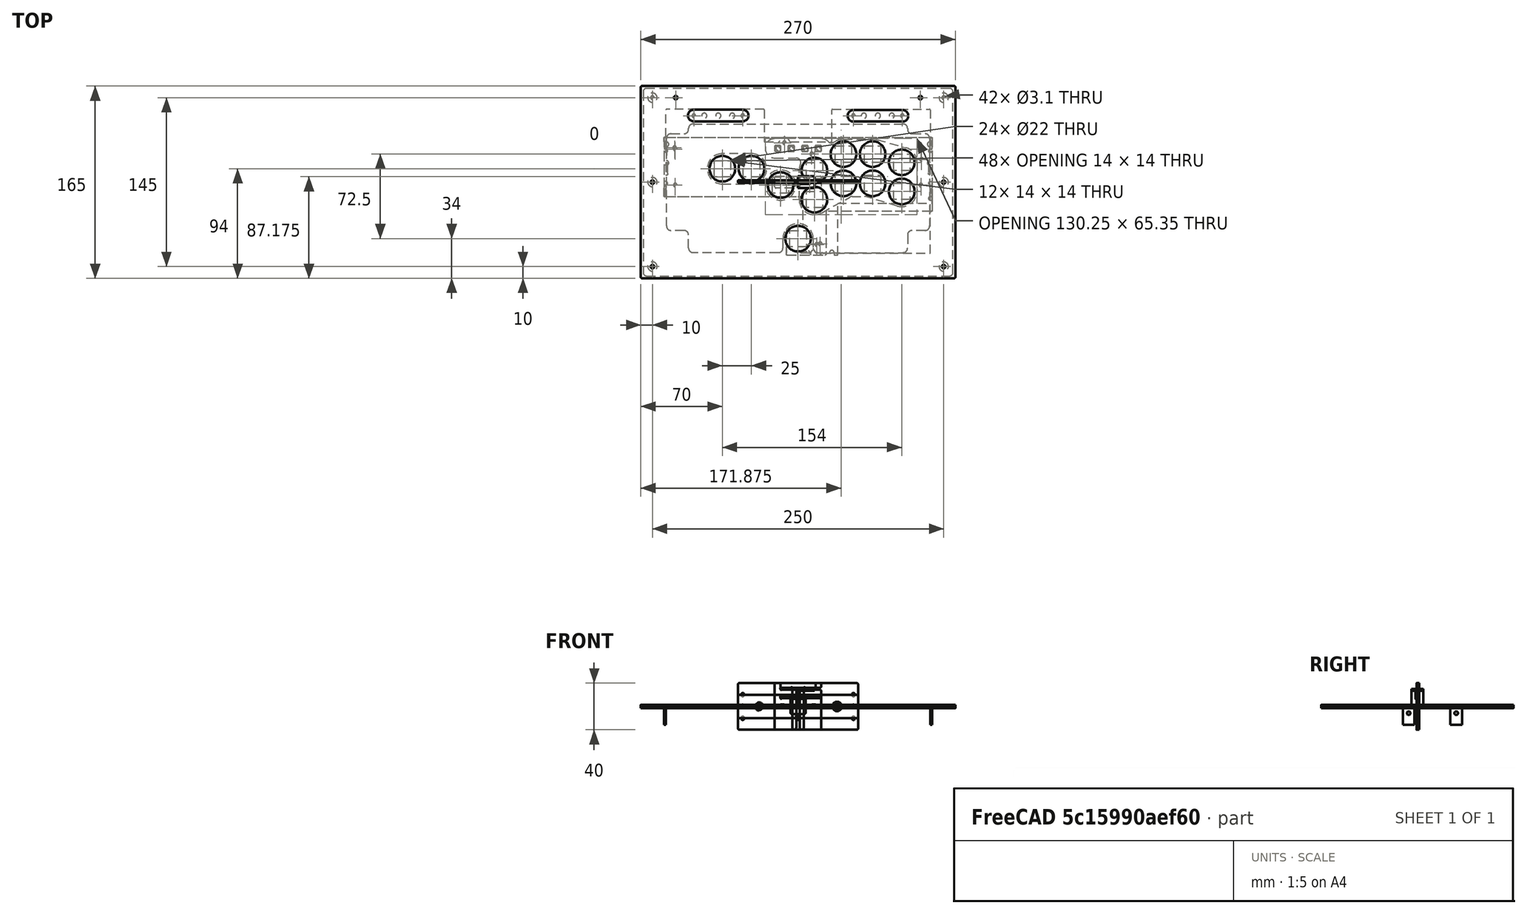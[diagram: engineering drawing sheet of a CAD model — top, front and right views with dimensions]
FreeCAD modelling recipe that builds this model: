
FCSTD DOCUMENT  (FreeCAD 2022.801R14555 (Git shallow))
Label: abc-flat-profiles-plate
License: All rights reserved
LicenseURL: http://en.wikipedia.org/wiki/All_rights_reserved
objects: Sketcher::SketchObject×30, PartDesign::Fillet×21, PartDesign::Body×21, PartDesign::Pad×20, Part::SubShapeBinder×14, PartDesign::SubShapeBinder×13, PartDesign::Pocket×4, PartDesign::FeaturePython×2, App::LinkGroup×2, Spreadsheet::Sheet×1, PartDesign::FeatureBase×1
note: 219 computed .brp shape members not serialized (recipe doc carries the construction recipe); baked Part::Feature solids carry a one-line shape summary decoded from their .brp
EXTERNAL_REF file=abc-flat-profiles.FCStd obj=Link001

FEATURE [Sketcher::SketchObject] Sketch003
  ArcFitTolerance = 0
  AttachmentSupport = -> [XZ_Plane004]
  ExternalBSplineMaxDegree = 0
  ExternalBSplineTolerance = 0
  FullyConstrained = true
  MapMode = 5
  Placement = pos=(0,0,0) rot=(0,0.707107,0.707107;3.14159rad)
  Support = -> [XZ_Plane004]
  TreeRank = 111
  sketch-geometry (38):
    g0: LineSegment StartX=-51.5 StartY=10 StartZ=0 EndX=-51.5 EndY=-10 EndZ=0
    g1: LineSegment StartX=-51.5 StartY=-10 StartZ=0 EndX=51.5 EndY=-10 EndZ=0
    g2: LineSegment StartX=51.5 StartY=-10 StartZ=0 EndX=51.5 EndY=10 EndZ=0
    g3: LineSegment StartX=51.5 StartY=10 StartZ=0 EndX=-51.5 EndY=10 EndZ=0
    g4: LineSegment StartX=-6.5 StartY=6.5 StartZ=0 EndX=-6.5 EndY=-6.5 EndZ=0
    g5: LineSegment StartX=-6.5 StartY=-6.5 StartZ=0 EndX=6.5 EndY=-6.5 EndZ=0
    g6: LineSegment StartX=6.5 StartY=-6.5 StartZ=0 EndX=6.5 EndY=6.5 EndZ=0
    g7: LineSegment StartX=6.5 StartY=6.5 StartZ=0 EndX=-6.5 EndY=6.5 EndZ=0
    g8: GeomPoint [constr] X=0 Y=0 Z=0
    g9: LineSegment [constr] StartX=-17.5 StartY=9.5 StartZ=0 EndX=-17.5 EndY=-9.5 EndZ=0
    g10: LineSegment [constr] StartX=-17.5 StartY=-9.5 StartZ=0 EndX=17.5 EndY=-9.5 EndZ=0
    g11: LineSegment [constr] StartX=17.5 StartY=-9.5 StartZ=0 EndX=17.5 EndY=9.5 EndZ=0
    g12: LineSegment [constr] StartX=17.5 StartY=9.5 StartZ=0 EndX=-17.5 EndY=9.5 EndZ=0
    g13: GeomPoint [constr] X=0 Y=0 Z=0
    g14: Circle CenterX=-47.5 CenterY=0 CenterZ=0 NormalX=0 NormalY=0 NormalZ=1 AngleXU=0 Radius=1.55
    g15: Circle CenterX=47.5 CenterY=0 CenterZ=0 NormalX=0 NormalY=0 NormalZ=1 AngleXU=0 Radius=1.55
    g16: GeomPoint [constr] X=-49.05 Y=0 Z=0
    g17: ArcOfCircle CenterX=-15 CenterY=0 CenterZ=0 NormalX=0 NormalY=0 NormalZ=1 AngleXU=0 Radius=1.55 StartAngle=1.5708 EndAngle=4.71239
    g18: ArcOfCircle CenterX=-12 CenterY=0 CenterZ=0 NormalX=0 NormalY=0 NormalZ=1 AngleXU=0 Radius=1.55 StartAngle=4.71239 EndAngle=7.85398
    g19: LineSegment StartX=-15 StartY=-1.55 StartZ=0 EndX=-12 EndY=-1.55 EndZ=0
    g20: LineSegment StartX=-12 StartY=1.55 StartZ=0 EndX=-15 EndY=1.55 EndZ=0
    g21: ArcOfCircle CenterX=12 CenterY=0 CenterZ=0 NormalX=0 NormalY=0 NormalZ=1 AngleXU=0 Radius=1.55 StartAngle=1.5708 EndAngle=4.71239
    g22: ArcOfCircle CenterX=15 CenterY=0 CenterZ=0 NormalX=0 NormalY=0 NormalZ=1 AngleXU=0 Radius=1.55 StartAngle=4.71239 EndAngle=7.85398
    g23: LineSegment StartX=12 StartY=-1.55 StartZ=0 EndX=15 EndY=-1.55 EndZ=0
    g24: LineSegment StartX=15 StartY=1.55 StartZ=0 EndX=12 EndY=1.55 EndZ=0
    g25: LineSegment [constr] StartX=-19.5 StartY=7.3 StartZ=0 EndX=-19.5 EndY=-7.3 EndZ=0
    g26: LineSegment [constr] StartX=-19.5 StartY=-7.3 StartZ=0 EndX=19.5 EndY=-7.3 EndZ=0
    g27: LineSegment [constr] StartX=19.5 StartY=-7.3 StartZ=0 EndX=19.5 EndY=7.3 EndZ=0
    g28: LineSegment [constr] StartX=19.5 StartY=7.3 StartZ=0 EndX=-19.5 EndY=7.3 EndZ=0
    g29: GeomPoint [constr] X=0 Y=0 Z=0
    g30: Circle CenterX=33.5 CenterY=0 CenterZ=0 NormalX=0 NormalY=0 NormalZ=1 AngleXU=0 Radius=3.175
    g31: GeomPoint [constr] X=30.325 Y=0 Z=0
    g32: GeomPoint [constr] X=36.675 Y=0 Z=0
    g33: GeomPoint [constr] X=45.95 Y=0 Z=0
    g34: Circle CenterX=-33.5 CenterY=0 CenterZ=0 NormalX=0 NormalY=0 NormalZ=1 AngleXU=0 Radius=4.05
    g35: GeomPoint [constr] X=-49.05 Y=0 Z=0
    g36: LineSegment [constr] StartX=-47.5 StartY=0 StartZ=0 EndX=-19.5 EndY=0 EndZ=0
    g37: LineSegment [constr] StartX=47.5 StartY=0 StartZ=0 EndX=19.5 EndY=0 EndZ=0
  constraints (91):
    c: Coincident(g0,g1)
    c: Coincident(g1,g2)
    c: Coincident(g3,g0)
    c: Horizontal(g1)
    c: Vertical(g0)
    c: Vertical(g2)
    c: DistanceY(g0,g0) = 20
    c: Horizontal(g3)
    c: Coincident(g3,g2)
    c: Symmetric(g0,g1,g-1)
    c: Coincident(g4,g5)
    c: Coincident(g5,g6)
    c: Coincident(g6,g7)
    c: Coincident(g7,g4)
    c: Horizontal(g5)
    c: Horizontal(g7)
    c: Vertical(g4)
    c: Vertical(g6)
    c: Symmetric(g5,g4,g8)
    c: Coincident(g8,g-1)
    c: DistanceY(g6,g6) = 13
    c: DistanceX(g5,g5) = 13
    c: Coincident(g9,g10)
    c: Coincident(g10,g11)
    c: Coincident(g11,g12)
    c: Coincident(g12,g9)
    c: Horizontal(g10)
    c: Horizontal(g12)
    c: Vertical(g9)
    c: Vertical(g11)
    c: Symmetric(g10,g9,g13)
    c: Coincident(g13,g8)
    c: DistanceX(g10,g10) = 35
    c: DistanceY(g9,g9) = 19
    c: PointOnObject(g14,g-1)
    c: Symmetric(g14,g15,g-2)
    c: Equal(g14,g15)
    c: PointOnObject(g16,g14)
    c: PointOnObject(g16,g-1)
    c: Tangent(g17,g19) = -1.5708
    c: Tangent(g19,g18) = -1.5708
    c: Tangent(g18,g20) = -1.5708
    c: Tangent(g20,g17) = -1.5708
    c: Equal(g17,g18)
    c: PointOnObject(g17,g-1)
    c: PointOnObject(g18,g-1)
    c: Tangent(g21,g23) = -1.5708
    c: Tangent(g23,g22) = -1.5708
    c: Tangent(g22,g24) = -1.5708
    c: Tangent(g24,g21) = -1.5708
    c: Equal(g21,g22)
    c: Diameter(g17) = 3.1
    c: Equal(g17,g21)
    c: Symmetric(g17,g22,g-2)
    c: Symmetric(g18,g21,g-2)
    c: DistanceX(g18,g21) = 24
    c: DistanceX(g17,g22) = 30
    c: Coincident(g25,g26)
    c: Coincident(g26,g27)
    c: Coincident(g27,g28)
    c: Coincident(g28,g25)
    c: Horizontal(g26)
    c: Horizontal(g28)
    c: Vertical(g25)
    c: Vertical(g27)
    c: Symmetric(g26,g25,g29)
    c: Coincident(g29,g8)
    c: DistanceX(g26,g26) = 39
    c: DistanceY(g27,g27) = 14.6
    c: PointOnObject(g30,g-1)
    c: Diameter(g30) = 6.35
    c: PointOnObject(g31,g30)
    c: PointOnObject(g31,g-1)
    c: PointOnObject(g32,g-1)
    c: PointOnObject(g32,g30)
    c: PointOnObject(g33,g15)
    c: PointOnObject(g33,g-1)
    c: Diameter(g14) = 3.1
    c: PointOnObject(g34,g-1)
    c: Diameter(g34) = 8.1
    c: PointOnObject(g35,g14)
    c: PointOnObject(g35,g-1)
    c: Distance(g14,g0) = 4
    c: Distance(g14,g34) = 14
    c: Coincident(g36,g14)
    c: PointOnObject(g36,g25)
    c: Symmetric(g36,g36,g34)
    c: Coincident(g37,g15)
    c: PointOnObject(g37,g27)
    c: Symmetric(g37,g37,g30)
    c: DistanceX(g3,g3) = 103
FEATURE [PartDesign::Pad] Pad004
  AddSubType = 0
  AlongSketchNormal = false
  CheckUpToFaceLimits = true
  ClaimChildren = false
  Direction = (0,1,2e-16)
  Fit = 0
  FitJoin = 0
  InnerFit = 0
  InnerFitJoin = 0
  InnerTaperAngle = 0
  InnerTaperAngleRev = 0
  Length = 1.5
  Length2 = 100
  Linearize = true
  Midplane = true
  NewSolid = false
  Placement = pos=(0,0,0) rot=(1,0,0;1.5708rad)
  Profile = -> Sketch003
  Suppress = false
  TreeRank = 113
  Type = 0
  _ProfileBasedVersion = 1
FEATURE [PartDesign::Fillet] Fillet005
  AddSubType = 0
  Base = -> Pad004 [Edge5,Edge8,Edge2,Edge1,Edge17,Edge20,Edge13,Edge14]
  BaseFeature = -> Pad004
  NewSolid = false
  Placement = pos=(0,0,0) rot=(1,0,0;1.5708rad)
  Radius = 1
  SupportTransform = false
  Suppress = false
  TreeRank = 114
FEATURE [PartDesign::Body] Body004  label="JackPanel"
  AutoGroupSolids = false
  ClaimAllChildren = false
  ExportMode = 0
  Group = -> [Sketch003,Pad004,Fillet005]
  Origin = -> Origin004
  Tip = -> Fillet005
  TreeRank = 110
  _ExportChildren = -> [Pad004,Fillet005]
  _GroupVersion = 1
FEATURE [Sketcher::SketchObject] Sketch004
  ArcFitTolerance = 0
  AttachmentSupport = -> [XZ_Plane005]
  ExternalBSplineMaxDegree = 0
  ExternalBSplineTolerance = 0
  FullyConstrained = true
  MapMode = 5
  Placement = pos=(0,0,0) rot=(1,0,0;1.5708rad)
  Support = -> [XZ_Plane005]
  TreeRank = 133
  sketch-geometry (29):
    g0: LineSegment StartX=-20 StartY=10 StartZ=0 EndX=-20 EndY=-7 EndZ=0
    g1: LineSegment StartX=-20 StartY=-10 StartZ=0 EndX=20 EndY=-10 EndZ=0
    g2: LineSegment StartX=20 StartY=-10 StartZ=0 EndX=20 EndY=4 EndZ=0
    g3: LineSegment StartX=20 StartY=10 StartZ=0 EndX=-20 EndY=10 EndZ=0
    g4: GeomPoint [constr] X=0 Y=0 Z=0
    g5: LineSegment StartX=-15 StartY=6 StartZ=0 EndX=18.134 EndY=6 EndZ=0
    g6: LineSegment StartX=-15 StartY=4.5 StartZ=0 EndX=-15 EndY=5.2 EndZ=0
    g7: Circle CenterX=0 CenterY=0 CenterZ=0 NormalX=0 NormalY=0 NormalZ=1 AngleXU=0 Radius=1.55
    g8: GeomPoint [constr] X=15 Y=4.5 Z=0
    g9: LineSegment [constr] StartX=-20 StartY=10 StartZ=0 EndX=-20 EndY=14.5 EndZ=0
    g10: LineSegment [constr] StartX=-20 StartY=14.5 StartZ=0 EndX=20 EndY=14.5 EndZ=0
    g11: LineSegment [constr] StartX=20 StartY=14.5 StartZ=0 EndX=20 EndY=10 EndZ=0
    g12: LineSegment StartX=20 StartY=6.5 StartZ=0 EndX=20 EndY=10 EndZ=0
    g13: LineSegment [constr] StartX=20 StartY=-10 StartZ=0 EndX=20 EndY=-14.5 EndZ=0
    g14: LineSegment [constr] StartX=20 StartY=-14.5 StartZ=0 EndX=-20 EndY=-14.5 EndZ=0
    g15: LineSegment [constr] StartX=-20 StartY=-14.5 StartZ=0 EndX=-20 EndY=-10 EndZ=0
    g16: LineSegment [constr] StartX=-20 StartY=-7 StartZ=0 EndX=15 EndY=-7 EndZ=0
    g17: LineSegment [constr] StartX=15 StartY=-7 StartZ=0 EndX=15 EndY=-8.5 EndZ=0
    g18: LineSegment [constr] StartX=15 StartY=-8.5 StartZ=0 EndX=-20 EndY=-8.5 EndZ=0
    g19: GeomPoint [constr] X=-15 Y=-7 Z=0
    g20: LineSegment StartX=-20 StartY=-8.5 StartZ=0 EndX=-20 EndY=-10 EndZ=0
    g21: LineSegment StartX=-20 StartY=-8.5 StartZ=0 EndX=-20 EndY=-7 EndZ=0
    g22: ArcOfCircle CenterX=-15 CenterY=5.6 CenterZ=0 NormalX=0 NormalY=0 NormalZ=1 AngleXU=0 Radius=0.4 StartAngle=1.5708 EndAngle=4.71239
    g23: LineSegment StartX=18.134 StartY=6 StartZ=0 EndX=20 EndY=6.5 EndZ=0
    g24: LineSegment StartX=18.134 StartY=4.5 StartZ=0 EndX=20 EndY=4 EndZ=0
    g25: LineSegment StartX=18.134 StartY=4.5 StartZ=0 EndX=-14.2 EndY=4.5 EndZ=0
    g26: LineSegment [constr] StartX=-14.2 StartY=4.5 StartZ=0 EndX=-15 EndY=4.5 EndZ=0
    g27: ArcOfCircle CenterX=-14.6 CenterY=4.5 CenterZ=0 NormalX=0 NormalY=0 NormalZ=1 AngleXU=0 Radius=0.4 StartAngle=3.14159 EndAngle=6.28319
    g28: Circle [constr] CenterX=0 CenterY=0 CenterZ=0 NormalX=0 NormalY=0 NormalZ=1 AngleXU=0 Radius=3.5
  constraints (76):
    c: Coincident(g20,g1)
    c: Coincident(g1,g2)
    c: Coincident(g12,g3)
    c: Coincident(g3,g0)
    c: Horizontal(g1)
    c: Horizontal(g3)
    c: Vertical(g0)
    c: Vertical(g2)
    c: Symmetric(g1,g0,g4)
    c: Coincident(g4,g-1)
    c: DistanceX(g1,g1) = 40
    c: DistanceY(g20,g0) = 20
    c: Horizontal(g5)
    c: Vertical(g6)
    c: DistanceY(g26,g5) = 1.5
    c: Symmetric(g26,g8,g-2)
    c: DistanceX(g26,g8) = 30
    c: Coincident(g9,g0)
    c: Vertical(g9)
    c: Coincident(g10,g9)
    c: Horizontal(g10)
    c: Coincident(g11,g10)
    c: Coincident(g11,g12)
    c: Vertical(g11)
    c: DistanceY(g9,g9) = 4.5
    c: Distance(g9,g5) = 8.5
    c: Coincident(g7,g4)
    c: Diameter(g7) = 3.1
    c: Vertical(g12)
    c: Coincident(g13,g14)
    c: Coincident(g14,g15)
    c: Horizontal(g14)
    c: Vertical(g13)
    c: Vertical(g15)
    c: Coincident(g15,g20)
    c: Coincident(g13,g1)
    c: DistanceY(g15,g15) = 4.5
    c: Coincident(g16,g17)
    c: Coincident(g17,g18)
    c: Horizontal(g16)
    c: Horizontal(g18)
    c: Vertical(g17)
    c: DistanceY(g17,g17) = 1.5
    c: Symmetric(g19,g16,g-2)
    c: Distance(g19,g16) = 30
    c: Distance(g14,g18) = 6
    c: Coincident(g0,g16)
    c: Coincident(g20,g18)
    c: Vertical(g20)
    c: Coincident(g21,g18)
    c: Coincident(g21,g0)
    c: Vertical(g21)
    c: PointOnObject(g22,g6)
    c: Coincident(g22,g5)
    c: Diameter(g22) = 0.8
    c: Coincident(g6,g22)
    c: Vertical(g5,g6)
    c: Angle(g23,g5) = 2.87979
    c: Vertical(g23,g24)
    c: Coincident(g25,g24)
    c: Coincident(g2,g24)
    c: Coincident(g5,g23)
    c: Coincident(g12,g23)
    c: DistanceY(g2,g12) = 2.5
    c: Vertical(g2,g12)
    c: Coincident(g25,g26)
    c: Horizontal(g25)
    c: Horizontal(g26)
    c: PointOnObject(g27,g26)
    c: Coincident(g27,g25)
    c: Coincident(g27,g26)
    c: Coincident(g27,g6)
    c: Diameter(g27) = 0.8
    c: Angle(g25,g24) = 2.87979
    c: Coincident(g28,g7)
    c: Diameter(g28) = 7
FEATURE [PartDesign::Pad] Pad005
  AddSubType = 0
  AlongSketchNormal = false
  CheckUpToFaceLimits = true
  ClaimChildren = false
  Direction = (0,-1,-2e-16)
  Fit = 0
  FitJoin = 0
  InnerFit = 0
  InnerFitJoin = 0
  InnerTaperAngle = 0
  InnerTaperAngleRev = 0
  Length = 1.5
  Length2 = 100
  Linearize = true
  Midplane = true
  NewSolid = false
  Placement = pos=(0,0,0) rot=(1,0,0;1.5708rad)
  Profile = -> Sketch004
  Refine = true
  Suppress = false
  TreeRank = 134
  Type = 0
  _ProfileBasedVersion = 1
FEATURE [PartDesign::Fillet] Fillet006
  AddSubType = 0
  Base = -> Pad005 [Edge14,Edge27]
  BaseFeature = -> Pad005
  NewSolid = false
  Placement = pos=(0,0,0) rot=(1,0,0;1.5708rad)
  Radius = 0.4
  SupportTransform = false
  Suppress = false
  TreeRank = 135
FEATURE [PartDesign::Fillet] Fillet007
  AddSubType = 0
  Base = -> Fillet006 [Edge36,Edge21,Edge44,Edge43,Edge38,Edge40,Edge41,Edge42]
  BaseFeature = -> Fillet006
  NewSolid = false
  Placement = pos=(0,0,0) rot=(1,0,0;1.5708rad)
  Radius = 1
  SupportTransform = false
  Suppress = false
  TreeRank = 136
FEATURE [PartDesign::Body] Body005  label="Spacer"
  AutoGroupSolids = false
  ClaimAllChildren = false
  ExportMode = 0
  Group = -> [Sketch004,Pad005,Fillet006,Fillet007]
  Origin = -> Origin005
  Tip = -> Fillet007
  TreeRank = 132
  _ExportChildren = -> [Pad005,Fillet006,Fillet007]
  _GroupVersion = 1
FEATURE [Sketcher::SketchObject] Sketch005
  ArcFitTolerance = 0
  AttachmentSupport = -> [XZ_Plane006]
  ExternalBSplineMaxDegree = 0
  ExternalBSplineTolerance = 0
  FullyConstrained = true
  MapMode = 5
  Placement = pos=(0,0,0) rot=(1,0,0;1.5708rad)
  Support = -> [XZ_Plane006]
  TreeRank = 149
  sketch-geometry (30):
    g0: LineSegment StartX=-15 StartY=10 StartZ=0 EndX=15 EndY=10 EndZ=0
    g1: LineSegment StartX=15 StartY=10 StartZ=0 EndX=15 EndY=6 EndZ=0
    g2: LineSegment StartX=-15 StartY=6 StartZ=0 EndX=-15 EndY=10 EndZ=0
    g3: LineSegment StartX=-15 StartY=6 StartZ=0 EndX=-6 EndY=6 EndZ=0
    g4: LineSegment StartX=15 StartY=6 StartZ=0 EndX=6 EndY=6 EndZ=0
    g5: LineSegment StartX=-5 StartY=6 StartZ=0 EndX=-5 EndY=-8.13397 EndZ=0
    g6: LineSegment StartX=-4.5 StartY=-10 StartZ=0 EndX=-2.05 EndY=-10 EndZ=0
    g7: LineSegment StartX=-1.55 StartY=-8.13397 StartZ=0 EndX=-1.55 EndY=4.45 EndZ=0
    g8: LineSegment StartX=1.55 StartY=4.45 StartZ=0 EndX=1.55 EndY=-8.13397 EndZ=0
    g9: LineSegment StartX=2.05 StartY=-10 StartZ=0 EndX=4.5 EndY=-10 EndZ=0
    g10: LineSegment StartX=5 StartY=-8.13397 StartZ=0 EndX=5 EndY=6 EndZ=0
    g11: LineSegment [constr] StartX=-20 StartY=10 StartZ=0 EndX=-20 EndY=-10 EndZ=0
    g12: LineSegment [constr] StartX=-20 StartY=-10 StartZ=0 EndX=20 EndY=-10 EndZ=0
    g13: LineSegment [constr] StartX=20 StartY=-10 StartZ=0 EndX=20 EndY=10 EndZ=0
    g14: LineSegment [constr] StartX=20 StartY=10 StartZ=0 EndX=-20 EndY=10 EndZ=0
    g15: GeomPoint [constr] X=0 Y=0 Z=0
    g16: LineSegment [constr] StartX=-20 StartY=10 StartZ=0 EndX=-20 EndY=14.5 EndZ=0
    g17: LineSegment [constr] StartX=-20 StartY=14.5 StartZ=0 EndX=20 EndY=14.5 EndZ=0
    g18: LineSegment [constr] StartX=20 StartY=14.5 StartZ=0 EndX=20 EndY=10 EndZ=0
    g19: ArcOfCircle CenterX=-5.5 CenterY=6 CenterZ=0 NormalX=0 NormalY=0 NormalZ=1 AngleXU=0 Radius=0.5 StartAngle=2e-16 EndAngle=3.14159
    g20: ArcOfCircle CenterX=5.5 CenterY=6 CenterZ=0 NormalX=0 NormalY=0 NormalZ=1 AngleXU=0 Radius=0.5 StartAngle=2e-16 EndAngle=3.14159
    g21: ArcOfCircle CenterX=0 CenterY=4.45 CenterZ=0 NormalX=0 NormalY=0 NormalZ=1 AngleXU=0 Radius=1.55 StartAngle=0 EndAngle=3.14159
    g22: GeomPoint [constr] X=0 Y=6 Z=0
    g23: LineSegment StartX=-1.55 StartY=-8.13397 StartZ=0 EndX=-2.05 EndY=-10 EndZ=0
    g24: LineSegment StartX=1.55 StartY=-8.13397 StartZ=0 EndX=2.05 EndY=-10 EndZ=0
    g25: LineSegment [constr] StartX=-1.55 StartY=-8.13397 StartZ=0 EndX=-1.55 EndY=-10 EndZ=0
    g26: LineSegment StartX=-5 StartY=-8.13397 StartZ=0 EndX=-4.5 EndY=-10 EndZ=0
    g27: LineSegment StartX=5 StartY=-8.13397 StartZ=0 EndX=4.5 EndY=-10 EndZ=0
    g28: Circle [constr] CenterX=0 CenterY=0 CenterZ=0 NormalX=0 NormalY=0 NormalZ=1 AngleXU=0 Radius=3.5
    g29: Circle [constr] CenterX=0 CenterY=0 CenterZ=0 NormalX=0 NormalY=0 NormalZ=1 AngleXU=0 Radius=1.55
  constraints (84):
    c: Coincident(g0,g1)
    c: Coincident(g2,g0)
    c: Vertical(g1)
    c: Vertical(g2)
    c: Symmetric(g0,g0,g-2)
    c: Coincident(g3,g2)
    c: Horizontal(g3)
    c: Coincident(g4,g1)
    c: Horizontal(g4)
    c: Vertical(g5)
    c: Horizontal(g6)
    c: Vertical(g7)
    c: Vertical(g8)
    c: Horizontal(g9)
    c: Vertical(g10)
    c: DistanceX(g2,g1) = 30
    c: Coincident(g11,g12)
    c: Coincident(g12,g13)
    c: Coincident(g13,g14)
    c: Coincident(g14,g11)
    c: Horizontal(g12)
    c: Horizontal(g14)
    c: Vertical(g11)
    c: Vertical(g13)
    c: Symmetric(g12,g11,g15)
    c: Coincident(g15,g-1)
    c: DistanceY(g13,g13) = 20
    c: DistanceX(g12,g12) = 40
    c: Coincident(g11,g16)
    c: Vertical(g16)
    c: Coincident(g16,g17)
    c: Horizontal(g17)
    c: Coincident(g17,g18)
    c: Vertical(g18)
    c: Coincident(g18,g13)
    c: DistanceY(g16,g16) = 4.5
    c: Distance(g2,g17) = 8.5
    c: PointOnObject(g0,g14)
    c: DistanceX(g3,g5) = 10
    c: PointOnObject(g19,g3)
    c: Coincident(g19,g5)
    c: Diameter(g19) = 1
    c: Coincident(g3,g19)
    c: Horizontal(g3,g5)
    c: PointOnObject(g20,g4)
    c: Coincident(g20,g10)
    c: Equal(g19,g20)
    c: Coincident(g4,g20)
    c: Symmetric(g5,g10,g-2)
    c: Horizontal(g10,g4)
    c: PointOnObject(g21,g-2)
    c: Diameter(g21) = 3.1
    c: Coincident(g7,g21)
    c: Coincident(g8,g21)
    c: Horizontal(g7,g21)
    c: Horizontal(g21,g8)
    c: PointOnObject(g22,g21)
    c: PointOnObject(g22,g-2)
    c: Horizontal(g5,g22)
    c: Angle(g7,g23) = 2.87979
    c: Angle(g24,g8) = 2.87979
    c: Equal(g23,g24)
    c: Coincident(g6,g23)
    c: Coincident(g7,g23)
    c: Coincident(g8,g24)
    c: Coincident(g9,g24)
    c: Coincident(g25,g7)
    c: PointOnObject(g25,g12)
    c: Vertical(g25)
    c: Horizontal(g6,g9)
    c: DistanceX(g6,g25) = 0.5
    c: Angle(g26,g5) = 2.87979
    c: Angle(g10,g27) = 2.87979
    c: Horizontal(g26,g7)
    c: Horizontal(g27,g8)
    c: Coincident(g5,g26)
    c: Coincident(g6,g26)
    c: Coincident(g10,g27)
    c: Coincident(g9,g27)
    c: PointOnObject(g6,g12)
    c: Coincident(g28,g15)
    c: Diameter(g28) = 7
    c: Coincident(g29,g15)
    c: Diameter(g29) = 3.1
FEATURE [PartDesign::Pad] Pad006
  AddSubType = 0
  AlongSketchNormal = false
  CheckUpToFaceLimits = true
  ClaimChildren = false
  Direction = (0,-1,-2e-16)
  Fit = 0
  FitJoin = 0
  InnerFit = 0
  InnerFitJoin = 0
  InnerTaperAngle = 0
  InnerTaperAngleRev = 0
  Length = 1.5
  Length2 = 100
  Linearize = true
  Midplane = true
  NewSolid = false
  Placement = pos=(0,0,0) rot=(1,0,0;1.5708rad)
  Profile = -> Sketch005
  Suppress = false
  TreeRank = 150
  Type = 0
  _ProfileBasedVersion = 1
FEATURE [PartDesign::Fillet] Fillet008
  AddSubType = 0
  Base = -> Pad006 [Edge17,Edge2,Edge5,Edge8,Edge14,Edge11,Edge50,Edge44,Edge41,Edge32,Edge29,Edge23,Edge47,Edge26]
  BaseFeature = -> Pad006
  NewSolid = false
  Placement = pos=(0,0,0) rot=(1,0,0;1.5708rad)
  Radius = 1
  SupportTransform = false
  Suppress = false
  TreeRank = 151
FEATURE [PartDesign::Body] Body006  label="Retainer"
  AutoGroupSolids = false
  ClaimAllChildren = false
  ExportMode = 0
  Group = -> [Sketch005,Pad006,Fillet008]
  Origin = -> Origin006
  Tip = -> Fillet008
  TreeRank = 148
  _ExportChildren = -> [Pad006,Fillet008]
  _GroupVersion = 1
FEATURE [Sketcher::SketchObject] Sketch006  label="SketchFrame"
  ArcFitTolerance = 0
  AttachmentSupport = -> [XY_Plane]
  ExternalBSplineMaxDegree = 0
  ExternalBSplineTolerance = 0
  FullyConstrained = true
  MapMode = 5
  Support = -> [XY_Plane]
  TreeRank = 12
  sketch-geometry (10):
    g0: LineSegment StartX=-135 StartY=82.5 StartZ=0 EndX=-135 EndY=-82.5 EndZ=0
    g1: LineSegment StartX=-135 StartY=-82.5 StartZ=0 EndX=135 EndY=-82.5 EndZ=0
    g2: LineSegment StartX=135 StartY=-82.5 StartZ=0 EndX=135 EndY=82.5 EndZ=0
    g3: LineSegment StartX=135 StartY=82.5 StartZ=0 EndX=-135 EndY=82.5 EndZ=0
    g4: GeomPoint [constr] X=0 Y=0 Z=0
    g5: LineSegment StartX=-115 StartY=62.5 StartZ=0 EndX=-115 EndY=-62.5 EndZ=0
    g6: LineSegment StartX=-115 StartY=-62.5 StartZ=0 EndX=115 EndY=-62.5 EndZ=0
    g7: LineSegment StartX=115 StartY=-62.5 StartZ=0 EndX=115 EndY=62.5 EndZ=0
    g8: LineSegment StartX=115 StartY=62.5 StartZ=0 EndX=-115 EndY=62.5 EndZ=0
    g9: GeomPoint [constr] X=0 Y=0 Z=0
  constraints (24):
    c: Coincident(g0,g1)
    c: Coincident(g1,g2)
    c: Coincident(g2,g3)
    c: Coincident(g3,g0)
    c: Horizontal(g1)
    c: Horizontal(g3)
    c: Vertical(g0)
    c: Vertical(g2)
    c: Symmetric(g1,g0,g4)
    c: Coincident(g4,g-1)
    c: Coincident(g5,g6)
    c: Coincident(g6,g7)
    c: Coincident(g7,g8)
    c: Coincident(g8,g5)
    c: Horizontal(g6)
    c: Horizontal(g8)
    c: Vertical(g5)
    c: Vertical(g7)
    c: Symmetric(g6,g5,g9)
    c: Coincident(g9,g4)
    c: DistanceX(g6,g6) = 230
    c: DistanceY(g5,g5) = 125
    c: Distance(g5,g0) = 20
    c: Distance(g5,g3) = 20
FEATURE [PartDesign::SubShapeBinder] Binder  label="Binder(Sketch001)"
  BindCopyOnChange = 0
  BindMode = 0
  ClaimChildren = false
  Context = -> Body003 [Binder.]
  FillStyle = 0
  Fuse = false
  MakeFace = false
  OffsetFill = false
  OffsetIntersection = false
  OffsetJoinType = 0
  OffsetOpenResult = false
  PartialLoad = false
  Relative = false
  Support = -> [Body001[Sketch001.]]
  TreeRank = 161
  _Version = 8
FEATURE [Sketcher::SketchObject] Sketch007
  ArcFitTolerance = 0
  AttachmentSupport = -> [XY_Plane003]
  ExternalBSplineMaxDegree = 0
  ExternalBSplineTolerance = 0
  ExternalGeometry = -> [Binder]
  FullyConstrained = false
  MapMode = 5
  Support = -> [XY_Plane003]
  TreeRank = 162
  sketch-geometry (8):
    g0: ArcOfCircle CenterX=-89.55 CenterY=57.1618 CenterZ=0 NormalX=0 NormalY=0 NormalZ=1 AngleXU=0 Radius=5 StartAngle=1.5708 EndAngle=4.71239
    g1: ArcOfCircle CenterX=-47.55 CenterY=57.1618 CenterZ=0 NormalX=0 NormalY=0 NormalZ=1 AngleXU=0 Radius=5 StartAngle=4.71239 EndAngle=7.85398
    g2: LineSegment StartX=-89.55 StartY=52.1618 StartZ=0 EndX=-47.55 EndY=52.1618 EndZ=0
    g3: LineSegment StartX=-47.55 StartY=62.1618 StartZ=0 EndX=-89.55 EndY=62.1618 EndZ=0
    g4: ArcOfCircle CenterX=47.55 CenterY=56.9626 CenterZ=0 NormalX=0 NormalY=0 NormalZ=1 AngleXU=0 Radius=5 StartAngle=1.5708 EndAngle=4.71239
    g5: ArcOfCircle CenterX=89.55 CenterY=56.9626 CenterZ=0 NormalX=0 NormalY=0 NormalZ=1 AngleXU=0 Radius=5 StartAngle=4.71239 EndAngle=7.85398
    g6: LineSegment StartX=47.55 StartY=51.9626 StartZ=0 EndX=89.55 EndY=51.9626 EndZ=0
    g7: LineSegment StartX=89.55 StartY=61.9626 StartZ=0 EndX=47.55 EndY=61.9626 EndZ=0
  constraints (12):
    c: Tangent(g0,g2) = -1.5708
    c: Tangent(g2,g1) = -1.5708
    c: Tangent(g1,g3) = -1.5708
    c: Tangent(g3,g0) = -1.5708
    c: Equal(g0,g1)
    c: Tangent(g4,g6) = -1.5708
    c: Tangent(g6,g5) = -1.5708
    c: Tangent(g5,g7) = -1.5708
    c: Tangent(g7,g4) = -1.5708
    c: Equal(g4,g5)
    c: Equal(g0,g4)
    c: DistanceY(g0,g0) = 5
FEATURE [PartDesign::Pad] Pad010
  AddSubType = 0
  AlongSketchNormal = false
  CheckUpToFaceLimits = true
  ClaimChildren = false
  Direction = (0,0,1)
  Fit = 0
  FitJoin = 0
  InnerFit = 0
  InnerFitJoin = 0
  InnerTaperAngle = 0
  InnerTaperAngleRev = 0
  Length = 3
  Length2 = 100
  Linearize = true
  Midplane = true
  NewSolid = false
  Profile = -> Sketch007
  Suppress = false
  TreeRank = 163
  Type = 0
  _ProfileBasedVersion = 1
FEATURE [PartDesign::Fillet] Fillet013
  AddSubType = 0
  Base = -> Pad010 [Edge2,Edge5,Edge8,Edge1]
  BaseFeature = -> Pad010
  NewSolid = false
  Radius = 1
  SupportTransform = false
  Suppress = false
  TreeRank = 164
FEATURE [PartDesign::Body] Body003  label="TopPanel_Acrylic"
  AutoGroupSolids = false
  ClaimAllChildren = false
  ExportMode = 0
  Group = -> [Binder,Sketch007,Pad010,Fillet013]
  Origin = -> Origin003
  Tip = -> Fillet013
  TreeRank = 90
  _ExportChildren = -> [Binder,Pad010,Fillet013]
  _GroupVersion = 1
FEATURE [Sketcher::SketchObject] Sketch011  label="SketchSwitches"
  ArcFitTolerance = 0
  AttachmentSupport = -> [XY_Plane]
  ExternalBSplineMaxDegree = 0
  ExternalBSplineTolerance = 0
  ExternalGeometry = -> [Sketch006]
  FullyConstrained = true
  MapMode = 5
  Support = -> [XY_Plane]
  TreeRank = 14
  sketch-geometry (82):
    g0: LineSegment StartX=-7 StartY=-41.5 StartZ=0 EndX=7 EndY=-41.5 EndZ=0
    g1: LineSegment StartX=7 StartY=-41.5 StartZ=0 EndX=7 EndY=-55.5 EndZ=0
    g2: LineSegment StartX=7 StartY=-55.5 StartZ=0 EndX=-7 EndY=-55.5 EndZ=0
    g3: LineSegment StartX=-7 StartY=-55.5 StartZ=0 EndX=-7 EndY=-41.5 EndZ=0
    g4: LineSegment StartX=-22 StartY=4.5 StartZ=0 EndX=-8 EndY=4.5 EndZ=0
    g5: LineSegment StartX=-8 StartY=4.5 StartZ=0 EndX=-8 EndY=-9.5 EndZ=0
    g6: LineSegment StartX=-8 StartY=-9.5 StartZ=0 EndX=-22 EndY=-9.5 EndZ=0
    g7: LineSegment StartX=-22 StartY=-9.5 StartZ=0 EndX=-22 EndY=4.5 EndZ=0
    g8: LineSegment StartX=-47 StartY=18.5 StartZ=0 EndX=-33 EndY=18.5 EndZ=0
    g9: LineSegment StartX=-33 StartY=18.5 StartZ=0 EndX=-33 EndY=4.5 EndZ=0
    g10: LineSegment StartX=-33 StartY=4.5 StartZ=0 EndX=-47 EndY=4.5 EndZ=0
    g11: LineSegment StartX=-47 StartY=4.5 StartZ=0 EndX=-47 EndY=18.5 EndZ=0
    g12: LineSegment StartX=-72 StartY=18.5 StartZ=0 EndX=-58 EndY=18.5 EndZ=0
    g13: LineSegment StartX=-58 StartY=18.5 StartZ=0 EndX=-58 EndY=4.5 EndZ=0
    g14: LineSegment StartX=-58 StartY=4.5 StartZ=0 EndX=-72 EndY=4.5 EndZ=0
    g15: LineSegment StartX=-72 StartY=4.5 StartZ=0 EndX=-72 EndY=18.5 EndZ=0
    g16: LineSegment StartX=7 StartY=-8 StartZ=0 EndX=21 EndY=-8 EndZ=0
    g17: LineSegment StartX=21 StartY=-8 StartZ=0 EndX=21 EndY=-22 EndZ=0
    g18: LineSegment StartX=21 StartY=-22 StartZ=0 EndX=7 EndY=-22 EndZ=0
    g19: LineSegment StartX=7 StartY=-22 StartZ=0 EndX=7 EndY=-8 EndZ=0
    g20: LineSegment StartX=7 StartY=17 StartZ=0 EndX=21 EndY=17 EndZ=0
    g21: LineSegment StartX=21 StartY=17 StartZ=0 EndX=21 EndY=3 EndZ=0
    g22: LineSegment StartX=21 StartY=3 StartZ=0 EndX=7 EndY=3 EndZ=0
    g23: LineSegment StartX=7 StartY=3 StartZ=0 EndX=7 EndY=17 EndZ=0
    g24: LineSegment StartX=32 StartY=6 StartZ=0 EndX=46 EndY=6 EndZ=0
    g25: LineSegment StartX=46 StartY=6 StartZ=0 EndX=46 EndY=-8 EndZ=0
    g26: LineSegment StartX=46 StartY=-8 StartZ=0 EndX=32 EndY=-8 EndZ=0
    g27: LineSegment StartX=32 StartY=-8 StartZ=0 EndX=32 EndY=6 EndZ=0
    g28: LineSegment StartX=32 StartY=31 StartZ=0 EndX=46 EndY=31 EndZ=0
    g29: LineSegment StartX=46 StartY=31 StartZ=0 EndX=46 EndY=17 EndZ=0
    g30: LineSegment StartX=46 StartY=17 StartZ=0 EndX=32 EndY=17 EndZ=0
    g31: LineSegment StartX=32 StartY=17 StartZ=0 EndX=32 EndY=31 EndZ=0
    g32: LineSegment StartX=57 StartY=6 StartZ=0 EndX=71 EndY=6 EndZ=0
    g33: LineSegment StartX=71 StartY=6 StartZ=0 EndX=71 EndY=-8 EndZ=0
    g34: LineSegment StartX=71 StartY=-8 StartZ=0 EndX=57 EndY=-8 EndZ=0
    g35: LineSegment StartX=57 StartY=-8 StartZ=0 EndX=57 EndY=6 EndZ=0
    g36: LineSegment StartX=57 StartY=31 StartZ=0 EndX=71 EndY=31 EndZ=0
    g37: LineSegment StartX=71 StartY=31 StartZ=0 EndX=71 EndY=17 EndZ=0
    g38: LineSegment StartX=71 StartY=17 StartZ=0 EndX=57 EndY=17 EndZ=0
    g39: LineSegment StartX=57 StartY=17 StartZ=0 EndX=57 EndY=31 EndZ=0
    g40: LineSegment StartX=82 StartY=-1 StartZ=0 EndX=96 EndY=-1 EndZ=0
    g41: LineSegment StartX=96 StartY=-1 StartZ=0 EndX=96 EndY=-15 EndZ=0
    g42: LineSegment StartX=96 StartY=-15 StartZ=0 EndX=82 EndY=-15 EndZ=0
    g43: LineSegment StartX=82 StartY=-15 StartZ=0 EndX=82 EndY=-1 EndZ=0
    g44: LineSegment StartX=82 StartY=24 StartZ=0 EndX=96 EndY=24 EndZ=0
    g45: LineSegment StartX=96 StartY=24 StartZ=0 EndX=96 EndY=10 EndZ=0
    g46: LineSegment StartX=96 StartY=10 StartZ=0 EndX=82 EndY=10 EndZ=0
    g47: LineSegment StartX=82 StartY=10 StartZ=0 EndX=82 EndY=24 EndZ=0
    g48: GeomPoint [constr] X=1e-16 Y=-48.5 Z=0
    g49: GeomPoint [constr] X=-15 Y=-2.5 Z=0
    g50: GeomPoint [constr] X=-40 Y=11.5 Z=0
    g51: GeomPoint [constr] X=-65 Y=11.5 Z=0
    g52: GeomPoint [constr] X=14 Y=-15 Z=0
    g53: GeomPoint [constr] X=14 Y=10 Z=0
    g54: GeomPoint [constr] X=39 Y=-1 Z=0
    g55: GeomPoint [constr] X=39 Y=24 Z=0
    g56: GeomPoint [constr] X=64 Y=-1 Z=0
    g57: GeomPoint [constr] X=64 Y=24 Z=0
    g58: GeomPoint [constr] X=89 Y=-8 Z=0
    g59: GeomPoint [constr] X=89 Y=17 Z=0
    g60: Circle CenterX=-65 CenterY=11.5 CenterZ=0 NormalX=0 NormalY=0 NormalZ=1 AngleXU=0 Radius=11
    g61: Circle CenterX=-40 CenterY=11.5 CenterZ=0 NormalX=0 NormalY=0 NormalZ=1 AngleXU=0 Radius=11
    g62: Circle CenterX=-15 CenterY=-2.5 CenterZ=0 NormalX=0 NormalY=0 NormalZ=1 AngleXU=0 Radius=11
    g63: Circle CenterX=14 CenterY=10 CenterZ=0 NormalX=0 NormalY=0 NormalZ=1 AngleXU=0 Radius=11
    g64: Circle CenterX=14 CenterY=-15 CenterZ=0 NormalX=0 NormalY=0 NormalZ=1 AngleXU=0 Radius=11
    g65: Circle CenterX=39 CenterY=24 CenterZ=0 NormalX=0 NormalY=0 NormalZ=1 AngleXU=0 Radius=11
    g66: Circle CenterX=39 CenterY=-1 CenterZ=0 NormalX=0 NormalY=0 NormalZ=1 AngleXU=0 Radius=11
    g67: Circle CenterX=64 CenterY=24 CenterZ=0 NormalX=0 NormalY=0 NormalZ=1 AngleXU=0 Radius=11
    g68: Circle CenterX=64 CenterY=-1 CenterZ=0 NormalX=0 NormalY=0 NormalZ=1 AngleXU=0 Radius=11
    g69: Circle CenterX=89 CenterY=17 CenterZ=0 NormalX=0 NormalY=0 NormalZ=1 AngleXU=0 Radius=11
    g70: Circle CenterX=89 CenterY=-8 CenterZ=0 NormalX=0 NormalY=0 NormalZ=1 AngleXU=0 Radius=11
    g71: Circle CenterX=1e-16 CenterY=-48.5 CenterZ=0 NormalX=0 NormalY=0 NormalZ=1 AngleXU=0 Radius=11
    g72: Circle CenterX=-80.5 CenterY=57 CenterZ=0 NormalX=0 NormalY=0 NormalZ=1 AngleXU=0 Radius=2.25
    g73: Circle CenterX=-68.5 CenterY=57 CenterZ=0 NormalX=0 NormalY=0 NormalZ=1 AngleXU=0 Radius=2.25
    g74: Circle CenterX=-56.5 CenterY=57 CenterZ=0 NormalX=0 NormalY=0 NormalZ=1 AngleXU=0 Radius=2.25
    g75: Circle CenterX=-89.5 CenterY=57 CenterZ=0 NormalX=0 NormalY=0 NormalZ=1 AngleXU=0 Radius=1.55
    g76: Circle CenterX=-47.5 CenterY=57 CenterZ=0 NormalX=0 NormalY=0 NormalZ=1 AngleXU=0 Radius=1.55
    g77: Circle CenterX=47.5 CenterY=57 CenterZ=0 NormalX=0 NormalY=0 NormalZ=1 AngleXU=0 Radius=1.55
    g78: Circle CenterX=56.5 CenterY=57 CenterZ=0 NormalX=0 NormalY=0 NormalZ=1 AngleXU=0 Radius=2.25
    g79: Circle CenterX=68.5 CenterY=57 CenterZ=0 NormalX=0 NormalY=0 NormalZ=1 AngleXU=0 Radius=2.25
    g80: Circle CenterX=80.5 CenterY=57 CenterZ=0 NormalX=0 NormalY=0 NormalZ=1 AngleXU=0 Radius=2.25
    g81: Circle CenterX=89.5 CenterY=57 CenterZ=0 NormalX=0 NormalY=0 NormalZ=1 AngleXU=0 Radius=1.55
  constraints (204):
    c: Horizontal(g2)
    c: Vertical(g1)
    c: Vertical(g3)
    c: Equal(g3,g0)
    c: Symmetric(g0,g0,g-2)
    c: Coincident(g4,g5)
    c: Coincident(g5,g6)
    c: Coincident(g6,g7)
    c: Coincident(g7,g4)
    c: Horizontal(g4)
    c: Horizontal(g6)
    c: Vertical(g5)
    c: Vertical(g7)
    c: Coincident(g8,g9)
    c: Coincident(g9,g10)
    c: Coincident(g10,g11)
    c: Coincident(g11,g8)
    c: Horizontal(g8)
    c: Horizontal(g10)
    c: Vertical(g9)
    c: Vertical(g11)
    c: Coincident(g12,g13)
    c: Coincident(g13,g14)
    c: Coincident(g14,g15)
    c: Coincident(g15,g12)
    c: Horizontal(g12)
    c: Horizontal(g14)
    c: Vertical(g13)
    c: Vertical(g15)
    c: Equal(g7,g4)
    c: Equal(g4,g3)
    c: Equal(g3,g11)
    c: Equal(g11,g8)
    c: Equal(g3,g15)
    c: Equal(g15,g12)
    c: Coincident(g16,g17)
    c: Coincident(g17,g18)
    c: Coincident(g18,g19)
    c: Coincident(g19,g16)
    c: Horizontal(g16)
    c: Horizontal(g18)
    c: Vertical(g17)
    c: Vertical(g19)
    c: Coincident(g20,g21)
    c: Coincident(g21,g22)
    c: Coincident(g22,g23)
    c: Coincident(g23,g20)
    c: Horizontal(g20)
    c: Horizontal(g22)
    c: Vertical(g21)
    c: Vertical(g23)
    c: Coincident(g24,g25)
    c: Coincident(g25,g26)
    c: Coincident(g26,g27)
    c: Coincident(g27,g24)
    c: Horizontal(g24)
    c: Horizontal(g26)
    c: Vertical(g25)
    c: Vertical(g27)
    c: Coincident(g28,g29)
    c: Coincident(g29,g30)
    c: Coincident(g30,g31)
    c: Coincident(g31,g28)
    c: Horizontal(g28)
    c: Horizontal(g30)
    c: Vertical(g29)
    c: Vertical(g31)
    c: Coincident(g32,g33)
    c: Coincident(g33,g34)
    c: Coincident(g34,g35)
    c: Coincident(g35,g32)
    c: Horizontal(g32)
    c: Horizontal(g34)
    c: Vertical(g33)
    c: Vertical(g35)
    c: Coincident(g36,g37)
    c: Coincident(g37,g38)
    c: Coincident(g38,g39)
    c: Coincident(g39,g36)
    c: Horizontal(g36)
    c: Horizontal(g38)
    c: Vertical(g37)
    c: Vertical(g39)
    c: Coincident(g40,g41)
    c: Coincident(g41,g42)
    c: Coincident(g42,g43)
    c: Coincident(g43,g40)
    c: Horizontal(g40)
    c: Horizontal(g42)
    c: Vertical(g41)
    c: Vertical(g43)
    c: Coincident(g44,g45)
    c: Coincident(g45,g46)
    c: Coincident(g46,g47)
    c: Coincident(g47,g44)
    c: Horizontal(g44)
    c: Horizontal(g46)
    c: Vertical(g45)
    c: Vertical(g47)
    c: Equal(g23,g20)
    c: Equal(g19,g16)
    c: Equal(g27,g24)
    c: Equal(g31,g28)
    c: Equal(g39,g36)
    c: Equal(g35,g32)
    c: Equal(g47,g44)
    c: Equal(g43,g40)
    c: Equal(g3,g23)
    c: Equal(g23,g19)
    c: Equal(g19,g27)
    c: Equal(g27,g31)
    c: Equal(g3,g35)
    c: Equal(g35,g39)
    c: Equal(g39,g43)
    c: Equal(g43,g47)
    c: Vertical(g22,g16)
    c: Vertical(g30,g24)
    c: Vertical(g38,g32)
    c: Vertical(g40,g46)
    c: Symmetric(g0,g1,g48)
    c: Symmetric(g4,g5,g49)
    c: Symmetric(g8,g9,g50)
    c: Symmetric(g12,g13,g51)
    c: Symmetric(g16,g17,g52)
    c: Symmetric(g20,g21,g53)
    c: Symmetric(g24,g25,g54)
    c: Symmetric(g28,g29,g55)
    c: Symmetric(g32,g33,g56)
    c: Symmetric(g36,g37,g57)
    c: Symmetric(g40,g41,g58)
    c: Symmetric(g44,g45,g59)
    c: Distance(g52,g53) = 25
    c: Distance(g54,g55) = 25
    c: Distance(g56,g57) = 25
    c: Distance(g58,g59) = 25
    c: Horizontal(g51,g50)
    c: DistanceX(g53,g55) = 25
    c: DistanceX(g55,g57) = 25
    c: DistanceX(g57,g59) = 25
    c: DistanceX(g51,g50) = 25
    c: DistanceX(g50,g49) = 25
    c: DistanceY(g49,g50) = 14
    c: DistanceY(g53,g55) = 14
    c: Horizontal(g55,g57)
    c: DistanceY(g59,g57) = 7
    c: DistanceX(g49,g48) = 15
    c: DistanceX(g48,g52) = 14
    c: DistanceY(g48,g52) = 33.5
    c: DistanceY(g48,g49) = 46
    c: Coincident(g0,g3)
    c: Coincident(g0,g1)
    c: Coincident(g1,g2)
    c: Coincident(g2,g3)
    c: DistanceX(g2,g2) = 14
    c: DistanceY(g48) = -48.5
    c: Coincident(g60,g51)
    c: Coincident(g61,g50)
    c: Coincident(g62,g49)
    c: Coincident(g63,g53)
    c: Coincident(g64,g52)
    c: Coincident(g65,g55)
    c: Coincident(g66,g54)
    c: Coincident(g67,g57)
    c: Coincident(g68,g56)
    c: Coincident(g69,g59)
    c: Coincident(g70,g58)
    c: Coincident(g71,g48)
    c: Diameter(g71) = 22
    c: Equal(g60,g61)
    c: Equal(g61,g62)
    c: Equal(g62,g63)
    c: Equal(g63,g64)
    c: Equal(g64,g65)
    c: Equal(g65,g66)
    c: Equal(g66,g67)
    c: Equal(g67,g68)
    c: Equal(g68,g69)
    c: Equal(g69,g70)
    c: Equal(g70,g71)
    c: Equal(g72,g73)
    c: Equal(g73,g74)
    c: Diameter(g72) = 4.5
    c: Equal(g75,g76)
    c: Diameter(g75) = 3.1
    c: Distance(g75,g-3) = 25.5
    c: Horizontal(g75,g72)
    c: Horizontal(g72,g73)
    c: Horizontal(g73,g74)
    c: Horizontal(g74,g76)
    c: DistanceX(g75,g72) = 9
    c: DistanceX(g72,g73) = 12
    c: DistanceX(g73,g74) = 12
    c: DistanceX(g74,g76) = 9
    c: DistanceY(g72,g-3) = 5.5
    c: Equal(g76,g77)
    c: Equal(g74,g78)
    c: Equal(g73,g79)
    c: Equal(g72,g80)
    c: Equal(g75,g81)
    c: Symmetric(g76,g77,g-2)
    c: Symmetric(g74,g78,g-2)
    c: Symmetric(g73,g79,g-2)
    c: Symmetric(g72,g80,g-2)
    c: Symmetric(g75,g81,g-2)
FEATURE [Sketcher::SketchObject] Sketch012  label="SketchSwitchPlate"
  ArcFitTolerance = 0
  AttachmentSupport = -> [XY_Plane]
  ExternalBSplineMaxDegree = 0
  ExternalBSplineTolerance = 0
  ExternalGeometry = -> [Sketch006,Sketch011]
  FullyConstrained = true
  MapMode = 5
  Support = -> [XY_Plane]
  TreeRank = 16
  sketch-geometry (73):
    g0: GeomPoint [constr] X=-10 Y=-62.5 Z=0
    g1: LineSegment StartX=4 StartY=-12.5 StartZ=0 EndX=4 EndY=-38.5 EndZ=0
    g2: LineSegment StartX=-113.5 StartY=-12.5 StartZ=0 EndX=4 EndY=-12.5 EndZ=0
    g3: LineSegment StartX=-113.5 StartY=62.5 StartZ=0 EndX=-29 EndY=62.5 EndZ=0
    g4: LineSegment [constr] StartX=113.5 StartY=-61 StartZ=0 EndX=-10 EndY=-61 EndZ=0
    g5: LineSegment [constr] StartX=113.5 StartY=62.5 StartZ=0 EndX=113.5 EndY=-61 EndZ=0
    g6: LineSegment [constr] StartX=-113.5 StartY=62.5 StartZ=0 EndX=-113.5 EndY=-12.5 EndZ=0
    g7: LineSegment StartX=29 StartY=62.5 StartZ=0 EndX=113.5 EndY=62.5 EndZ=0
    g8: LineSegment StartX=-10 StartY=-62.5 StartZ=0 EndX=20 EndY=-62.5 EndZ=0
    g9: LineSegment StartX=20 StartY=-62.5 StartZ=0 EndX=20 EndY=-61 EndZ=0
    g10: GeomPoint [constr] X=5 Y=-61.75 Z=0
    g11: LineSegment StartX=-0.4 StartY=-60.2 StartZ=0 EndX=-0.4 EndY=-59.5 EndZ=0
    g12: LineSegment StartX=0.4 StartY=-59.5 StartZ=0 EndX=8.8 EndY=-59.5 EndZ=0
    g13: LineSegment StartX=9.6 StartY=-59.5 StartZ=0 EndX=9.6 EndY=-60.2 EndZ=0
    g14: LineSegment StartX=9.6 StartY=-61 StartZ=0 EndX=-0.4 EndY=-61 EndZ=0
    g15: GeomPoint [constr] X=5 Y=-60.25 Z=0
    g16: ArcOfCircle CenterX=-0.4 CenterY=-60.6 CenterZ=0 NormalX=0 NormalY=0 NormalZ=1 AngleXU=0 Radius=0.4 StartAngle=1.5708 EndAngle=4.71239
    g17: ArcOfCircle CenterX=9.6 CenterY=-60.6 CenterZ=0 NormalX=0 NormalY=0 NormalZ=1 AngleXU=0 Radius=0.4 StartAngle=4.71239 EndAngle=7.85398
    g18: LineSegment StartX=113.5 StartY=-3.5 StartZ=0 EndX=115 EndY=-3.5 EndZ=0
    g19: LineSegment StartX=115 StartY=-3.5 StartZ=0 EndX=115 EndY=26.5 EndZ=0
    g20: LineSegment StartX=115 StartY=26.5 StartZ=0 EndX=113.5 EndY=26.5 EndZ=0
    g21: GeomPoint [constr] X=114.25 Y=11.5 Z=0
    g22: LineSegment StartX=112 StartY=16.1 StartZ=0 EndX=112 EndY=7.7 EndZ=0
    g23: LineSegment StartX=112 StartY=6.9 StartZ=0 EndX=112.7 EndY=6.9 EndZ=0
    g24: LineSegment StartX=113.5 StartY=6.9 StartZ=0 EndX=113.5 EndY=16.9 EndZ=0
    g25: LineSegment StartX=112.7 StartY=16.9 StartZ=0 EndX=112 EndY=16.9 EndZ=0
    g26: GeomPoint [constr] X=112.75 Y=11.5 Z=0
    g27: GeomPoint [constr] X=113.5 Y=11.9 Z=0
    g28: ArcOfCircle CenterX=113.1 CenterY=16.9 CenterZ=0 NormalX=0 NormalY=0 NormalZ=1 AngleXU=0 Radius=0.4 StartAngle=-2.673e-13 EndAngle=3.14159
    g29: ArcOfCircle CenterX=113.1 CenterY=6.9 CenterZ=0 NormalX=0 NormalY=0 NormalZ=1 AngleXU=0 Radius=0.4 StartAngle=3.14159 EndAngle=6.28319
    g30: LineSegment StartX=-115 StartY=26.5 StartZ=0 EndX=-115 EndY=-3.5 EndZ=0
    g31: LineSegment StartX=-115 StartY=-3.5 StartZ=0 EndX=-113.5 EndY=-3.5 EndZ=0
    g32: LineSegment [constr] StartX=-113.5 StartY=-3.5 StartZ=0 EndX=-113.5 EndY=26.5 EndZ=0
    g33: LineSegment StartX=-113.5 StartY=26.5 StartZ=0 EndX=-115 EndY=26.5 EndZ=0
    g34: GeomPoint [constr] X=-114.25 Y=11.5 Z=0
    g35: GeomPoint [constr] X=-113.5 Y=11.5 Z=0
    g36: LineSegment StartX=-113.5 StartY=16.5 StartZ=0 EndX=-113.5 EndY=6.5 EndZ=0
    g37: LineSegment StartX=-112.7 StartY=6.5 StartZ=0 EndX=-112 EndY=6.5 EndZ=0
    g38: LineSegment StartX=-112 StartY=16.5 StartZ=0 EndX=-112.7 EndY=16.5 EndZ=0
    g39: GeomPoint [constr] X=-112.75 Y=11.5 Z=0
    g40: ArcOfCircle CenterX=-113.1 CenterY=16.5 CenterZ=0 NormalX=0 NormalY=0 NormalZ=1 AngleXU=0 Radius=0.4 StartAngle=2.894e-13 EndAngle=3.14159
    g41: ArcOfCircle CenterX=-113.1 CenterY=6.5 CenterZ=0 NormalX=0 NormalY=0 NormalZ=1 AngleXU=0 Radius=0.4 StartAngle=3.14159 EndAngle=6.28319
    g42: ArcOfCircle CenterX=20.5 CenterY=-61 CenterZ=0 NormalX=0 NormalY=0 NormalZ=1 AngleXU=0 Radius=0.5 StartAngle=-2.13e-14 EndAngle=3.14159
    g43: LineSegment [constr] StartX=20 StartY=-61 StartZ=0 EndX=21 EndY=-61 EndZ=0
    g44: LineSegment StartX=21 StartY=-61 StartZ=0 EndX=113.5 EndY=-61 EndZ=0
    g45: ArcOfCircle CenterX=113.5 CenterY=27 CenterZ=0 NormalX=0 NormalY=0 NormalZ=1 AngleXU=0 Radius=0.5 StartAngle=1.5708 EndAngle=4.71239
    g46: ArcOfCircle CenterX=113.5 CenterY=-4 CenterZ=0 NormalX=0 NormalY=0 NormalZ=1 AngleXU=0 Radius=0.5 StartAngle=1.5708 EndAngle=4.71239
    g47: LineSegment StartX=113.5 StartY=-61 StartZ=0 EndX=113.5 EndY=-4.5 EndZ=0
    g48: LineSegment [constr] StartX=113.5 StartY=-4.5 StartZ=0 EndX=113.5 EndY=-3.5 EndZ=0
    g49: LineSegment StartX=113.5 StartY=62.5 StartZ=0 EndX=113.5 EndY=27.5 EndZ=0
    g50: LineSegment [constr] StartX=113.5 StartY=27.5 StartZ=0 EndX=113.5 EndY=26.5 EndZ=0
    g51: ArcOfCircle CenterX=-113.5 CenterY=27 CenterZ=0 NormalX=0 NormalY=0 NormalZ=1 AngleXU=0 Radius=0.5 StartAngle=4.71239 EndAngle=7.85398
    g52: ArcOfCircle CenterX=-113.5 CenterY=-4 CenterZ=0 NormalX=0 NormalY=0 NormalZ=1 AngleXU=0 Radius=0.5 StartAngle=4.71239 EndAngle=7.85398
    g53: LineSegment StartX=-113.5 StartY=62.5 StartZ=0 EndX=-113.5 EndY=27.5 EndZ=0
    g54: LineSegment [constr] StartX=-113.5 StartY=27.5 StartZ=0 EndX=-113.5 EndY=26.5 EndZ=0
    g55: LineSegment [constr] StartX=-113.5 StartY=-3.5 StartZ=0 EndX=-113.5 EndY=-4.5 EndZ=0
    g56: LineSegment StartX=-113.5 StartY=-4.5 StartZ=0 EndX=-113.5 EndY=-12.5 EndZ=0
    g57: LineSegment StartX=-10 StartY=-41.5 StartZ=0 EndX=-10 EndY=-55.5 EndZ=0
    g58: LineSegment StartX=-10 StartY=-62.5 StartZ=0 EndX=-10 EndY=-55.5 EndZ=0
    g59: LineSegment StartX=4 StartY=-38.5 StartZ=0 EndX=-7 EndY=-38.5 EndZ=0
    g60: ArcOfCircle CenterX=-7 CenterY=-41.5 CenterZ=0 NormalX=0 NormalY=0 NormalZ=1 AngleXU=0 Radius=3 StartAngle=1.5708 EndAngle=3.14159
    g61: LineSegment StartX=-29 StartY=34 StartZ=0 EndX=29 EndY=34 EndZ=0
    g62: LineSegment StartX=-29 StartY=62.5 StartZ=0 EndX=-29 EndY=34 EndZ=0
    g63: LineSegment StartX=29 StartY=34 StartZ=0 EndX=29 EndY=62.5 EndZ=0
    g64: ArcOfCircle CenterX=-112 CenterY=16.1 CenterZ=0 NormalX=0 NormalY=0 NormalZ=1 AngleXU=0 Radius=0.4 StartAngle=4.71239 EndAngle=7.85398
    g65: LineSegment StartX=-112 StartY=7.3 StartZ=0 EndX=-112 EndY=15.7 EndZ=0
    g66: ArcOfCircle CenterX=-112 CenterY=6.9 CenterZ=0 NormalX=0 NormalY=0 NormalZ=1 AngleXU=0 Radius=0.4 StartAngle=4.71239 EndAngle=7.85398
    g67: ArcOfCircle CenterX=9.2 CenterY=-59.5 CenterZ=0 NormalX=0 NormalY=0 NormalZ=1 AngleXU=0 Radius=0.4 StartAngle=0 EndAngle=3.14159
    g68: ArcOfCircle CenterX=2e-16 CenterY=-59.5 CenterZ=0 NormalX=0 NormalY=0 NormalZ=1 AngleXU=0 Radius=0.4 StartAngle=3.1e-15 EndAngle=3.14159
    g69: ArcOfCircle CenterX=112 CenterY=16.5 CenterZ=0 NormalX=0 NormalY=0 NormalZ=1 AngleXU=0 Radius=0.4 StartAngle=1.5708 EndAngle=4.71239
    g70: ArcOfCircle CenterX=112 CenterY=7.3 CenterZ=0 NormalX=0 NormalY=0 NormalZ=1 AngleXU=0 Radius=0.4 StartAngle=1.5708 EndAngle=4.71239
    g71: GeomPoint [constr] X=4e-16 Y=-41.5 Z=0
    g72: GeomPoint [constr] X=0 Y=34 Z=0
  constraints (205):
    c: Coincident(g3,g62)
    c: Vertical(g1)
    c: Horizontal(g2)
    c: Horizontal(g3)
    c: Horizontal(g4)
    c: Vertical(g5)
    c: Coincident(g5,g4)
    c: Vertical(g6)
    c: Coincident(g6,g2)
    c: Coincident(g7,g63)
    c: Coincident(g7,g5)
    c: Coincident(g8,g9)
    c: Horizontal(g8)
    c: Vertical(g9)
    c: PointOnObject(g9,g4)
    c: DistanceX(g8,g8) = 30
    c: Coincident(g43,g9)
    c: Coincident(g44,g5)
    c: Horizontal(g12)
    c: Horizontal(g14)
    c: Vertical(g11)
    c: Vertical(g13)
    c: DistanceY(g14,g12) = 1.5
    c: PointOnObject(g16,g11)
    c: Coincident(g16,g14)
    c: PointOnObject(g17,g13)
    c: Coincident(g17,g14)
    c: Coincident(g11,g16)
    c: Coincident(g13,g17)
    c: Vertical(g11,g14)
    c: Vertical(g13,g14)
    c: Symmetric(g12,g14,g15)
    c: PointOnObject(g14,g4)
    c: Coincident(g18,g19)
    c: Coincident(g19,g20)
    c: Horizontal(g18)
    c: Horizontal(g20)
    c: Vertical(g19)
    c: Symmetric(g18,g20,g21)
    c: DistanceX(g18,g18) = 1.5
    c: DistanceY(g18,g20) = 30
    c: Vertical(g18,g20)
    c: PointOnObject(g20,g5)
    c: Coincident(g47,g44)
    c: Coincident(g48,g18)
    c: Coincident(g49,g7)
    c: Coincident(g50,g20)
    c: Horizontal(g23)
    c: Horizontal(g25)
    c: Vertical(g22)
    c: Vertical(g24)
    c: Horizontal(g21,g26)
    c: DistanceX(g22,g24) = 1.5
    c: Symmetric(g24,g24,g27)
    c: PointOnObject(g27,g5)
    c: PointOnObject(g28,g25)
    c: Coincident(g28,g24)
    c: PointOnObject(g29,g23)
    c: Coincident(g29,g24)
    c: Coincident(g25,g28)
    c: Coincident(g23,g29)
    c: Horizontal(g23,g24)
    c: Horizontal(g25,g24)
    c: Symmetric(g22,g24,g26)
    c: Coincident(g30,g31)
    c: Coincident(g31,g32)
    c: Coincident(g32,g33)
    c: Coincident(g33,g30)
    c: Horizontal(g31)
    c: Horizontal(g33)
    c: Vertical(g30)
    c: Vertical(g32)
    c: Symmetric(g31,g30,g34)
    c: DistanceY(g30,g30) = 30
    c: DistanceX(g31,g31) = 1.5
    c: Symmetric(g32,g32,g35)
    c: PointOnObject(g35,g6)
    c: Horizontal(g34,g21)
    c: Coincident(g53,g3)
    c: Coincident(g54,g33)
    c: Coincident(g55,g31)
    c: Coincident(g56,g2)
    c: Horizontal(g37)
    c: Horizontal(g38)
    c: Vertical(g36)
    c: DistanceX(g36,g66) = 1.5
    c: Horizontal(g34,g39)
    c: PointOnObject(g40,g38)
    c: Coincident(g40,g36)
    c: PointOnObject(g41,g37)
    c: Coincident(g41,g36)
    c: Diameter(g40) = 0.8
    c: Coincident(g38,g40)
    c: Coincident(g37,g41)
    c: Symmetric(g36,g66,g39)
    c: Horizontal(g36,g38)
    c: Horizontal(g36,g37)
    c: PointOnObject(g35,g36)
    c: Coincident(g42,g9)
    c: Diameter(g42) = 1
    c: Coincident(g43,g44)
    c: PointOnObject(g42,g43)
    c: Coincident(g43,g42)
    c: Horizontal(g43)
    c: Coincident(g45,g20)
    c: Coincident(g46,g18)
    c: Equal(g46,g45)
    c: Diameter(g46) = 1
    c: Coincident(g47,g48)
    c: PointOnObject(g46,g48)
    c: Coincident(g47,g46)
    c: Coincident(g49,g50)
    c: PointOnObject(g45,g50)
    c: Coincident(g49,g45)
    c: Vertical(g48)
    c: Vertical(g49)
    c: Coincident(g51,g33)
    c: Coincident(g52,g31)
    c: Equal(g52,g51)
    c: Diameter(g51) = 1
    c: Coincident(g53,g54)
    c: PointOnObject(g51,g54)
    c: Coincident(g51,g53)
    c: Vertical(g53)
    c: Coincident(g55,g56)
    c: PointOnObject(g52,g55)
    c: Coincident(g56,g52)
    c: Vertical(g56)
    c: Vertical(g57)
    c: Coincident(g59,g1)
    c: Coincident(g60,g59)
    c: Coincident(g60,g57)
    c: Horizontal(g61)
    c: Vertical(g62)
    c: Coincident(g62,g61)
    c: Vertical(g63)
    c: Coincident(g65,g64)
    c: Coincident(g38,g64)
    c: Vertical(g64,g64)
    c: Vertical(g64,g38)
    c: Equal(g40,g64)
    c: Vertical(g65)
    c: Equal(g41,g66)
    c: Coincident(g65,g66)
    c: Coincident(g37,g66)
    c: Vertical(g65,g66)
    c: Vertical(g66,g66)
    c: Equal(g64,g41)
    c: DistanceY(g36,g36) = 10
    c: DistanceX(g14,g14) = 10
    c: Coincident(g67,g13)
    c: Coincident(g67,g12)
    c: Equal(g17,g67)
    c: Horizontal(g12,g67)
    c: Horizontal(g67,g13)
    c: Coincident(g68,g11)
    c: Coincident(g68,g12)
    c: Horizontal(g11,g68)
    c: Horizontal(g68,g12)
    c: Equal(g16,g68)
    c: Equal(g68,g67)
    c: Diameter(g16) = 0.8
    c: DistanceY(g24,g24) = 10
    c: Coincident(g69,g22)
    c: Tangent(g69,g25) = -1.5708
    c: Equal(g29,g70)
    c: Equal(g70,g28)
    c: Equal(g28,g69)
    c: Diameter(g29) = 0.8
    c: Vertical(g22,g23)
    c: Coincident(g70,g22)
    c: Coincident(g70,g23)
    c: Vertical(g22,g70)
    c: Vertical(g22,g69)
    c: PointOnObject(g30,g-3)
    c: PointOnObject(g3,g-4)
    c: PointOnObject(g7,g-4)
    c: Coincident(g61,g63)
    c: PointOnObject(g5,g-4)
    c: PointOnObject(g19,g-5)
    c: PointOnObject(g8,g-6)
    c: Coincident(g1,g2)
    c: Horizontal(g59)
    c: Vertical(g58)
    c: Coincident(g0,g8)
    c: Coincident(g0,g58)
    c: PointOnObject(g4,g58)
    c: Distance(g14,g8) = 1.5
    c: Distance(g61,g-7) = 3
    c: Distance(g1,g-8) = 3
    c: Distance(g1,g-9) = 3
    c: Distance(g1,g-11) = 3
    c: Vertical(g60,g59)
    c: Horizontal(g57,g60)
    c: Coincident(g60,g-11)
    c: Symmetric(g-11,g-11,g71)
    c: Horizontal(g57,g-10)
    c: Coincident(g6,g3)
    c: Coincident(g57,g58)
    c: Symmetric(g4,g8,g10)
    c: Vertical(g10,g15)
    c: DistanceX(g61,g-7) = 3
    c: Symmetric(g61,g61,g72)
    c: PointOnObject(g72,g-2)
    c: Horizontal(g39,g-12)
FEATURE [Sketcher::SketchObject] Sketch009  label="SketchPCB"
  ArcFitTolerance = 0
  AttachmentSupport = -> [XY_Plane]
  ExternalBSplineMaxDegree = 0
  ExternalBSplineTolerance = 0
  ExternalGeometry = -> [Sketch012,Sketch006]
  FullyConstrained = true
  MapMode = 5
  Support = -> [XY_Plane]
  TreeRank = 13
  sketch-geometry (60):
    g0: LineSegment StartX=-110 StartY=-9.5 StartZ=0 EndX=-110 EndY=-55.5 EndZ=0
    g1: LineSegment StartX=-110 StartY=-55.5 StartZ=0 EndX=-13 EndY=-55.5 EndZ=0
    g2: LineSegment StartX=-13 StartY=-55.5 StartZ=0 EndX=-13 EndY=-9.5 EndZ=0
    g3: LineSegment StartX=-13 StartY=-9.5 StartZ=0 EndX=-110 EndY=-9.5 EndZ=0
    g4: GeomPoint [constr] X=-61.5 Y=-32.5 Z=0
    g5: LineSegment [constr] StartX=-105.5 StartY=-14 StartZ=0 EndX=-105.5 EndY=-51 EndZ=0
    g6: LineSegment [constr] StartX=-105.5 StartY=-51 StartZ=0 EndX=-17.5 EndY=-51 EndZ=0
    g7: LineSegment [constr] StartX=-17.5 StartY=-51 StartZ=0 EndX=-17.5 EndY=-14 EndZ=0
    g8: LineSegment [constr] StartX=-17.5 StartY=-14 StartZ=0 EndX=-105.5 EndY=-14 EndZ=0
    g9: GeomPoint [constr] X=-61.5 Y=-32.5 Z=0
    g10: Circle CenterX=-105.5 CenterY=-14 CenterZ=0 NormalX=0 NormalY=0 NormalZ=1 AngleXU=0 Radius=1.55
    g11: Circle CenterX=-105.5 CenterY=-51 CenterZ=0 NormalX=0 NormalY=0 NormalZ=1 AngleXU=0 Radius=1.55
    g12: Circle CenterX=-17.5 CenterY=-14 CenterZ=0 NormalX=0 NormalY=0 NormalZ=1 AngleXU=0 Radius=1.55
    g13: Circle CenterX=-17.5 CenterY=-51 CenterZ=0 NormalX=0 NormalY=0 NormalZ=1 AngleXU=0 Radius=1.55
    g14: LineSegment StartX=-111.75 StartY=-44.75 StartZ=0 EndX=-111.75 EndY=-57.25 EndZ=0
    g15: LineSegment StartX=-111.75 StartY=-57.25 StartZ=0 EndX=-99.25 EndY=-57.25 EndZ=0
    g16: LineSegment StartX=-99.25 StartY=-57.25 StartZ=0 EndX=-99.25 EndY=-44.75 EndZ=0
    g17: LineSegment StartX=-99.25 StartY=-44.75 StartZ=0 EndX=-111.75 EndY=-44.75 EndZ=0
    g18: GeomPoint [constr] X=-105.5 Y=-51 Z=0
    g19: LineSegment StartX=-111.75 StartY=-7.75 StartZ=0 EndX=-111.75 EndY=-20.25 EndZ=0
    g20: LineSegment StartX=-111.75 StartY=-20.25 StartZ=0 EndX=-99.25 EndY=-20.25 EndZ=0
    g21: LineSegment StartX=-99.25 StartY=-20.25 StartZ=0 EndX=-99.25 EndY=-7.75 EndZ=0
    g22: LineSegment StartX=-99.25 StartY=-7.75 StartZ=0 EndX=-111.75 EndY=-7.75 EndZ=0
    g23: GeomPoint [constr] X=-105.5 Y=-14 Z=0
    g24: LineSegment StartX=-23.75 StartY=-7.75 StartZ=0 EndX=-23.75 EndY=-20.25 EndZ=0
    g25: LineSegment StartX=-23.75 StartY=-20.25 StartZ=0 EndX=-11.25 EndY=-20.25 EndZ=0
    g26: LineSegment StartX=-11.25 StartY=-20.25 StartZ=0 EndX=-11.25 EndY=-7.75 EndZ=0
    g27: LineSegment StartX=-11.25 StartY=-7.75 StartZ=0 EndX=-23.75 EndY=-7.75 EndZ=0
    g28: GeomPoint [constr] X=-17.5 Y=-14 Z=0
    g29: LineSegment StartX=-11.25 StartY=-57.25 StartZ=0 EndX=-11.25 EndY=-44.75 EndZ=0
    g30: LineSegment StartX=-11.25 StartY=-44.75 StartZ=0 EndX=-23.75 EndY=-44.75 EndZ=0
    g31: LineSegment StartX=-23.75 StartY=-44.75 StartZ=0 EndX=-23.75 EndY=-57.25 EndZ=0
    g32: LineSegment StartX=-23.75 StartY=-57.25 StartZ=0 EndX=-11.25 EndY=-57.25 EndZ=0
    g33: GeomPoint [constr] X=-17.5 Y=-51 Z=0
    g34: LineSegment StartX=-13 StartY=-26.75 StartZ=0 EndX=19 EndY=-26.75 EndZ=0
    g35: LineSegment StartX=19 StartY=-26.75 StartZ=0 EndX=19 EndY=-38.25 EndZ=0
    g36: LineSegment StartX=19 StartY=-38.25 StartZ=0 EndX=-13 EndY=-38.25 EndZ=0
    g37: LineSegment StartX=-13 StartY=-38.25 StartZ=0 EndX=-13 EndY=-26.75 EndZ=0
    g38: LineSegment StartX=-13 StartY=-17 StartZ=0 EndX=19 EndY=-17 EndZ=0
    g39: LineSegment StartX=19 StartY=-17 StartZ=0 EndX=19 EndY=-28.5 EndZ=0
    g40: LineSegment StartX=19 StartY=-28.5 StartZ=0 EndX=-13 EndY=-28.5 EndZ=0
    g41: LineSegment StartX=-13 StartY=-28.5 StartZ=0 EndX=-13 EndY=-17 EndZ=0
    g42: LineSegment StartX=-13 StartY=-17 StartZ=0 EndX=-29.5 EndY=-17 EndZ=0
    g43: LineSegment StartX=-29.5 StartY=-17 StartZ=0 EndX=-29.5 EndY=-28.5 EndZ=0
    g44: LineSegment StartX=-29.5 StartY=-28.5 StartZ=0 EndX=-13 EndY=-28.5 EndZ=0
    g45: LineSegment StartX=-13 StartY=-28.5 StartZ=0 EndX=-13 EndY=-17 EndZ=0
    g46: LineSegment StartX=-13 StartY=-26.75 StartZ=0 EndX=-29.5 EndY=-26.75 EndZ=0
    g47: LineSegment StartX=-29.5 StartY=-26.75 StartZ=0 EndX=-29.5 EndY=-38.25 EndZ=0
    g48: LineSegment StartX=-29.5 StartY=-38.25 StartZ=0 EndX=-13 EndY=-38.25 EndZ=0
    g49: LineSegment StartX=-13 StartY=-38.25 StartZ=0 EndX=-13 EndY=-26.75 EndZ=0
    g50: GeomPoint X=-13 Y=-32.5 Z=0
    g51: Circle [constr] CenterX=32 CenterY=-24.3 CenterZ=0 NormalX=0 NormalY=0 NormalZ=1 AngleXU=0 Radius=1.05
    g52: Circle [constr] CenterX=32 CenterY=-35.7 CenterZ=0 NormalX=0 NormalY=0 NormalZ=1 AngleXU=0 Radius=1.05
    g53: Circle [constr] CenterX=79 CenterY=-24.3 CenterZ=0 NormalX=0 NormalY=0 NormalZ=1 AngleXU=0 Radius=1.05
    g54: Circle [constr] CenterX=79 CenterY=-35.7 CenterZ=0 NormalX=0 NormalY=0 NormalZ=1 AngleXU=0 Radius=1.05
    g55: LineSegment [constr] StartX=30 StartY=-19.5 StartZ=0 EndX=30 EndY=-40.5 EndZ=0
    g56: LineSegment [constr] StartX=30 StartY=-40.5 StartZ=0 EndX=81 EndY=-40.5 EndZ=0
    g57: LineSegment [constr] StartX=81 StartY=-40.5 StartZ=0 EndX=81 EndY=-19.5 EndZ=0
    g58: LineSegment [constr] StartX=81 StartY=-19.5 StartZ=0 EndX=30 EndY=-19.5 EndZ=0
    g59: GeomPoint X=55.5 Y=-30 Z=0
  constraints (152):
    c: Coincident(g0,g1)
    c: Coincident(g1,g2)
    c: Coincident(g2,g3)
    c: Coincident(g3,g0)
    c: Horizontal(g1)
    c: Horizontal(g3)
    c: Vertical(g0)
    c: Vertical(g2)
    c: Symmetric(g1,g0,g4)
    c: Coincident(g5,g6)
    c: Coincident(g6,g7)
    c: Coincident(g7,g8)
    c: Coincident(g8,g5)
    c: Horizontal(g6)
    c: Horizontal(g8)
    c: Vertical(g5)
    c: Vertical(g7)
    c: Symmetric(g6,g5,g9)
    c: Coincident(g9,g4)
    c: Coincident(g10,g5)
    c: Coincident(g11,g5)
    c: Coincident(g12,g7)
    c: Coincident(g13,g6)
    c: Equal(g10,g11)
    c: Equal(g11,g12)
    c: Equal(g12,g13)
    c: Coincident(g14,g15)
    c: Coincident(g15,g16)
    c: Coincident(g16,g17)
    c: Coincident(g17,g14)
    c: Horizontal(g15)
    c: Horizontal(g17)
    c: Vertical(g14)
    c: Vertical(g16)
    c: Symmetric(g15,g14,g18)
    c: Coincident(g19,g20)
    c: Coincident(g20,g21)
    c: Coincident(g21,g22)
    c: Coincident(g22,g19)
    c: Horizontal(g20)
    c: Horizontal(g22)
    c: Vertical(g19)
    c: Vertical(g21)
    c: Symmetric(g20,g19,g23)
    c: Coincident(g23,g10)
    c: Coincident(g24,g25)
    c: Coincident(g25,g26)
    c: Coincident(g26,g27)
    c: Coincident(g27,g24)
    c: Horizontal(g25)
    c: Horizontal(g27)
    c: Vertical(g24)
    c: Vertical(g26)
    c: Symmetric(g25,g24,g28)
    c: Coincident(g28,g12)
    c: Coincident(g29,g30)
    c: Coincident(g30,g31)
    c: Coincident(g31,g32)
    c: Coincident(g32,g29)
    c: Horizontal(g30)
    c: Horizontal(g32)
    c: Vertical(g29)
    c: Vertical(g31)
    c: Symmetric(g30,g29,g33)
    c: Coincident(g33,g13)
    c: Coincident(g11,g18)
    c: Equal(g14,g17)
    c: Equal(g19,g22)
    c: Equal(g24,g27)
    c: Equal(g31,g30)
    c: DistanceY(g14,g14) = 12.5
    c: Equal(g14,g19)
    c: Equal(g19,g24)
    c: Equal(g24,g31)
    c: DistanceY(g0,g0) = 46
    c: DistanceY(g5,g5) = 37
    c: Diameter(g11) = 3.1
    c: DistanceX(g3,g3) = 97
    c: DistanceX(g8,g8) = 88
    c: Coincident(g34,g35)
    c: Coincident(g35,g36)
    c: Coincident(g36,g37)
    c: Coincident(g37,g34)
    c: Horizontal(g34)
    c: Horizontal(g36)
    c: Vertical(g35)
    c: Vertical(g37)
    c: Coincident(g38,g39)
    c: Coincident(g39,g40)
    c: Coincident(g40,g41)
    c: Coincident(g41,g38)
    c: Horizontal(g38)
    c: Horizontal(g40)
    c: Vertical(g39)
    c: Vertical(g41)
    c: DistanceX(g36,g36) = 32
    c: DistanceY(g37,g37) = 11.5
    c: Equal(g37,g41)
    c: Equal(g34,g40)
    c: Coincident(g42,g43)
    c: Coincident(g43,g44)
    c: Coincident(g44,g45)
    c: Coincident(g45,g42)
    c: Horizontal(g42)
    c: Horizontal(g44)
    c: Vertical(g43)
    c: Vertical(g45)
    c: PointOnObject(g42,g2)
    c: DistanceX(g42,g42) = 16.5
    c: DistanceY(g43,g43) = 11.5
    c: Coincident(g46,g47)
    c: Coincident(g47,g48)
    c: Coincident(g48,g49)
    c: Coincident(g49,g46)
    c: Horizontal(g46)
    c: Horizontal(g48)
    c: Vertical(g47)
    c: Vertical(g49)
    c: Equal(g47,g43)
    c: Equal(g42,g46)
    c: Symmetric(g2,g2,g50)
    c: Symmetric(g49,g49,g50)
    c: Distance(g43,g3) = 19
    c: Coincident(g38,g42)
    c: Coincident(g34,g46)
    c: Equal(g51,g52)
    c: Equal(g52,g53)
    c: Equal(g53,g54)
    c: Diameter(g51) = 2.1
    c: Horizontal(g51,g53)
    c: Horizontal(g52,g54)
    c: Vertical(g51,g52)
    c: Vertical(g53,g54)
    c: Coincident(g55,g56)
    c: Coincident(g56,g57)
    c: Coincident(g57,g58)
    c: Coincident(g58,g55)
    c: Horizontal(g56)
    c: Horizontal(g58)
    c: Vertical(g55)
    c: Vertical(g57)
    c: Symmetric(g56,g55,g59)
    c: DistanceX(g58,g58) = 51
    c: DistanceY(g55,g55) = 21
    c: Distance(g51,g58) = 4.8
    c: Distance(g52,g56) = 4.8
    c: Distance(g51,g55) = 2
    c: Distance(g53,g57) = 2
    c: Distance(g0,g-4) = 5
    c: Distance(g0,g-5) = 7
    c: DistanceX(g-2,g55) = 30
    c: Distance(g55,g-5) = 22
FEATURE [Sketcher::SketchObject] Sketch014  label="SketchLED"
  ArcFitTolerance = 0
  AttachmentSupport = -> [XY_Plane]
  ExternalBSplineMaxDegree = 0
  ExternalBSplineTolerance = 0
  ExternalGeometry = -> [Sketch011]
  FullyConstrained = true
  MapMode = 5
  Support = -> [XY_Plane]
  TreeRank = 15
  sketch-geometry (39):
    g0: LineSegment StartX=-19.9 StartY=31.5 StartZ=0 EndX=-19.9 EndY=26.5 EndZ=0
    g1: LineSegment StartX=-19.9 StartY=26.5 StartZ=0 EndX=-14.9 EndY=26.5 EndZ=0
    g2: LineSegment StartX=-14.9 StartY=26.5 StartZ=0 EndX=-14.9 EndY=31.5 EndZ=0
    g3: LineSegment StartX=-14.9 StartY=31.5 StartZ=0 EndX=-19.9 EndY=31.5 EndZ=0
    g4: GeomPoint [constr] X=-17.4 Y=29 Z=0
    g5: LineSegment StartX=-8.3 StartY=31.5 StartZ=0 EndX=-8.3 EndY=26.5 EndZ=0
    g6: LineSegment StartX=-8.3 StartY=26.5 StartZ=0 EndX=-3.3 EndY=26.5 EndZ=0
    g7: LineSegment StartX=-3.3 StartY=26.5 StartZ=0 EndX=-3.3 EndY=31.5 EndZ=0
    g8: LineSegment StartX=-3.3 StartY=31.5 StartZ=0 EndX=-8.3 EndY=31.5 EndZ=0
    g9: GeomPoint [constr] X=-5.8 Y=29 Z=0
    g10: LineSegment StartX=3.3 StartY=31.5 StartZ=0 EndX=3.3 EndY=26.5 EndZ=0
    g11: LineSegment StartX=3.3 StartY=26.5 StartZ=0 EndX=8.3 EndY=26.5 EndZ=0
    g12: LineSegment StartX=8.3 StartY=26.5 StartZ=0 EndX=8.3 EndY=31.5 EndZ=0
    g13: LineSegment StartX=8.3 StartY=31.5 StartZ=0 EndX=3.3 EndY=31.5 EndZ=0
    g14: GeomPoint [constr] X=5.8 Y=29 Z=0
    g15: LineSegment StartX=14.9 StartY=31.5 StartZ=0 EndX=14.9 EndY=26.5 EndZ=0
    g16: LineSegment StartX=14.9 StartY=26.5 StartZ=0 EndX=19.9 EndY=26.5 EndZ=0
    g17: LineSegment StartX=19.9 StartY=26.5 StartZ=0 EndX=19.9 EndY=31.5 EndZ=0
    g18: LineSegment StartX=19.9 StartY=31.5 StartZ=0 EndX=14.9 EndY=31.5 EndZ=0
    g19: GeomPoint [constr] X=17.4 Y=29 Z=0
    g20: Circle CenterX=-11.7 CenterY=33.8 CenterZ=0 NormalX=0 NormalY=0 NormalZ=1 AngleXU=0 Radius=1.55
    g21: Circle CenterX=11.7 CenterY=24.2 CenterZ=0 NormalX=0 NormalY=0 NormalZ=1 AngleXU=0 Radius=1.55
    g22: Circle CenterX=0 CenterY=23.5 CenterZ=0 NormalX=0 NormalY=0 NormalZ=1 AngleXU=0 Radius=1.05
    g23: Circle CenterX=0 CenterY=34.5 CenterZ=0 NormalX=0 NormalY=0 NormalZ=1 AngleXU=0 Radius=1.05
    g24: LineSegment StartX=-31.8 StartY=36.5 StartZ=0 EndX=23.2 EndY=36.5 EndZ=0
    g25: LineSegment StartX=23.2 StartY=36.5 StartZ=0 EndX=23.2 EndY=21.5 EndZ=0
    g26: LineSegment StartX=23.2 StartY=21.5 StartZ=0 EndX=-31.8 EndY=21.5 EndZ=0
    g27: LineSegment StartX=-31.8 StartY=21.5 StartZ=0 EndX=-31.8 EndY=36.5 EndZ=0
    g28: GeomPoint [constr] X=-1.05 Y=23.5 Z=0
    g29: GeomPoint [constr] X=-1.05 Y=23.5 Z=0
    g30: GeomPoint [constr] X=0 Y=22.45 Z=0
    g31: GeomPoint [constr] X=11.7 Y=22.65 Z=0
    g32: GeomPoint [constr] X=13.25 Y=24.2 Z=0
    g33: GeomPoint [constr] X=-13.25 Y=33.8 Z=0
    g34: GeomPoint [constr] X=-11.7 Y=35.35 Z=0
    g35: GeomPoint [constr] X=23.2 Y=29 Z=0
    g36: GeomPoint [constr] X=0 Y=35.55 Z=0
    g37: LineSegment [constr] StartX=0 StartY=34.5 StartZ=0 EndX=0 EndY=36.5 EndZ=0
    g38: LineSegment [constr] StartX=0 StartY=23.5 StartZ=0 EndX=0 EndY=21.5 EndZ=0
  constraints (99):
    c: Coincident(g0,g1)
    c: Coincident(g1,g2)
    c: Coincident(g2,g3)
    c: Coincident(g3,g0)
    c: Horizontal(g1)
    c: Horizontal(g3)
    c: Vertical(g0)
    c: Vertical(g2)
    c: Symmetric(g1,g0,g4)
    c: Coincident(g5,g6)
    c: Coincident(g6,g7)
    c: Coincident(g7,g8)
    c: Coincident(g8,g5)
    c: Horizontal(g6)
    c: Horizontal(g8)
    c: Vertical(g5)
    c: Vertical(g7)
    c: Symmetric(g6,g5,g9)
    c: Coincident(g10,g11)
    c: Coincident(g11,g12)
    c: Coincident(g12,g13)
    c: Coincident(g13,g10)
    c: Horizontal(g11)
    c: Horizontal(g13)
    c: Vertical(g10)
    c: Vertical(g12)
    c: Symmetric(g11,g10,g14)
    c: Coincident(g15,g16)
    c: Coincident(g16,g17)
    c: Coincident(g17,g18)
    c: Coincident(g18,g15)
    c: Horizontal(g16)
    c: Horizontal(g18)
    c: Vertical(g15)
    c: Vertical(g17)
    c: Symmetric(g16,g15,g19)
    c: Equal(g0,g5)
    c: Equal(g5,g10)
    c: Equal(g10,g15)
    c: Equal(g3,g8)
    c: Equal(g8,g13)
    c: Equal(g13,g18)
    c: Equal(g3,g0)
    c: DistanceX(g1,g1) = 5
    c: Horizontal(g0,g5)
    c: Horizontal(g5,g10)
    c: Horizontal(g10,g15)
    c: PointOnObject(g22,g-2)
    c: PointOnObject(g23,g-2)
    c: Coincident(g24,g25)
    c: Coincident(g25,g26)
    c: Coincident(g26,g27)
    c: Coincident(g27,g24)
    c: Horizontal(g24)
    c: Horizontal(g26)
    c: Vertical(g25)
    c: Vertical(g27)
    c: DistanceY(g27,g27) = 15
    c: PointOnObject(g28,g22)
    c: Equal(g22,g23)
    c: Diameter(g22) = 2.1
    c: Equal(g20,g21)
    c: Diameter(g20) = 3.1
    c: Horizontal(g22,g28)
    c: PointOnObject(g29,g22)
    c: Horizontal(g22,g29)
    c: PointOnObject(g30,g22)
    c: PointOnObject(g30,g-2)
    c: PointOnObject(g31,g21)
    c: PointOnObject(g32,g21)
    c: Vertical(g21,g31)
    c: Horizontal(g21,g32)
    c: Distance(g31,g26) = 1.15
    c: Distance(g32,g25) = 9.95
    c: PointOnObject(g33,g20)
    c: PointOnObject(g34,g20)
    c: Horizontal(g20,g33)
    c: Vertical(g20,g34)
    c: Distance(g33,g27) = 18.55
    c: Distance(g34,g24) = 1.15
    c: Distance(g4,g27) = 14.4
    c: Symmetric(g25,g25,g35)
    c: Horizontal(g19,g35)
    c: PointOnObject(g36,g-2)
    c: PointOnObject(g36,g23)
    c: Distance(g-3,g26) = 3
    c: DistanceX(g4,g9) = 11.6
    c: DistanceX(g9,g14) = 11.6
    c: DistanceX(g14,g19) = 11.6
    c: DistanceY(g22,g23) = 11
    c: DistanceX(g24,g24) = 55
    c: DistanceX(g26,g22) = 31.8
    c: Coincident(g37,g23)
    c: PointOnObject(g37,g24)
    c: Coincident(g38,g22)
    c: PointOnObject(g38,g26)
    c: Vertical(g38)
    c: Vertical(g37)
    c: Equal(g37,g38)
FEATURE [PartDesign::SubShapeBinder] Binder001  label="Binder001(SketchSwitchPlate)"
  BindCopyOnChange = 0
  BindMode = 0
  ClaimChildren = false
  Context = -> LinkGroup [Body.Binder001.]
  FillStyle = 0
  Fuse = false
  MakeFace = false
  OffsetFill = false
  OffsetIntersection = false
  OffsetJoinType = 0
  OffsetOpenResult = false
  PartialLoad = false
  Relative = true
  Support = -> [Sketch012]
  TreeRank = 202
  _Version = 8
FEATURE [PartDesign::SubShapeBinder] Binder002  label="Binder002(SketchFrame)"
  BindCopyOnChange = 0
  BindMode = 0
  ClaimChildren = false
  Context = -> LinkGroup [Body.Binder002.]
  FillStyle = 0
  Fuse = false
  MakeFace = false
  OffsetFill = false
  OffsetIntersection = false
  OffsetJoinType = 0
  OffsetOpenResult = false
  PartialLoad = false
  Relative = true
  Support = -> [Sketch006]
  TreeRank = 203
  _Version = 8
FEATURE [PartDesign::SubShapeBinder] Binder003  label="Binder003(SketchPCB)"
  BindCopyOnChange = 0
  BindMode = 0
  ClaimChildren = false
  Context = -> LinkGroup [Body.Binder003.]
  FillStyle = 0
  Fuse = false
  MakeFace = false
  OffsetFill = false
  OffsetIntersection = false
  OffsetJoinType = 0
  OffsetOpenResult = false
  PartialLoad = false
  Relative = true
  Support = -> [Sketch009]
  TreeRank = 204
  _Version = 8
FEATURE [PartDesign::SubShapeBinder] Binder004  label="Binder004(SketchSwitches)"
  BindCopyOnChange = 0
  BindMode = 0
  ClaimChildren = false
  Context = -> LinkGroup [Body.Binder004.]
  FillStyle = 0
  Fuse = false
  MakeFace = false
  OffsetFill = false
  OffsetIntersection = false
  OffsetJoinType = 0
  OffsetOpenResult = false
  PartialLoad = false
  Relative = true
  Support = -> [Sketch011]
  TreeRank = 205
  _Version = 8
FEATURE [PartDesign::SubShapeBinder] Binder005  label="Binder005(SketchLED)"
  BindCopyOnChange = 0
  BindMode = 0
  ClaimChildren = false
  Context = -> LinkGroup [Body.Binder005.]
  FillStyle = 0
  Fuse = false
  MakeFace = false
  OffsetFill = false
  OffsetIntersection = false
  OffsetJoinType = 0
  OffsetOpenResult = false
  PartialLoad = false
  Relative = true
  Support = -> [Sketch014]
  TreeRank = 206
  _Version = 8
FEATURE [Sketcher::SketchObject] Sketch
  ArcFitTolerance = 0
  AttachmentSupport = -> [XY_Plane]
  ExternalBSplineMaxDegree = 0
  ExternalBSplineTolerance = 0
  ExternalGeometry = -> [Binder001,Binder002,Binder003,Binder004,Binder005]
  FullyConstrained = true
  MapMode = 5
  Support = -> [XY_Plane]
  TreeRank = 21
  sketch-geometry (7):
    g0: ArcOfCircle CenterX=-11.7 CenterY=33.8 CenterZ=0 NormalX=0 NormalY=0 NormalZ=1 AngleXU=0 Radius=4.55 StartAngle=0.15446 EndAngle=2.98713
    g1: LineSegment [constr] StartX=-11.7 StartY=33.8 StartZ=0 EndX=-16.1958 EndY=34.5 EndZ=0
    g2: GeomPoint [constr] X=-13.2315 Y=34.0385 Z=0
    g3: LineSegment StartX=-16.1958 StartY=34.5 StartZ=0 EndX=-29 EndY=34.5 EndZ=0
    g4: LineSegment StartX=-29 StartY=62.5 StartZ=0 EndX=-29 EndY=34.5 EndZ=0
    g5: LineSegment StartX=-7.20417 StartY=34.5 StartZ=0 EndX=29 EndY=34.5 EndZ=0
    g6: LineSegment StartX=29 StartY=34.5 StartZ=0 EndX=29 EndY=62.5 EndZ=0
  constraints (18):
    c: Coincident(g0,g-161)
    c: Coincident(g1,g0)
    c: Coincident(g1,g0)
    c: PointOnObject(g2,g-161)
    c: PointOnObject(g2,g1)
    c: Distance(g0,g2) = 3
    c: Coincident(g3,g0)
    c: PointOnObject(g3,g-12)
    c: Horizontal(g3)
    c: Distance(g-145,g3) = 3
    c: Coincident(g4,g-12)
    c: Coincident(g4,g3)
    c: Coincident(g5,g0)
    c: PointOnObject(g5,g-14)
    c: Horizontal(g5)
    c: Horizontal(g0,g0)
    c: Coincident(g6,g5)
    c: Coincident(g6,g-15)
FEATURE [PartDesign::SubShapeBinder] Binder006  label="Binder006(SketchFrame)"
  BindCopyOnChange = 0
  BindMode = 0
  ClaimChildren = false
  Context = -> Body001 [Binder006.]
  FillStyle = 0
  Fuse = false
  MakeFace = false
  OffsetFill = false
  OffsetIntersection = false
  OffsetJoinType = 0
  OffsetOpenResult = false
  PartialLoad = false
  Relative = true
  Support = -> [Sketch006]
  TreeRank = 207
  _Version = 8
FEATURE [PartDesign::SubShapeBinder] Binder007  label="Binder007(SketchSwitches)"
  BindCopyOnChange = 0
  BindMode = 0
  ClaimChildren = false
  Context = -> Body001 [Binder007.]
  FillStyle = 0
  Fuse = false
  MakeFace = false
  OffsetFill = false
  OffsetIntersection = false
  OffsetJoinType = 0
  OffsetOpenResult = false
  PartialLoad = false
  Relative = true
  Support = -> [Sketch011]
  TreeRank = 208
  _Version = 8
FEATURE [PartDesign::SubShapeBinder] Binder008  label="Binder008(SketchLED)"
  BindCopyOnChange = 0
  BindMode = 0
  ClaimChildren = false
  Context = -> Body001 [Binder008.]
  FillStyle = 0
  Fuse = false
  MakeFace = false
  OffsetFill = false
  OffsetIntersection = false
  OffsetJoinType = 0
  OffsetOpenResult = false
  PartialLoad = false
  Relative = true
  Support = -> [Sketch014]
  TreeRank = 209
  _Version = 8
FEATURE [PartDesign::SubShapeBinder] Binder009  label="Binder009(SketchFrame)"
  BindCopyOnChange = 0
  BindMode = 0
  ClaimChildren = false
  Context = -> Body002 [Binder009.]
  FillStyle = 0
  Fuse = false
  MakeFace = false
  OffsetFill = false
  OffsetIntersection = false
  OffsetJoinType = 0
  OffsetOpenResult = false
  PartialLoad = false
  Relative = true
  Support = -> [Sketch006]
  TreeRank = 210
  _Version = 8
FEATURE [Sketcher::SketchObject] Sketch002
  ArcFitTolerance = 0
  AttachmentSupport = -> [XY_Plane002]
  ExternalBSplineMaxDegree = 0
  ExternalBSplineTolerance = 0
  ExternalGeometry = -> [Binder009]
  FullyConstrained = true
  MapMode = 5
  Support = -> [XY_Plane002]
  TreeRank = 49
  sketch-geometry (6):
    g0: Circle CenterX=-125 CenterY=72.5 CenterZ=0 NormalX=0 NormalY=0 NormalZ=1 AngleXU=0 Radius=1.55
    g1: Circle CenterX=-125 CenterY=-72.5 CenterZ=0 NormalX=0 NormalY=0 NormalZ=1 AngleXU=0 Radius=1.55
    g2: Circle CenterX=125 CenterY=72.5 CenterZ=0 NormalX=0 NormalY=0 NormalZ=1 AngleXU=0 Radius=1.55
    g3: Circle CenterX=125 CenterY=-72.5 CenterZ=0 NormalX=0 NormalY=0 NormalZ=1 AngleXU=0 Radius=1.55
    g4: Circle CenterX=-125 CenterY=0 CenterZ=0 NormalX=0 NormalY=0 NormalZ=1 AngleXU=0 Radius=1.55
    g5: Circle CenterX=125 CenterY=0 CenterZ=0 NormalX=0 NormalY=0 NormalZ=1 AngleXU=0 Radius=1.55
  constraints (14):
    c: Equal(g0,g1)
    c: Equal(g1,g2)
    c: Equal(g2,g3)
    c: Diameter(g0) = 3.1
    c: Symmetric(g-4,g-8,g0)
    c: Symmetric(g-6,g-10,g1)
    c: Symmetric(g-5,g-9,g2)
    c: Symmetric(g-6,g-10,g3)
    c: PointOnObject(g4,g-1)
    c: PointOnObject(g5,g-1)
    c: Equal(g0,g4)
    c: Equal(g4,g5)
    c: Vertical(g4,g0)
    c: Vertical(g2,g5)
FEATURE [PartDesign::Pad] Pad002
  AddSubType = 0
  AlongSketchNormal = false
  CheckUpToFaceLimits = true
  ClaimChildren = false
  Direction = (0,0,1)
  Fit = 0
  FitJoin = 0
  InnerFit = 0
  InnerFitJoin = 0
  InnerTaperAngle = 0
  InnerTaperAngleRev = 0
  Length = 1.5
  Length2 = 100
  Linearize = true
  Midplane = true
  NewSolid = false
  Profile = -> Sketch002
  Suppress = false
  TreeRank = 50
  Type = 0
  _ProfileBasedVersion = 1
FEATURE [PartDesign::Fillet] Fillet001
  AddSubType = 0
  Base = -> Pad002 [Edge2,Edge1,Edge5,Edge8]
  BaseFeature = -> Pad002
  NewSolid = false
  Radius = 1
  SupportTransform = false
  Suppress = false
  TreeRank = 51
FEATURE [PartDesign::Body] Body002  label="BottomPanel"
  AutoGroupSolids = false
  ClaimAllChildren = false
  ExportMode = 0
  Group = -> [Sketch002,Binder009,Pad002,Fillet001]
  Origin = -> Origin002
  Tip = -> Fillet001
  TreeRank = 48
  _ExportChildren = -> [Binder009,Pad002,Fillet001]
  _GroupVersion = 1
FEATURE [PartDesign::SubShapeBinder] Binder010  label="Binder010(Sketch002)"
  BindCopyOnChange = 0
  BindMode = 0
  ClaimChildren = false
  Context = -> Body007 [Binder010.]
  FillStyle = 0
  Fuse = false
  MakeFace = false
  OffsetFill = false
  OffsetIntersection = false
  OffsetJoinType = 0
  OffsetOpenResult = false
  PartialLoad = false
  Relative = true
  Support = -> [Body002[Sketch002.]]
  TreeRank = 211
  _Version = 8
FEATURE [Sketcher::SketchObject] Sketch013
  ArcFitTolerance = 0
  AttachmentSupport = -> [XY_Plane007]
  ExternalBSplineMaxDegree = 0
  ExternalBSplineTolerance = 0
  ExternalGeometry = -> [Binder010]
  FullyConstrained = true
  MapMode = 5
  Support = -> [XY_Plane007]
  TreeRank = 197
  sketch-geometry (12):
    g0: Circle CenterX=-125 CenterY=72.5 CenterZ=0 NormalX=0 NormalY=0 NormalZ=1 AngleXU=0 Radius=4
    g1: Circle CenterX=-125 CenterY=-72.5 CenterZ=0 NormalX=0 NormalY=0 NormalZ=1 AngleXU=0 Radius=4
    g2: Circle CenterX=125 CenterY=72.5 CenterZ=0 NormalX=0 NormalY=0 NormalZ=1 AngleXU=0 Radius=4
    g3: Circle CenterX=125 CenterY=-72.5 CenterZ=0 NormalX=0 NormalY=0 NormalZ=1 AngleXU=0 Radius=4
    g4: GeomPoint [constr] X=-129 Y=72.5 Z=0
    g5: LineSegment StartX=-133 StartY=80.5 StartZ=0 EndX=-133 EndY=-80.5 EndZ=0
    g6: LineSegment StartX=-133 StartY=-80.5 StartZ=0 EndX=133 EndY=-80.5 EndZ=0
    g7: LineSegment StartX=133 StartY=-80.5 StartZ=0 EndX=133 EndY=80.5 EndZ=0
    g8: LineSegment StartX=133 StartY=80.5 StartZ=0 EndX=-133 EndY=80.5 EndZ=0
    g9: GeomPoint [constr] X=0 Y=0 Z=0
    g10: Circle CenterX=-125 CenterY=0 CenterZ=0 NormalX=0 NormalY=0 NormalZ=1 AngleXU=0 Radius=4
    g11: Circle CenterX=125 CenterY=0 CenterZ=0 NormalX=0 NormalY=0 NormalZ=1 AngleXU=0 Radius=4
  constraints (26):
    c: Coincident(g0,g-7)
    c: Equal(g0,g1)
    c: Equal(g1,g2)
    c: Equal(g2,g3)
    c: Coincident(g1,g-8)
    c: Coincident(g2,g-9)
    c: Coincident(g3,g-10)
    c: PointOnObject(g4,g0)
    c: Horizontal(g0,g4)
    c: Coincident(g5,g6)
    c: Coincident(g6,g7)
    c: Coincident(g7,g8)
    c: Coincident(g8,g5)
    c: Horizontal(g6)
    c: Horizontal(g8)
    c: Vertical(g5)
    c: Vertical(g7)
    c: Symmetric(g6,g5,g9)
    c: Coincident(g9,g-1)
    c: Distance(g5,g-3) = 2
    c: Distance(g5,g-4) = 2
    c: Distance(g4,g5) = 4
    c: Coincident(g10,g-11)
    c: Coincident(g11,g-12)
    c: Equal(g10,g11)
    c: Equal(g11,g0)
FEATURE [PartDesign::Pad] Pad011
  AddSubType = 0
  AlongSketchNormal = false
  CheckUpToFaceLimits = true
  ClaimChildren = false
  Direction = (0,0,1)
  Fit = 0
  FitJoin = 0
  InnerFit = 0
  InnerFitJoin = 0
  InnerTaperAngle = 0
  InnerTaperAngleRev = 0
  Length = 2
  Length2 = 100
  Linearize = true
  Midplane = true
  NewSolid = false
  Profile = -> Sketch013
  Suppress = false
  TreeRank = 198
  Type = 0
  _ProfileBasedVersion = 1
FEATURE [PartDesign::Fillet] Fillet014
  AddSubType = 0
  Base = -> Pad011 [Edge2,Edge1,Edge8,Edge5]
  BaseFeature = -> Pad011
  NewSolid = false
  Radius = 3
  SupportTransform = false
  Suppress = false
  TreeRank = 199
FEATURE [PartDesign::Body] Body007  label="BottomFoam"
  AutoGroupSolids = false
  ClaimAllChildren = false
  ExportMode = 0
  Group = -> [Sketch013,Binder010,Pad011,Fillet014]
  Origin = -> Origin007
  Tip = -> Fillet014
  TreeRank = 194
  _ExportChildren = -> [Binder010,Pad011,Fillet014]
  _GroupVersion = 1
FEATURE [Spreadsheet::Sheet] Spreadsheet
  PythonMode = false
  ShowCells = 0
  TreeRank = 10
FEATURE [Sketcher::SketchObject] Sketch015
  ArcFitTolerance = 0
  AttachmentSupport = -> [XZ_Plane008]
  ExternalBSplineMaxDegree = 0
  ExternalBSplineTolerance = 0
  FullyConstrained = true
  MapMode = 5
  Placement = pos=(0,0,0) rot=(1,0,0;1.5708rad)
  Support = -> [XZ_Plane008]
  TreeRank = 222
  expr: Constraints[10] = Sketch004.Constraints[10]
  expr: Constraints[11] = Sketch004.Constraints[11]
  expr: Constraints[14] = Sketch004.Constraints[14]
  expr: Constraints[16] = Sketch004.Constraints[16]
  expr: Constraints[24] = Sketch004.Constraints[24]
  expr: Constraints[27] = Sketch004.Constraints[27]
  expr: Constraints[36] = Sketch004.Constraints[36]
  expr: Constraints[42] = Sketch004.Constraints[42]
  expr: Constraints[44] = Sketch004.Constraints[44]
  expr: Constraints[45] = Sketch004.Constraints[45]
  expr: Constraints[54] = Sketch004.Constraints[54]
  expr: Constraints[57] = Sketch004.Constraints[57]
  expr: Constraints[63] = Sketch004.Constraints[63]
  expr: Constraints[72] = Sketch004.Constraints[72]
  expr: Constraints[73] = Sketch004.Constraints[73]
  expr: Constraints[75] = Sketch004.Constraints[75]
  sketch-geometry (29):
    g0: LineSegment StartX=-20 StartY=10 StartZ=0 EndX=-20 EndY=-7 EndZ=0
    g1: LineSegment StartX=-20 StartY=-10 StartZ=0 EndX=20 EndY=-10 EndZ=0
    g2: LineSegment StartX=20 StartY=-10 StartZ=0 EndX=20 EndY=6.5 EndZ=0
    g3: LineSegment StartX=20 StartY=10 StartZ=0 EndX=-20 EndY=10 EndZ=0
    g4: GeomPoint [constr] X=0 Y=0 Z=0
    g5: LineSegment StartX=-15 StartY=8.5 StartZ=0 EndX=18.134 EndY=8.5 EndZ=0
    g6: LineSegment StartX=-15 StartY=7 StartZ=0 EndX=-15 EndY=7.7 EndZ=0
    g7: Circle CenterX=0 CenterY=0 CenterZ=0 NormalX=0 NormalY=0 NormalZ=1 AngleXU=0 Radius=1.55
    g8: GeomPoint [constr] X=15 Y=7 Z=0
    g9: LineSegment [constr] StartX=-20 StartY=10 StartZ=0 EndX=-20 EndY=14.5 EndZ=0
    g10: LineSegment [constr] StartX=-20 StartY=14.5 StartZ=0 EndX=20 EndY=14.5 EndZ=0
    g11: LineSegment [constr] StartX=20 StartY=14.5 StartZ=0 EndX=20 EndY=10 EndZ=0
    g12: LineSegment StartX=20 StartY=9 StartZ=0 EndX=20 EndY=10 EndZ=0
    g13: LineSegment [constr] StartX=20 StartY=-10 StartZ=0 EndX=20 EndY=-14.5 EndZ=0
    g14: LineSegment [constr] StartX=20 StartY=-14.5 StartZ=0 EndX=-20 EndY=-14.5 EndZ=0
    g15: LineSegment [constr] StartX=-20 StartY=-14.5 StartZ=0 EndX=-20 EndY=-10 EndZ=0
    g16: LineSegment [constr] StartX=-20 StartY=-7 StartZ=0 EndX=15 EndY=-7 EndZ=0
    g17: LineSegment [constr] StartX=15 StartY=-7 StartZ=0 EndX=15 EndY=-8.5 EndZ=0
    g18: LineSegment [constr] StartX=15 StartY=-8.5 StartZ=0 EndX=-20 EndY=-8.5 EndZ=0
    g19: GeomPoint [constr] X=-15 Y=-7 Z=0
    g20: LineSegment StartX=-20 StartY=-8.5 StartZ=0 EndX=-20 EndY=-10 EndZ=0
    g21: LineSegment StartX=-20 StartY=-8.5 StartZ=0 EndX=-20 EndY=-7 EndZ=0
    g22: ArcOfCircle CenterX=-15 CenterY=8.1 CenterZ=0 NormalX=0 NormalY=0 NormalZ=1 AngleXU=0 Radius=0.4 StartAngle=1.5708 EndAngle=4.71239
    g23: LineSegment StartX=18.134 StartY=8.5 StartZ=0 EndX=20 EndY=9 EndZ=0
    g24: LineSegment StartX=18.134 StartY=7 StartZ=0 EndX=20 EndY=6.5 EndZ=0
    g25: LineSegment StartX=18.134 StartY=7 StartZ=0 EndX=-14.2 EndY=7 EndZ=0
    g26: LineSegment [constr] StartX=-14.2 StartY=7 StartZ=0 EndX=-15 EndY=7 EndZ=0
    g27: ArcOfCircle CenterX=-14.6 CenterY=7 CenterZ=0 NormalX=0 NormalY=0 NormalZ=1 AngleXU=0 Radius=0.4 StartAngle=3.14159 EndAngle=6.28319
    g28: Circle [constr] CenterX=0 CenterY=0 CenterZ=0 NormalX=0 NormalY=0 NormalZ=1 AngleXU=0 Radius=3.5
  constraints (76):
    c: Coincident(g20,g1)
    c: Coincident(g1,g2)
    c: Coincident(g12,g3)
    c: Coincident(g3,g0)
    c: Horizontal(g1)
    c: Horizontal(g3)
    c: Vertical(g0)
    c: Vertical(g2)
    c: Symmetric(g1,g0,g4)
    c: Coincident(g4,g-1)
    c: DistanceX(g1,g1) = 40
    c: DistanceY(g20,g0) = 20
    c: Horizontal(g5)
    c: Vertical(g6)
    c: DistanceY(g26,g5) = 1.5
    c: Symmetric(g26,g8,g-2)
    c: DistanceX(g26,g8) = 30
    c: Coincident(g9,g0)
    c: Vertical(g9)
    c: Coincident(g10,g9)
    c: Horizontal(g10)
    c: Coincident(g11,g10)
    c: Coincident(g11,g12)
    c: Vertical(g11)
    c: DistanceY(g9,g9) = 4.5
    c: Distance(g9,g5) = 6
    c: Coincident(g7,g4)
    c: Diameter(g7) = 3.1
    c: Vertical(g12)
    c: Coincident(g13,g14)
    c: Coincident(g14,g15)
    c: Horizontal(g14)
    c: Vertical(g13)
    c: Vertical(g15)
    c: Coincident(g15,g20)
    c: Coincident(g13,g1)
    c: DistanceY(g15,g15) = 4.5
    c: Coincident(g16,g17)
    c: Coincident(g17,g18)
    c: Horizontal(g16)
    c: Horizontal(g18)
    c: Vertical(g17)
    c: DistanceY(g17,g17) = 1.5
    c: Symmetric(g19,g16,g-2)
    c: Distance(g19,g16) = 30
    c: Distance(g14,g18) = 6
    c: Coincident(g0,g16)
    c: Coincident(g20,g18)
    c: Vertical(g20)
    c: Coincident(g21,g18)
    c: Coincident(g21,g0)
    c: Vertical(g21)
    c: PointOnObject(g22,g6)
    c: Coincident(g22,g5)
    c: Diameter(g22) = 0.8
    c: Coincident(g6,g22)
    c: Vertical(g5,g6)
    c: Angle(g23,g5) = 2.87979
    c: Vertical(g23,g24)
    c: Coincident(g25,g24)
    c: Coincident(g2,g24)
    c: Coincident(g5,g23)
    c: Coincident(g12,g23)
    c: DistanceY(g2,g12) = 2.5
    c: Vertical(g2,g12)
    c: Coincident(g25,g26)
    c: Horizontal(g25)
    c: Horizontal(g26)
    c: PointOnObject(g27,g26)
    c: Coincident(g27,g25)
    c: Coincident(g27,g26)
    c: Coincident(g27,g6)
    c: Diameter(g27) = 0.8
    c: Angle(g25,g24) = 2.87979
    c: Coincident(g28,g7)
    c: Diameter(g28) = 7
FEATURE [PartDesign::Pad] Pad012
  AddSubType = 0
  AlongSketchNormal = false
  CheckUpToFaceLimits = true
  ClaimChildren = false
  Direction = (0,-1,2e-16)
  Fit = 0
  FitJoin = 0
  InnerFit = 0
  InnerFitJoin = 0
  InnerTaperAngle = 0
  InnerTaperAngleRev = 0
  Length = 1.5
  Length2 = 100
  Linearize = true
  Midplane = true
  NewSolid = false
  Placement = pos=(0,0,0) rot=(1,0,0;1.5708rad)
  Profile = -> Sketch015
  Refine = true
  Suppress = false
  TreeRank = 223
  Type = 0
  _ProfileBasedVersion = 1
FEATURE [PartDesign::Fillet] Fillet016
  AddSubType = 0
  Base = -> Pad012 [Edge14,Edge27,Edge5,Edge8]
  BaseFeature = -> Pad012
  NewSolid = false
  Placement = pos=(0,0,0) rot=(1,0,0;1.5708rad)
  Radius = 0.4
  SupportTransform = false
  Suppress = false
  TreeRank = 224
FEATURE [PartDesign::Fillet] Fillet017
  AddSubType = 0
  Base = -> Fillet016 [Edge43,Edge45,Edge47,Edge49,Edge50,Edge3]
  BaseFeature = -> Fillet016
  NewSolid = false
  Placement = pos=(0,0,0) rot=(1,0,0;1.5708rad)
  Radius = 1
  SupportTransform = false
  Suppress = false
  TreeRank = 225
FEATURE [PartDesign::Body] Body008  label="Spacer_Choc"
  AutoGroupSolids = false
  ClaimAllChildren = false
  ExportMode = 0
  Group = -> [Sketch015,Pad012,Fillet016,Fillet017]
  Origin = -> Origin008
  Tip = -> Fillet017
  TreeRank = 146
  _ExportChildren = -> [Pad012,Fillet016,Fillet017]
  _GroupVersion = 1
FEATURE [Sketcher::SketchObject] Sketch016
  ArcFitTolerance = 0
  AttachmentSupport = -> [XZ_Plane009]
  ExternalBSplineMaxDegree = 0
  ExternalBSplineTolerance = 0
  FullyConstrained = true
  MapMode = 5
  Placement = pos=(0,0,0) rot=(1,0,0;1.5708rad)
  Support = -> [XZ_Plane009]
  TreeRank = 235
  expr: Constraints[15] = Sketch005.Constraints[15]
  expr: Constraints[26] = Sketch005.Constraints[26]
  expr: Constraints[27] = Sketch005.Constraints[27]
  expr: Constraints[35] = Sketch005.Constraints[35]
  expr: Constraints[38] = Sketch005.Constraints[38]
  expr: Constraints[41] = Sketch005.Constraints[41]
  expr: Constraints[51] = Sketch005.Constraints[51]
  expr: Constraints[59] = Sketch005.Constraints[59]
  expr: Constraints[60] = Sketch005.Constraints[60]
  expr: Constraints[70] = Sketch005.Constraints[70]
  expr: Constraints[71] = Sketch005.Constraints[71]
  expr: Constraints[72] = Sketch005.Constraints[72]
  expr: Constraints[81] = Sketch005.Constraints[81]
  expr: Constraints[83] = Sketch005.Constraints[83]
  sketch-geometry (36):
    g0: LineSegment StartX=-15 StartY=10 StartZ=0 EndX=15 EndY=10 EndZ=0
    g1: LineSegment StartX=15 StartY=10 StartZ=0 EndX=15 EndY=8.5 EndZ=0
    g2: LineSegment StartX=-15 StartY=8.5 StartZ=0 EndX=-15 EndY=10 EndZ=0
    g3: LineSegment StartX=-15 StartY=8.5 StartZ=0 EndX=-6 EndY=8.5 EndZ=0
    g4: LineSegment StartX=15 StartY=8.5 StartZ=0 EndX=6 EndY=8.5 EndZ=0
    g5: LineSegment [constr] StartX=-5 StartY=8.5 StartZ=0 EndX=-5 EndY=-8.13397 EndZ=0
    g6: LineSegment StartX=-4.5 StartY=-10 StartZ=0 EndX=-2.05 EndY=-10 EndZ=0
    g7: LineSegment StartX=-1.55 StartY=-8.13397 StartZ=0 EndX=-1.55 EndY=6.95 EndZ=0
    g8: LineSegment StartX=1.55 StartY=6.95 StartZ=0 EndX=1.55 EndY=-8.13397 EndZ=0
    g9: LineSegment StartX=2.05 StartY=-10 StartZ=0 EndX=4.5 EndY=-10 EndZ=0
    g10: LineSegment [constr] StartX=5 StartY=-8.13397 StartZ=0 EndX=5 EndY=8.5 EndZ=0
    g11: LineSegment [constr] StartX=-20 StartY=10 StartZ=0 EndX=-20 EndY=-10 EndZ=0
    g12: LineSegment [constr] StartX=-20 StartY=-10 StartZ=0 EndX=20 EndY=-10 EndZ=0
    g13: LineSegment [constr] StartX=20 StartY=-10 StartZ=0 EndX=20 EndY=10 EndZ=0
    g14: LineSegment [constr] StartX=20 StartY=10 StartZ=0 EndX=-20 EndY=10 EndZ=0
    g15: GeomPoint [constr] X=0 Y=0 Z=0
    g16: LineSegment [constr] StartX=-20 StartY=10 StartZ=0 EndX=-20 EndY=14.5 EndZ=0
    g17: LineSegment [constr] StartX=-20 StartY=14.5 StartZ=0 EndX=20 EndY=14.5 EndZ=0
    g18: LineSegment [constr] StartX=20 StartY=14.5 StartZ=0 EndX=20 EndY=10 EndZ=0
    g19: ArcOfCircle [constr] CenterX=-5.5 CenterY=8.5 CenterZ=0 NormalX=0 NormalY=0 NormalZ=1 AngleXU=0 Radius=0.5 StartAngle=0 EndAngle=3.14159
    g20: ArcOfCircle [constr] CenterX=5.5 CenterY=8.5 CenterZ=0 NormalX=0 NormalY=0 NormalZ=1 AngleXU=0 Radius=0.5 StartAngle=0 EndAngle=3.14159
    g21: ArcOfCircle CenterX=0 CenterY=6.95 CenterZ=0 NormalX=0 NormalY=0 NormalZ=1 AngleXU=0 Radius=1.55 StartAngle=0 EndAngle=3.14159
    g22: GeomPoint [constr] X=0 Y=8.5 Z=0
    g23: LineSegment StartX=-1.55 StartY=-8.13397 StartZ=0 EndX=-2.05 EndY=-10 EndZ=0
    g24: LineSegment StartX=1.55 StartY=-8.13397 StartZ=0 EndX=2.05 EndY=-10 EndZ=0
    g25: LineSegment [constr] StartX=-1.55 StartY=-8.13397 StartZ=0 EndX=-1.55 EndY=-10 EndZ=0
    g26: LineSegment StartX=-5 StartY=-8.13397 StartZ=0 EndX=-4.5 EndY=-10 EndZ=0
    g27: LineSegment StartX=5 StartY=-8.13397 StartZ=0 EndX=4.5 EndY=-10 EndZ=0
    g28: Circle [constr] CenterX=0 CenterY=0 CenterZ=0 NormalX=0 NormalY=0 NormalZ=1 AngleXU=0 Radius=3.5
    g29: Circle [constr] CenterX=0 CenterY=0 CenterZ=0 NormalX=0 NormalY=0 NormalZ=1 AngleXU=0 Radius=1.55
    g30: LineSegment StartX=-6 StartY=8.5 StartZ=0 EndX=-5 EndY=8.5 EndZ=0
    g31: LineSegment StartX=6 StartY=8.5 StartZ=0 EndX=5 EndY=8.5 EndZ=0
    g32: ArcOfCircle CenterX=-5 CenterY=8 CenterZ=0 NormalX=0 NormalY=0 NormalZ=1 AngleXU=0 Radius=0.5 StartAngle=4.71239 EndAngle=7.85398
    g33: ArcOfCircle CenterX=5 CenterY=8 CenterZ=0 NormalX=0 NormalY=0 NormalZ=1 AngleXU=0 Radius=0.5 StartAngle=1.5708 EndAngle=4.71239
    g34: LineSegment StartX=-5 StartY=7.5 StartZ=0 EndX=-5 EndY=-8.13397 EndZ=0
    g35: LineSegment StartX=5 StartY=7.5 StartZ=0 EndX=5 EndY=-8.13397 EndZ=0
  constraints (101):
    c: Coincident(g0,g1)
    c: Coincident(g2,g0)
    c: Vertical(g1)
    c: Vertical(g2)
    c: Symmetric(g0,g0,g-2)
    c: Coincident(g3,g2)
    c: Horizontal(g3)
    c: Coincident(g4,g1)
    c: Horizontal(g4)
    c: Vertical(g5)
    c: Horizontal(g6)
    c: Vertical(g7)
    c: Vertical(g8)
    c: Horizontal(g9)
    c: Vertical(g10)
    c: DistanceX(g2,g1) = 30
    c: Coincident(g11,g12)
    c: Coincident(g12,g13)
    c: Coincident(g13,g14)
    c: Coincident(g14,g11)
    c: Horizontal(g12)
    c: Horizontal(g14)
    c: Vertical(g11)
    c: Vertical(g13)
    c: Symmetric(g12,g11,g15)
    c: Coincident(g15,g-1)
    c: DistanceY(g13,g13) = 20
    c: DistanceX(g12,g12) = 40
    c: Coincident(g11,g16)
    c: Vertical(g16)
    c: Coincident(g16,g17)
    c: Horizontal(g17)
    c: Coincident(g17,g18)
    c: Vertical(g18)
    c: Coincident(g18,g13)
    c: DistanceY(g16,g16) = 4.5
    c: Distance(g2,g17) = 6
    c: PointOnObject(g0,g14)
    c: DistanceX(g3,g5) = 10
    c: PointOnObject(g19,g3)
    c: Coincident(g19,g5)
    c: Diameter(g19) = 1
    c: Coincident(g3,g19)
    c: Horizontal(g3,g5)
    c: PointOnObject(g20,g4)
    c: Coincident(g20,g10)
    c: Equal(g19,g20)
    c: Coincident(g4,g20)
    c: Symmetric(g5,g10,g-2)
    c: Horizontal(g10,g4)
    c: PointOnObject(g21,g-2)
    c: Diameter(g21) = 3.1
    c: Coincident(g7,g21)
    c: Coincident(g8,g21)
    c: Horizontal(g7,g21)
    c: Horizontal(g21,g8)
    c: PointOnObject(g22,g21)
    c: PointOnObject(g22,g-2)
    c: Horizontal(g5,g22)
    c: Angle(g7,g23) = 2.87979
    c: Angle(g24,g8) = 2.87979
    c: Equal(g23,g24)
    c: Coincident(g6,g23)
    c: Coincident(g7,g23)
    c: Coincident(g8,g24)
    c: Coincident(g9,g24)
    c: Coincident(g25,g7)
    c: PointOnObject(g25,g12)
    c: Vertical(g25)
    c: Horizontal(g6,g9)
    c: DistanceX(g6,g25) = 0.5
    c: Angle(g26,g5) = 2.87979
    c: Angle(g10,g27) = 2.87979
    c: Horizontal(g26,g7)
    c: Horizontal(g27,g8)
    c: Coincident(g5,g26)
    c: Coincident(g6,g26)
    c: Coincident(g10,g27)
    c: Coincident(g9,g27)
    c: PointOnObject(g6,g12)
    c: Coincident(g28,g15)
    c: Diameter(g28) = 7
    c: Coincident(g29,g15)
    c: Diameter(g29) = 3.1
    c: Coincident(g30,g3)
    c: Coincident(g30,g5)
    c: Coincident(g31,g4)
    c: Coincident(g31,g10)
    c: PointOnObject(g32,g5)
    c: Coincident(g32,g5)
    c: PointOnObject(g32,g5)
    c: Equal(g32,g19)
    c: PointOnObject(g33,g10)
    c: Coincident(g33,g10)
    c: PointOnObject(g33,g10)
    c: Equal(g20,g33)
    c: Horizontal(g30)
    c: Coincident(g34,g32)
    c: Coincident(g34,g26)
    c: Coincident(g35,g33)
    c: Coincident(g35,g27)
FEATURE [PartDesign::Pad] Pad013
  AddSubType = 0
  AlongSketchNormal = false
  CheckUpToFaceLimits = true
  ClaimChildren = false
  Direction = (0,-1,2e-16)
  Fit = 0
  FitJoin = 0
  InnerFit = 0
  InnerFitJoin = 0
  InnerTaperAngle = 0
  InnerTaperAngleRev = 0
  Length = 1.5
  Length2 = 100
  Linearize = true
  Midplane = true
  NewSolid = false
  Placement = pos=(0,0,0) rot=(1,0,0;1.5708rad)
  Profile = -> Sketch016
  Refine = true
  Suppress = false
  TreeRank = 236
  Type = 0
  _ProfileBasedVersion = 1
FEATURE [PartDesign::Fillet] Fillet018
  AddSubType = 0
  Base = -> Pad013 [Edge47,Edge46,Edge49,Edge51]
  BaseFeature = -> Pad013
  NewSolid = false
  Placement = pos=(0,0,0) rot=(1,0,0;1.5708rad)
  Radius = 0.4
  SupportTransform = false
  Suppress = false
  TreeRank = 237
FEATURE [PartDesign::Fillet] Fillet019
  AddSubType = 0
  Base = -> Fillet018 [Edge28,Edge32,Edge36,Edge40,Edge44,Edge56,Edge60,Edge64,Edge62,Edge58]
  BaseFeature = -> Fillet018
  NewSolid = false
  Placement = pos=(0,0,0) rot=(1,0,0;1.5708rad)
  Radius = 1
  SupportTransform = false
  Suppress = false
  TreeRank = 238
FEATURE [PartDesign::Body] Body009  label="Retainer_Choc"
  AutoGroupSolids = false
  ClaimAllChildren = false
  ExportMode = 0
  Group = -> [Sketch016,Pad013,Fillet018,Fillet019]
  Origin = -> Origin009
  Tip = -> Fillet019
  TreeRank = 192
  _ExportChildren = -> [Pad013,Fillet018,Fillet019]
  _GroupVersion = 1
FEATURE [Sketcher::SketchObject] Sketch017
  ArcFitTolerance = 0
  AttachmentSupport = -> [XZ_Plane010]
  ExternalBSplineMaxDegree = 0
  ExternalBSplineTolerance = 0
  FullyConstrained = true
  MapMode = 5
  Placement = pos=(0,0,0) rot=(1,0,0;1.5708rad)
  Support = -> [XZ_Plane010]
  TreeRank = 248
  expr: Constraints[10] = Sketch004.Constraints[10]
  expr: Constraints[14] = Sketch004.Constraints[14]
  expr: Constraints[16] = Sketch004.Constraints[16]
  expr: Constraints[24] = Sketch004.Constraints[24]
  expr: Constraints[25] = Sketch004.Constraints[25]
  expr: Constraints[27] = Sketch004.Constraints[27]
  expr: Constraints[36] = Sketch004.Constraints[36]
  expr: Constraints[42] = Sketch004.Constraints[42]
  expr: Constraints[44] = Sketch004.Constraints[44]
  expr: Constraints[45] = Sketch004.Constraints[45]
  expr: Constraints[54] = Sketch004.Constraints[54]
  expr: Constraints[57] = Sketch004.Constraints[57]
  expr: Constraints[63] = Sketch004.Constraints[63]
  expr: Constraints[72] = Sketch004.Constraints[72]
  expr: Constraints[73] = Sketch004.Constraints[73]
  expr: Constraints[75] = Sketch004.Constraints[75]
  sketch-geometry (33):
    g0: LineSegment StartX=-20 StartY=20 StartZ=0 EndX=-20 EndY=-17 EndZ=0
    g1: LineSegment StartX=-20 StartY=-20 StartZ=0 EndX=20 EndY=-20 EndZ=0
    g2: LineSegment StartX=20 StartY=-20 StartZ=0 EndX=20 EndY=14 EndZ=0
    g3: LineSegment StartX=20 StartY=20 StartZ=0 EndX=-20 EndY=20 EndZ=0
    g4: GeomPoint [constr] X=0 Y=0 Z=0
    g5: LineSegment StartX=-15 StartY=16 StartZ=0 EndX=18.134 EndY=16 EndZ=0
    g6: LineSegment StartX=-15 StartY=14.5 StartZ=0 EndX=-15 EndY=15.2 EndZ=0
    g7: Circle [constr] CenterX=0 CenterY=0 CenterZ=0 NormalX=0 NormalY=0 NormalZ=1 AngleXU=0 Radius=1.55
    g8: GeomPoint [constr] X=15 Y=14.5 Z=0
    g9: LineSegment [constr] StartX=-20 StartY=20 StartZ=0 EndX=-20 EndY=24.5 EndZ=0
    g10: LineSegment [constr] StartX=-20 StartY=24.5 StartZ=0 EndX=20 EndY=24.5 EndZ=0
    g11: LineSegment [constr] StartX=20 StartY=24.5 StartZ=0 EndX=20 EndY=20 EndZ=0
    g12: LineSegment StartX=20 StartY=16.5 StartZ=0 EndX=20 EndY=20 EndZ=0
    g13: LineSegment [constr] StartX=20 StartY=-20 StartZ=0 EndX=20 EndY=-24.5 EndZ=0
    g14: LineSegment [constr] StartX=20 StartY=-24.5 StartZ=0 EndX=-20 EndY=-24.5 EndZ=0
    g15: LineSegment [constr] StartX=-20 StartY=-24.5 StartZ=0 EndX=-20 EndY=-20 EndZ=0
    g16: LineSegment [constr] StartX=-20 StartY=-17 StartZ=0 EndX=15 EndY=-17 EndZ=0
    g17: LineSegment [constr] StartX=15 StartY=-17 StartZ=0 EndX=15 EndY=-18.5 EndZ=0
    g18: LineSegment [constr] StartX=15 StartY=-18.5 StartZ=0 EndX=-20 EndY=-18.5 EndZ=0
    g19: GeomPoint [constr] X=-15 Y=-17 Z=0
    g20: LineSegment StartX=-20 StartY=-18.5 StartZ=0 EndX=-20 EndY=-20 EndZ=0
    g21: LineSegment StartX=-20 StartY=-18.5 StartZ=0 EndX=-20 EndY=-17 EndZ=0
    g22: ArcOfCircle CenterX=-15 CenterY=15.6 CenterZ=0 NormalX=0 NormalY=0 NormalZ=1 AngleXU=0 Radius=0.4 StartAngle=1.5708 EndAngle=4.71239
    g23: LineSegment StartX=18.134 StartY=16 StartZ=0 EndX=20 EndY=16.5 EndZ=0
    g24: LineSegment StartX=18.134 StartY=14.5 StartZ=0 EndX=20 EndY=14 EndZ=0
    g25: LineSegment StartX=18.134 StartY=14.5 StartZ=0 EndX=-14.2 EndY=14.5 EndZ=0
    g26: LineSegment [constr] StartX=-14.2 StartY=14.5 StartZ=0 EndX=-15 EndY=14.5 EndZ=0
    g27: ArcOfCircle CenterX=-14.6 CenterY=14.5 CenterZ=0 NormalX=0 NormalY=0 NormalZ=1 AngleXU=0 Radius=0.4 StartAngle=3.14159 EndAngle=6.28319
    g28: Circle [constr] CenterX=0 CenterY=0 CenterZ=0 NormalX=0 NormalY=0 NormalZ=1 AngleXU=0 Radius=3.5
    g29: Circle CenterX=0 CenterY=10 CenterZ=0 NormalX=0 NormalY=0 NormalZ=1 AngleXU=0 Radius=1.55
    g30: Circle CenterX=0 CenterY=-10 CenterZ=0 NormalX=0 NormalY=0 NormalZ=1 AngleXU=0 Radius=1.55
    g31: Circle [constr] CenterX=0 CenterY=10 CenterZ=0 NormalX=0 NormalY=0 NormalZ=1 AngleXU=0 Radius=3.5
    g32: Circle [constr] CenterX=0 CenterY=-10 CenterZ=0 NormalX=0 NormalY=0 NormalZ=1 AngleXU=0 Radius=3.5
  constraints (85):
    c: Coincident(g20,g1)
    c: Coincident(g1,g2)
    c: Coincident(g12,g3)
    c: Coincident(g3,g0)
    c: Horizontal(g1)
    c: Horizontal(g3)
    c: Vertical(g0)
    c: Vertical(g2)
    c: Symmetric(g1,g0,g4)
    c: Coincident(g4,g-1)
    c: DistanceX(g1,g1) = 40
    c: DistanceY(g20,g0) = 40
    c: Horizontal(g5)
    c: Vertical(g6)
    c: DistanceY(g26,g5) = 1.5
    c: Symmetric(g26,g8,g-2)
    c: DistanceX(g26,g8) = 30
    c: Coincident(g9,g0)
    c: Vertical(g9)
    c: Coincident(g10,g9)
    c: Horizontal(g10)
    c: Coincident(g11,g10)
    c: Coincident(g11,g12)
    c: Vertical(g11)
    c: DistanceY(g9,g9) = 4.5
    c: Distance(g9,g5) = 8.5
    c: Coincident(g7,g4)
    c: Diameter(g7) = 3.1
    c: Vertical(g12)
    c: Coincident(g13,g14)
    c: Coincident(g14,g15)
    c: Horizontal(g14)
    c: Vertical(g13)
    c: Vertical(g15)
    c: Coincident(g15,g20)
    c: Coincident(g13,g1)
    c: DistanceY(g15,g15) = 4.5
    c: Coincident(g16,g17)
    c: Coincident(g17,g18)
    c: Horizontal(g16)
    c: Horizontal(g18)
    c: Vertical(g17)
    c: DistanceY(g17,g17) = 1.5
    c: Symmetric(g19,g16,g-2)
    c: Distance(g19,g16) = 30
    c: Distance(g14,g18) = 6
    c: Coincident(g0,g16)
    c: Coincident(g20,g18)
    c: Vertical(g20)
    c: Coincident(g21,g18)
    c: Coincident(g21,g0)
    c: Vertical(g21)
    c: PointOnObject(g22,g6)
    c: Coincident(g22,g5)
    c: Diameter(g22) = 0.8
    c: Coincident(g6,g22)
    c: Vertical(g5,g6)
    c: Angle(g23,g5) = 2.87979
    c: Vertical(g23,g24)
    c: Coincident(g25,g24)
    c: Coincident(g2,g24)
    c: Coincident(g5,g23)
    c: Coincident(g12,g23)
    c: DistanceY(g2,g12) = 2.5
    c: Vertical(g2,g12)
    c: Coincident(g25,g26)
    c: Horizontal(g25)
    c: Horizontal(g26)
    c: PointOnObject(g27,g26)
    c: Coincident(g27,g25)
    c: Coincident(g27,g26)
    c: Coincident(g27,g6)
    c: Diameter(g27) = 0.8
    c: Angle(g25,g24) = 2.87979
    c: Coincident(g28,g7)
    c: Diameter(g28) = 7
    c: PointOnObject(g29,g-2)
    c: Equal(g7,g29)
    c: Equal(g29,g30)
    c: Symmetric(g29,g30,g-1)
    c: DistanceY(g30,g29) = 20
    c: Coincident(g31,g29)
    c: Coincident(g32,g30)
    c: Equal(g28,g31)
    c: Equal(g31,g32)
FEATURE [PartDesign::Pad] Pad014
  AddSubType = 0
  AlongSketchNormal = false
  CheckUpToFaceLimits = true
  ClaimChildren = false
  Direction = (0,-1,2e-16)
  Fit = 0
  FitJoin = 0
  InnerFit = 0
  InnerFitJoin = 0
  InnerTaperAngle = 0
  InnerTaperAngleRev = 0
  Length = 1.5
  Length2 = 100
  Linearize = true
  Midplane = true
  NewSolid = false
  Placement = pos=(0,0,0) rot=(1,0,0;1.5708rad)
  Profile = -> Sketch017
  Refine = true
  Suppress = false
  TreeRank = 249
  Type = 0
  _ProfileBasedVersion = 1
FEATURE [PartDesign::Fillet] Fillet020
  AddSubType = 0
  Base = -> Pad014 [Edge14,Edge27]
  BaseFeature = -> Pad014
  NewSolid = false
  Placement = pos=(0,0,0) rot=(1,0,0;1.5708rad)
  Radius = 0.4
  SupportTransform = false
  Suppress = false
  TreeRank = 250
FEATURE [PartDesign::Fillet] Fillet021
  AddSubType = 0
  Base = -> Fillet020 [Edge44,Edge43,Edge42,Edge40,Edge38,Edge22,Edge46,Edge45]
  BaseFeature = -> Fillet020
  NewSolid = false
  Placement = pos=(0,0,0) rot=(1,0,0;1.5708rad)
  Radius = 1
  SupportTransform = false
  Suppress = false
  TreeRank = 251
FEATURE [PartDesign::Body] Body010  label="Spacer_Lever"
  AutoGroupSolids = false
  ClaimAllChildren = false
  ExportMode = 0
  Group = -> [Sketch017,Pad014,Fillet020,Fillet021]
  Origin = -> Origin010
  Tip = -> Fillet021
  TreeRank = 147
  _ExportChildren = -> [Pad014,Fillet020,Fillet021]
  _GroupVersion = 1
FEATURE [Sketcher::SketchObject] Sketch018
  ArcFitTolerance = 0
  AttachmentSupport = -> [XZ_Plane011]
  ExternalBSplineMaxDegree = 0
  ExternalBSplineTolerance = 0
  FullyConstrained = true
  MapMode = 5
  Placement = pos=(0,0,0) rot=(1,0,0;1.5708rad)
  Support = -> [XZ_Plane011]
  TreeRank = 261
  expr: Constraints[15] = Sketch005.Constraints[15]
  expr: Constraints[27] = Sketch005.Constraints[27]
  expr: Constraints[35] = Sketch005.Constraints[35]
  expr: Constraints[36] = Sketch005.Constraints[36]
  expr: Constraints[38] = Sketch005.Constraints[38]
  expr: Constraints[41] = Sketch005.Constraints[41]
  expr: Constraints[51] = Sketch005.Constraints[51]
  expr: Constraints[59] = Sketch005.Constraints[59]
  expr: Constraints[60] = Sketch005.Constraints[60]
  expr: Constraints[70] = Sketch005.Constraints[70]
  expr: Constraints[71] = Sketch005.Constraints[71]
  expr: Constraints[72] = Sketch005.Constraints[72]
  expr: Constraints[81] = Sketch005.Constraints[81]
  expr: Constraints[83] = Sketch005.Constraints[83]
  sketch-geometry (34):
    g0: LineSegment StartX=-15 StartY=20 StartZ=0 EndX=15 EndY=20 EndZ=0
    g1: LineSegment StartX=15 StartY=20 StartZ=0 EndX=15 EndY=16 EndZ=0
    g2: LineSegment StartX=-15 StartY=16 StartZ=0 EndX=-15 EndY=20 EndZ=0
    g3: LineSegment StartX=-15 StartY=16 StartZ=0 EndX=-6 EndY=16 EndZ=0
    g4: LineSegment StartX=15 StartY=16 StartZ=0 EndX=6 EndY=16 EndZ=0
    g5: LineSegment StartX=-5 StartY=16 StartZ=0 EndX=-5 EndY=-18.134 EndZ=0
    g6: LineSegment StartX=-4.5 StartY=-20 StartZ=0 EndX=-2.05 EndY=-20 EndZ=0
    g7: LineSegment StartX=-1.55 StartY=-18.134 StartZ=0 EndX=-1.55 EndY=14.45 EndZ=0
    g8: LineSegment StartX=1.55 StartY=14.45 StartZ=0 EndX=1.55 EndY=-18.134 EndZ=0
    g9: LineSegment StartX=2.05 StartY=-20 StartZ=0 EndX=4.5 EndY=-20 EndZ=0
    g10: LineSegment StartX=5 StartY=-18.134 StartZ=0 EndX=5 EndY=16 EndZ=0
    g11: LineSegment [constr] StartX=-20 StartY=20 StartZ=0 EndX=-20 EndY=-20 EndZ=0
    g12: LineSegment [constr] StartX=-20 StartY=-20 StartZ=0 EndX=20 EndY=-20 EndZ=0
    g13: LineSegment [constr] StartX=20 StartY=-20 StartZ=0 EndX=20 EndY=20 EndZ=0
    g14: LineSegment [constr] StartX=20 StartY=20 StartZ=0 EndX=-20 EndY=20 EndZ=0
    g15: GeomPoint [constr] X=0 Y=0 Z=0
    g16: LineSegment [constr] StartX=-20 StartY=20 StartZ=0 EndX=-20 EndY=24.5 EndZ=0
    g17: LineSegment [constr] StartX=-20 StartY=24.5 StartZ=0 EndX=20 EndY=24.5 EndZ=0
    g18: LineSegment [constr] StartX=20 StartY=24.5 StartZ=0 EndX=20 EndY=20 EndZ=0
    g19: ArcOfCircle CenterX=-5.5 CenterY=16 CenterZ=0 NormalX=0 NormalY=0 NormalZ=1 AngleXU=0 Radius=0.5 StartAngle=-9e-16 EndAngle=3.14159
    g20: ArcOfCircle CenterX=5.5 CenterY=16 CenterZ=0 NormalX=0 NormalY=0 NormalZ=1 AngleXU=0 Radius=0.5 StartAngle=-4.4e-15 EndAngle=3.14159
    g21: ArcOfCircle CenterX=0 CenterY=14.45 CenterZ=0 NormalX=0 NormalY=0 NormalZ=1 AngleXU=0 Radius=1.55 StartAngle=0 EndAngle=3.14159
    g22: GeomPoint [constr] X=0 Y=16 Z=0
    g23: LineSegment StartX=-1.55 StartY=-18.134 StartZ=0 EndX=-2.05 EndY=-20 EndZ=0
    g24: LineSegment StartX=1.55 StartY=-18.134 StartZ=0 EndX=2.05 EndY=-20 EndZ=0
    g25: LineSegment [constr] StartX=-1.55 StartY=-18.134 StartZ=0 EndX=-1.55 EndY=-20 EndZ=0
    g26: LineSegment StartX=-5 StartY=-18.134 StartZ=0 EndX=-4.5 EndY=-20 EndZ=0
    g27: LineSegment StartX=5 StartY=-18.134 StartZ=0 EndX=4.5 EndY=-20 EndZ=0
    g28: Circle [constr] CenterX=0 CenterY=0 CenterZ=0 NormalX=0 NormalY=0 NormalZ=1 AngleXU=0 Radius=3.5
    g29: Circle [constr] CenterX=0 CenterY=0 CenterZ=0 NormalX=0 NormalY=0 NormalZ=1 AngleXU=0 Radius=1.55
    g30: Circle [constr] CenterX=0 CenterY=10 CenterZ=0 NormalX=0 NormalY=0 NormalZ=1 AngleXU=0 Radius=1.55
    g31: Circle [constr] CenterX=0 CenterY=10 CenterZ=0 NormalX=0 NormalY=0 NormalZ=1 AngleXU=0 Radius=3.5
    g32: Circle [constr] CenterX=0 CenterY=-10 CenterZ=0 NormalX=0 NormalY=0 NormalZ=1 AngleXU=0 Radius=1.55
    g33: Circle [constr] CenterX=0 CenterY=-10 CenterZ=0 NormalX=0 NormalY=0 NormalZ=1 AngleXU=0 Radius=3.5
  constraints (93):
    c: Coincident(g0,g1)
    c: Coincident(g2,g0)
    c: Vertical(g1)
    c: Vertical(g2)
    c: Symmetric(g0,g0,g-2)
    c: Coincident(g3,g2)
    c: Horizontal(g3)
    c: Coincident(g4,g1)
    c: Horizontal(g4)
    c: Vertical(g5)
    c: Horizontal(g6)
    c: Vertical(g7)
    c: Vertical(g8)
    c: Horizontal(g9)
    c: Vertical(g10)
    c: DistanceX(g2,g1) = 30
    c: Coincident(g11,g12)
    c: Coincident(g12,g13)
    c: Coincident(g13,g14)
    c: Coincident(g14,g11)
    c: Horizontal(g12)
    c: Horizontal(g14)
    c: Vertical(g11)
    c: Vertical(g13)
    c: Symmetric(g12,g11,g15)
    c: Coincident(g15,g-1)
    c: DistanceY(g13,g13) = 40
    c: DistanceX(g12,g12) = 40
    c: Coincident(g11,g16)
    c: Vertical(g16)
    c: Coincident(g16,g17)
    c: Horizontal(g17)
    c: Coincident(g17,g18)
    c: Vertical(g18)
    c: Coincident(g18,g13)
    c: DistanceY(g16,g16) = 4.5
    c: Distance(g2,g17) = 8.5
    c: PointOnObject(g0,g14)
    c: DistanceX(g3,g5) = 10
    c: PointOnObject(g19,g3)
    c: Coincident(g19,g5)
    c: Diameter(g19) = 1
    c: Coincident(g3,g19)
    c: Horizontal(g3,g5)
    c: PointOnObject(g20,g4)
    c: Coincident(g20,g10)
    c: Equal(g19,g20)
    c: Coincident(g4,g20)
    c: Symmetric(g5,g10,g-2)
    c: Horizontal(g10,g4)
    c: PointOnObject(g21,g-2)
    c: Diameter(g21) = 3.1
    c: Coincident(g7,g21)
    c: Coincident(g8,g21)
    c: Horizontal(g7,g21)
    c: Horizontal(g21,g8)
    c: PointOnObject(g22,g21)
    c: PointOnObject(g22,g-2)
    c: Horizontal(g5,g22)
    c: Angle(g7,g23) = 2.87979
    c: Angle(g24,g8) = 2.87979
    c: Equal(g23,g24)
    c: Coincident(g6,g23)
    c: Coincident(g7,g23)
    c: Coincident(g8,g24)
    c: Coincident(g9,g24)
    c: Coincident(g25,g7)
    c: PointOnObject(g25,g12)
    c: Vertical(g25)
    c: Horizontal(g6,g9)
    c: DistanceX(g6,g25) = 0.5
    c: Angle(g26,g5) = 2.87979
    c: Angle(g10,g27) = 2.87979
    c: Horizontal(g26,g7)
    c: Horizontal(g27,g8)
    c: Coincident(g5,g26)
    c: Coincident(g6,g26)
    c: Coincident(g10,g27)
    c: Coincident(g9,g27)
    c: PointOnObject(g6,g12)
    c: Coincident(g28,g15)
    c: Diameter(g28) = 7
    c: Coincident(g29,g15)
    c: Diameter(g29) = 3.1
    c: PointOnObject(g30,g-2)
    c: Coincident(g31,g30)
    c: Coincident(g33,g32)
    c: Equal(g29,g30)
    c: Equal(g30,g32)
    c: Equal(g28,g31)
    c: Equal(g31,g33)
    c: Symmetric(g30,g32,g-1)
    c: DistanceY(g32,g30) = 20
FEATURE [PartDesign::Pad] Pad015
  AddSubType = 0
  AlongSketchNormal = false
  CheckUpToFaceLimits = true
  ClaimChildren = false
  Direction = (0,-1,2e-16)
  Fit = 0
  FitJoin = 0
  InnerFit = 0
  InnerFitJoin = 0
  InnerTaperAngle = 0
  InnerTaperAngleRev = 0
  Length = 1.5
  Length2 = 100
  Linearize = true
  Midplane = true
  NewSolid = false
  Placement = pos=(0,0,0) rot=(1,0,0;1.5708rad)
  Profile = -> Sketch018
  Refine = true
  Suppress = false
  TreeRank = 262
  Type = 0
  _ProfileBasedVersion = 1
FEATURE [PartDesign::Fillet] Fillet022
  AddSubType = 0
  Base = -> Pad015 [Edge8,Edge5,Edge2,Edge50,Edge47,Edge44,Edge41,Edge32,Edge29,Edge26,Edge23,Edge17,Edge14,Edge11]
  BaseFeature = -> Pad015
  NewSolid = false
  Placement = pos=(0,0,0) rot=(1,0,0;1.5708rad)
  Radius = 1
  SupportTransform = false
  Suppress = false
  TreeRank = 263
FEATURE [PartDesign::Body] Body011  label="Retainer_Lever"
  AutoGroupSolids = false
  ClaimAllChildren = false
  ExportMode = 0
  Group = -> [Sketch018,Pad015,Fillet022]
  Origin = -> Origin011
  Tip = -> Fillet022
  TreeRank = 193
  _ExportChildren = -> [Pad015,Fillet022]
  _GroupVersion = 1
FEATURE [Sketcher::SketchObject] Sketch019
  ArcFitTolerance = 0
  AttachmentSupport = -> [XZ_Plane012]
  ExternalBSplineMaxDegree = 0
  ExternalBSplineTolerance = 0
  FullyConstrained = true
  MapMode = 5
  Placement = pos=(0,0,0) rot=(1,0,0;1.5708rad)
  Support = -> [XZ_Plane012]
  TreeRank = 273
  expr: Constraints[20] = Sketch003.Constraints[20]
  expr: Constraints[21] = Sketch003.Constraints[21]
  expr: Constraints[32] = Sketch003.Constraints[32]
  expr: Constraints[33] = Sketch003.Constraints[33]
  expr: Constraints[51] = Sketch003.Constraints[51]
  expr: Constraints[55] = Sketch003.Constraints[55]
  expr: Constraints[56] = Sketch003.Constraints[56]
  expr: Constraints[67] = Sketch003.Constraints[67]
  expr: Constraints[68] = Sketch003.Constraints[68]
  expr: Constraints[70] = Sketch003.Constraints[70]
  expr: Constraints[77] = Sketch003.Constraints[77]
  expr: Constraints[79] = Sketch003.Constraints[79]
  expr: Constraints[82] = Sketch003.Constraints[82]
  expr: Constraints[83] = Sketch003.Constraints[83]
  sketch-geometry (42):
    g0: LineSegment StartX=-51.5 StartY=20 StartZ=0 EndX=-51.5 EndY=-20 EndZ=0
    g1: LineSegment StartX=-51.5 StartY=-20 StartZ=0 EndX=51.5 EndY=-20 EndZ=0
    g2: LineSegment StartX=51.5 StartY=-20 StartZ=0 EndX=51.5 EndY=20 EndZ=0
    g3: LineSegment StartX=51.5 StartY=20 StartZ=0 EndX=-51.5 EndY=20 EndZ=0
    g4: LineSegment StartX=-6.5 StartY=6.5 StartZ=0 EndX=-6.5 EndY=-6.5 EndZ=0
    g5: LineSegment StartX=-6.5 StartY=-6.5 StartZ=0 EndX=6.5 EndY=-6.5 EndZ=0
    g6: LineSegment StartX=6.5 StartY=-6.5 StartZ=0 EndX=6.5 EndY=6.5 EndZ=0
    g7: LineSegment StartX=6.5 StartY=6.5 StartZ=0 EndX=-6.5 EndY=6.5 EndZ=0
    g8: GeomPoint [constr] X=0 Y=0 Z=0
    g9: LineSegment [constr] StartX=-17.5 StartY=9.5 StartZ=0 EndX=-17.5 EndY=-9.5 EndZ=0
    g10: LineSegment [constr] StartX=-17.5 StartY=-9.5 StartZ=0 EndX=17.5 EndY=-9.5 EndZ=0
    g11: LineSegment [constr] StartX=17.5 StartY=-9.5 StartZ=0 EndX=17.5 EndY=9.5 EndZ=0
    g12: LineSegment [constr] StartX=17.5 StartY=9.5 StartZ=0 EndX=-17.5 EndY=9.5 EndZ=0
    g13: GeomPoint [constr] X=0 Y=0 Z=0
    g14: Circle [constr] CenterX=-47.5 CenterY=0 CenterZ=0 NormalX=0 NormalY=0 NormalZ=1 AngleXU=0 Radius=1.55
    g15: Circle [constr] CenterX=47.5 CenterY=0 CenterZ=0 NormalX=0 NormalY=0 NormalZ=1 AngleXU=0 Radius=1.55
    g16: GeomPoint [constr] X=-49.05 Y=0 Z=0
    g17: ArcOfCircle CenterX=-15 CenterY=0 CenterZ=0 NormalX=0 NormalY=0 NormalZ=1 AngleXU=0 Radius=1.55 StartAngle=1.5708 EndAngle=4.71239
    g18: ArcOfCircle CenterX=-12 CenterY=0 CenterZ=0 NormalX=0 NormalY=0 NormalZ=1 AngleXU=0 Radius=1.55 StartAngle=4.71239 EndAngle=7.85398
    g19: LineSegment StartX=-15 StartY=-1.55 StartZ=0 EndX=-12 EndY=-1.55 EndZ=0
    g20: LineSegment StartX=-12 StartY=1.55 StartZ=0 EndX=-15 EndY=1.55 EndZ=0
    g21: ArcOfCircle CenterX=12 CenterY=0 CenterZ=0 NormalX=0 NormalY=0 NormalZ=1 AngleXU=0 Radius=1.55 StartAngle=1.5708 EndAngle=4.71239
    g22: ArcOfCircle CenterX=15 CenterY=0 CenterZ=0 NormalX=0 NormalY=0 NormalZ=1 AngleXU=0 Radius=1.55 StartAngle=4.71239 EndAngle=7.85398
    g23: LineSegment StartX=12 StartY=-1.55 StartZ=0 EndX=15 EndY=-1.55 EndZ=0
    g24: LineSegment StartX=15 StartY=1.55 StartZ=0 EndX=12 EndY=1.55 EndZ=0
    g25: LineSegment [constr] StartX=-19.5 StartY=7.3 StartZ=0 EndX=-19.5 EndY=-7.3 EndZ=0
    g26: LineSegment [constr] StartX=-19.5 StartY=-7.3 StartZ=0 EndX=19.5 EndY=-7.3 EndZ=0
    g27: LineSegment [constr] StartX=19.5 StartY=-7.3 StartZ=0 EndX=19.5 EndY=7.3 EndZ=0
    g28: LineSegment [constr] StartX=19.5 StartY=7.3 StartZ=0 EndX=-19.5 EndY=7.3 EndZ=0
    g29: GeomPoint [constr] X=0 Y=0 Z=0
    g30: Circle CenterX=33.5 CenterY=0 CenterZ=0 NormalX=0 NormalY=0 NormalZ=1 AngleXU=0 Radius=3.175
    g31: GeomPoint [constr] X=30.325 Y=0 Z=0
    g32: GeomPoint [constr] X=36.675 Y=0 Z=0
    g33: GeomPoint [constr] X=45.95 Y=0 Z=0
    g34: Circle CenterX=-33.5 CenterY=0 CenterZ=0 NormalX=0 NormalY=0 NormalZ=1 AngleXU=0 Radius=4.05
    g35: GeomPoint [constr] X=-49.05 Y=0 Z=0
    g36: LineSegment [constr] StartX=-47.5 StartY=0 StartZ=0 EndX=-19.5 EndY=0 EndZ=0
    g37: LineSegment [constr] StartX=47.5 StartY=0 StartZ=0 EndX=19.5 EndY=0 EndZ=0
    g38: Circle CenterX=-47.5 CenterY=10 CenterZ=0 NormalX=0 NormalY=0 NormalZ=1 AngleXU=0 Radius=1.55
    g39: Circle CenterX=-47.5 CenterY=-10 CenterZ=0 NormalX=0 NormalY=0 NormalZ=1 AngleXU=0 Radius=1.55
    g40: Circle CenterX=47.5 CenterY=10 CenterZ=0 NormalX=0 NormalY=0 NormalZ=1 AngleXU=0 Radius=1.55
    g41: Circle CenterX=47.5 CenterY=-10 CenterZ=0 NormalX=0 NormalY=0 NormalZ=1 AngleXU=0 Radius=1.55
  constraints (101):
    c: Coincident(g0,g1)
    c: Coincident(g1,g2)
    c: Coincident(g3,g0)
    c: Horizontal(g1)
    c: Vertical(g0)
    c: Vertical(g2)
    c: DistanceY(g0,g0) = 40
    c: Horizontal(g3)
    c: Coincident(g3,g2)
    c: Symmetric(g0,g1,g-1)
    c: Coincident(g4,g5)
    c: Coincident(g5,g6)
    c: Coincident(g6,g7)
    c: Coincident(g7,g4)
    c: Horizontal(g5)
    c: Horizontal(g7)
    c: Vertical(g4)
    c: Vertical(g6)
    c: Symmetric(g5,g4,g8)
    c: Coincident(g8,g-1)
    c: DistanceY(g6,g6) = 13
    c: DistanceX(g5,g5) = 13
    c: Coincident(g9,g10)
    c: Coincident(g10,g11)
    c: Coincident(g11,g12)
    c: Coincident(g12,g9)
    c: Horizontal(g10)
    c: Horizontal(g12)
    c: Vertical(g9)
    c: Vertical(g11)
    c: Symmetric(g10,g9,g13)
    c: Coincident(g13,g8)
    c: DistanceX(g10,g10) = 35
    c: DistanceY(g9,g9) = 19
    c: PointOnObject(g14,g-1)
    c: Symmetric(g14,g15,g-2)
    c: Equal(g14,g15)
    c: PointOnObject(g16,g14)
    c: PointOnObject(g16,g-1)
    c: Tangent(g17,g19) = -1.5708
    c: Tangent(g19,g18) = -1.5708
    c: Tangent(g18,g20) = -1.5708
    c: Tangent(g20,g17) = -1.5708
    c: Equal(g17,g18)
    c: PointOnObject(g17,g-1)
    c: PointOnObject(g18,g-1)
    c: Tangent(g21,g23) = -1.5708
    c: Tangent(g23,g22) = -1.5708
    c: Tangent(g22,g24) = -1.5708
    c: Tangent(g24,g21) = -1.5708
    c: Equal(g21,g22)
    c: Diameter(g17) = 3.1
    c: Equal(g17,g21)
    c: Symmetric(g17,g22,g-2)
    c: Symmetric(g18,g21,g-2)
    c: DistanceX(g18,g21) = 24
    c: DistanceX(g17,g22) = 30
    c: Coincident(g25,g26)
    c: Coincident(g26,g27)
    c: Coincident(g27,g28)
    c: Coincident(g28,g25)
    c: Horizontal(g26)
    c: Horizontal(g28)
    c: Vertical(g25)
    c: Vertical(g27)
    c: Symmetric(g26,g25,g29)
    c: Coincident(g29,g8)
    c: DistanceX(g26,g26) = 39
    c: DistanceY(g27,g27) = 14.6
    c: PointOnObject(g30,g-1)
    c: Diameter(g30) = 6.35
    c: PointOnObject(g31,g30)
    c: PointOnObject(g31,g-1)
    c: PointOnObject(g32,g-1)
    c: PointOnObject(g32,g30)
    c: PointOnObject(g33,g15)
    c: PointOnObject(g33,g-1)
    c: Diameter(g14) = 3.1
    c: PointOnObject(g34,g-1)
    c: Diameter(g34) = 8.1
    c: PointOnObject(g35,g14)
    c: PointOnObject(g35,g-1)
    c: Distance(g14,g0) = 4
    c: Distance(g14,g34) = 14
    c: Coincident(g36,g14)
    c: PointOnObject(g36,g25)
    c: Symmetric(g36,g36,g34)
    c: Coincident(g37,g15)
    c: PointOnObject(g37,g27)
    c: Symmetric(g37,g37,g30)
    c: DistanceX(g3,g3) = 103
    c: Equal(g14,g39)
    c: Equal(g39,g38)
    c: Equal(g38,g41)
    c: Equal(g41,g40)
    c: Symmetric(g38,g39,g-1)
    c: Vertical(g14,g38)
    c: DistanceY(g39,g38) = 20
    c: Symmetric(g40,g41,g-1)
    c: Vertical(g40,g15)
    c: DistanceY(g41,g40) = 20
FEATURE [PartDesign::Pad] Pad016
  AddSubType = 0
  AlongSketchNormal = false
  CheckUpToFaceLimits = true
  ClaimChildren = false
  Direction = (0,-1,-2e-16)
  Fit = 0
  FitJoin = 0
  InnerFit = 0
  InnerFitJoin = 0
  InnerTaperAngle = 0
  InnerTaperAngleRev = 0
  Length = 1.5
  Length2 = 100
  Linearize = true
  NewSolid = false
  Placement = pos=(0,0,0) rot=(1,0,0;1.5708rad)
  Profile = -> Sketch019
  Refine = true
  Reversed = true
  Suppress = false
  TreeRank = 274
  Type = 0
  _ProfileBasedVersion = 1
FEATURE [PartDesign::Fillet] Fillet023
  AddSubType = 0
  Base = -> Pad016 [Edge1,Edge8,Edge5,Edge2,Edge14,Edge13,Edge20,Edge17]
  BaseFeature = -> Pad016
  NewSolid = false
  Placement = pos=(0,0,0) rot=(1,0,0;1.5708rad)
  Radius = 1
  SupportTransform = false
  Suppress = false
  TreeRank = 275
FEATURE [PartDesign::Body] Body012  label="JackPanel_Lever"
  AutoGroupSolids = false
  ClaimAllChildren = false
  ExportMode = 0
  Group = -> [Sketch019,Pad016,Fillet023]
  Origin = -> Origin012
  Tip = -> Fillet023
  TreeRank = 131
  _ExportChildren = -> [Pad016,Fillet023]
  _GroupVersion = 1
FEATURE [Sketcher::SketchObject] Sketch020
  ArcFitTolerance = 0
  AttachmentSupport = -> [Sketch]
  ExternalBSplineMaxDegree = 0
  ExternalBSplineTolerance = 0
  ExternalGeometry = -> [Sketch]
  FullyConstrained = true
  MapMode = 5
  Support = -> [Sketch]
  TreeRank = 276
  sketch-geometry (192):
    g0: ArcOfCircle CenterX=-71.9 CenterY=18.4 CenterZ=0 NormalX=0 NormalY=0 NormalZ=1 AngleXU=0 Radius=0.1 StartAngle=1.5708 EndAngle=3.14159
    g1: LineSegment StartX=-71.9 StartY=18.5 StartZ=0 EndX=-58.1 EndY=18.5 EndZ=0
    g2: ArcOfCircle CenterX=-58.1 CenterY=18.4 CenterZ=0 NormalX=0 NormalY=0 NormalZ=1 AngleXU=0 Radius=0.1 StartAngle=-1.03e-13 EndAngle=1.5708
    g3: LineSegment StartX=-58 StartY=18.4 StartZ=0 EndX=-58 EndY=4.6 EndZ=0
    g4: ArcOfCircle CenterX=-58.1 CenterY=4.6 CenterZ=0 NormalX=0 NormalY=0 NormalZ=1 AngleXU=0 Radius=0.1 StartAngle=4.71239 EndAngle=6.28319
    g5: LineSegment StartX=-58.1 StartY=4.5 StartZ=0 EndX=-71.9 EndY=4.5 EndZ=0
    g6: ArcOfCircle CenterX=-71.9 CenterY=4.6 CenterZ=0 NormalX=0 NormalY=0 NormalZ=1 AngleXU=0 Radius=0.1 StartAngle=3.14159 EndAngle=4.71239
    g7: LineSegment StartX=-72 StartY=4.6 StartZ=0 EndX=-72 EndY=18.4 EndZ=0
    g8: GeomPoint [constr] X=-72 Y=18.5 Z=0
    g9: GeomPoint [constr] X=-58 Y=4.5 Z=0
    g10: ArcOfCircle CenterX=-46.9 CenterY=18.4 CenterZ=0 NormalX=0 NormalY=0 NormalZ=1 AngleXU=0 Radius=0.1 StartAngle=1.5708 EndAngle=3.14159
    g11: LineSegment StartX=-46.9 StartY=18.5 StartZ=0 EndX=-33.1 EndY=18.5 EndZ=0
    g12: ArcOfCircle CenterX=-33.1 CenterY=18.4 CenterZ=0 NormalX=0 NormalY=0 NormalZ=1 AngleXU=0 Radius=0.1 StartAngle=-1.021e-13 EndAngle=1.5708
    g13: LineSegment StartX=-33 StartY=18.4 StartZ=0 EndX=-33 EndY=4.6 EndZ=0
    g14: ArcOfCircle CenterX=-33.1 CenterY=4.6 CenterZ=0 NormalX=0 NormalY=0 NormalZ=1 AngleXU=0 Radius=0.1 StartAngle=4.71239 EndAngle=6.28319
    g15: LineSegment StartX=-33.1 StartY=4.5 StartZ=0 EndX=-46.9 EndY=4.5 EndZ=0
    g16: ArcOfCircle CenterX=-46.9 CenterY=4.6 CenterZ=0 NormalX=0 NormalY=0 NormalZ=1 AngleXU=0 Radius=0.1 StartAngle=3.14159 EndAngle=4.71239
    g17: LineSegment StartX=-47 StartY=4.6 StartZ=0 EndX=-47 EndY=18.4 EndZ=0
    g18: GeomPoint [constr] X=-47 Y=18.5 Z=0
    g19: GeomPoint [constr] X=-33 Y=4.5 Z=0
    g20: ArcOfCircle CenterX=-21.9 CenterY=4.4 CenterZ=0 NormalX=0 NormalY=0 NormalZ=1 AngleXU=0 Radius=0.1 StartAngle=1.5708 EndAngle=3.14159
    g21: LineSegment StartX=-21.9 StartY=4.5 StartZ=0 EndX=-8.1 EndY=4.5 EndZ=0
    g22: ArcOfCircle CenterX=-8.1 CenterY=4.4 CenterZ=0 NormalX=0 NormalY=0 NormalZ=1 AngleXU=0 Radius=0.1 StartAngle=-9.59e-14 EndAngle=1.5708
    g23: LineSegment StartX=-8 StartY=4.4 StartZ=0 EndX=-8 EndY=-9.4 EndZ=0
    g24: ArcOfCircle CenterX=-8.1 CenterY=-9.4 CenterZ=0 NormalX=0 NormalY=0 NormalZ=1 AngleXU=0 Radius=0.1 StartAngle=4.71239 EndAngle=6.28319
    g25: LineSegment StartX=-8.1 StartY=-9.5 StartZ=0 EndX=-21.9 EndY=-9.5 EndZ=0
    g26: ArcOfCircle CenterX=-21.9 CenterY=-9.4 CenterZ=0 NormalX=0 NormalY=0 NormalZ=1 AngleXU=0 Radius=0.1 StartAngle=3.14159 EndAngle=4.71239
    g27: LineSegment StartX=-22 StartY=-9.4 StartZ=0 EndX=-22 EndY=4.4 EndZ=0
    g28: GeomPoint [constr] X=-22 Y=4.5 Z=0
    g29: GeomPoint [constr] X=-8 Y=-9.5 Z=0
    g30: ArcOfCircle CenterX=7.1 CenterY=16.9 CenterZ=0 NormalX=0 NormalY=0 NormalZ=1 AngleXU=0 Radius=0.1 StartAngle=1.5708 EndAngle=3.14159
    g31: LineSegment StartX=7.1 StartY=17 StartZ=0 EndX=20.9 EndY=17 EndZ=0
    g32: ArcOfCircle CenterX=20.9 CenterY=16.9 CenterZ=0 NormalX=0 NormalY=0 NormalZ=1 AngleXU=0 Radius=0.1 StartAngle=-1.039e-13 EndAngle=1.5708
    g33: LineSegment StartX=21 StartY=16.9 StartZ=0 EndX=21 EndY=3.1 EndZ=0
    g34: ArcOfCircle CenterX=20.9 CenterY=3.1 CenterZ=0 NormalX=0 NormalY=0 NormalZ=1 AngleXU=0 Radius=0.1 StartAngle=4.71239 EndAngle=6.28319
    g35: LineSegment StartX=20.9 StartY=3 StartZ=0 EndX=7.1 EndY=3 EndZ=0
    g36: ArcOfCircle CenterX=7.1 CenterY=3.1 CenterZ=0 NormalX=0 NormalY=0 NormalZ=1 AngleXU=0 Radius=0.1 StartAngle=3.14159 EndAngle=4.71239
    g37: LineSegment StartX=7 StartY=3.1 StartZ=0 EndX=7 EndY=16.9 EndZ=0
    g38: GeomPoint [constr] X=7 Y=17 Z=0
    g39: GeomPoint [constr] X=21 Y=3 Z=0
    g40: ArcOfCircle CenterX=7.1 CenterY=-8.1 CenterZ=0 NormalX=0 NormalY=0 NormalZ=1 AngleXU=0 Radius=0.1 StartAngle=1.5708 EndAngle=3.14159
    g41: LineSegment StartX=7.1 StartY=-8 StartZ=0 EndX=20.9 EndY=-8 EndZ=0
    g42: ArcOfCircle CenterX=20.9 CenterY=-8.1 CenterZ=0 NormalX=0 NormalY=0 NormalZ=1 AngleXU=0 Radius=0.1 StartAngle=-1.057e-13 EndAngle=1.5708
    g43: LineSegment StartX=21 StartY=-8.1 StartZ=0 EndX=21 EndY=-21.9 EndZ=0
    g44: ArcOfCircle CenterX=20.9 CenterY=-21.9 CenterZ=0 NormalX=0 NormalY=0 NormalZ=1 AngleXU=0 Radius=0.1 StartAngle=4.71239 EndAngle=6.28319
    g45: LineSegment StartX=20.9 StartY=-22 StartZ=0 EndX=7.1 EndY=-22 EndZ=0
    g46: ArcOfCircle CenterX=7.1 CenterY=-21.9 CenterZ=0 NormalX=0 NormalY=0 NormalZ=1 AngleXU=0 Radius=0.1 StartAngle=3.14159 EndAngle=4.71239
    g47: LineSegment StartX=7 StartY=-21.9 StartZ=0 EndX=7 EndY=-8.1 EndZ=0
    g48: GeomPoint [constr] X=7 Y=-8 Z=0
    g49: GeomPoint [constr] X=21 Y=-22 Z=0
    g50: ArcOfCircle CenterX=32.1 CenterY=30.9 CenterZ=0 NormalX=0 NormalY=0 NormalZ=1 AngleXU=0 Radius=0.1 StartAngle=1.5708 EndAngle=3.14159
    g51: LineSegment StartX=32.1 StartY=31 StartZ=0 EndX=45.9 EndY=31 EndZ=0
    g52: ArcOfCircle CenterX=45.9 CenterY=30.9 CenterZ=0 NormalX=0 NormalY=0 NormalZ=1 AngleXU=0 Radius=0.1 StartAngle=-1.057e-13 EndAngle=1.5708
    g53: LineSegment StartX=46 StartY=30.9 StartZ=0 EndX=46 EndY=17.1 EndZ=0
    g54: ArcOfCircle CenterX=45.9 CenterY=17.1 CenterZ=0 NormalX=0 NormalY=0 NormalZ=1 AngleXU=0 Radius=0.1 StartAngle=4.71239 EndAngle=6.28319
    g55: LineSegment StartX=45.9 StartY=17 StartZ=0 EndX=32.1 EndY=17 EndZ=0
    g56: ArcOfCircle CenterX=32.1 CenterY=17.1 CenterZ=0 NormalX=0 NormalY=0 NormalZ=1 AngleXU=0 Radius=0.1 StartAngle=3.14159 EndAngle=4.71239
    g57: LineSegment StartX=32 StartY=17.1 StartZ=0 EndX=32 EndY=30.9 EndZ=0
    g58: GeomPoint [constr] X=32 Y=31 Z=0
    g59: GeomPoint [constr] X=46 Y=17 Z=0
    g60: ArcOfCircle CenterX=32.1 CenterY=5.9 CenterZ=0 NormalX=0 NormalY=0 NormalZ=1 AngleXU=0 Radius=0.1 StartAngle=1.5708 EndAngle=3.14159
    g61: LineSegment StartX=32.1 StartY=6 StartZ=0 EndX=45.9 EndY=6 EndZ=0
    g62: ArcOfCircle CenterX=45.9 CenterY=5.9 CenterZ=0 NormalX=0 NormalY=0 NormalZ=1 AngleXU=0 Radius=0.1 StartAngle=-9.41e-14 EndAngle=1.5708
    g63: LineSegment StartX=46 StartY=5.9 StartZ=0 EndX=46 EndY=-7.9 EndZ=0
    g64: ArcOfCircle CenterX=45.9 CenterY=-7.9 CenterZ=0 NormalX=0 NormalY=0 NormalZ=1 AngleXU=0 Radius=0.1 StartAngle=4.71239 EndAngle=6.28319
    g65: LineSegment StartX=45.9 StartY=-8 StartZ=0 EndX=32.1 EndY=-8 EndZ=0
    g66: ArcOfCircle CenterX=32.1 CenterY=-7.9 CenterZ=0 NormalX=0 NormalY=0 NormalZ=1 AngleXU=0 Radius=0.1 StartAngle=3.14159 EndAngle=4.71239
    g67: LineSegment StartX=32 StartY=-7.9 StartZ=0 EndX=32 EndY=5.9 EndZ=0
    g68: GeomPoint [constr] X=32 Y=6 Z=0
    g69: GeomPoint [constr] X=46 Y=-8 Z=0
    g70: ArcOfCircle CenterX=57.1 CenterY=30.9 CenterZ=0 NormalX=0 NormalY=0 NormalZ=1 AngleXU=0 Radius=0.1 StartAngle=1.5708 EndAngle=3.14159
    g71: LineSegment StartX=57.1 StartY=31 StartZ=0 EndX=70.9 EndY=31 EndZ=0
    g72: ArcOfCircle CenterX=70.9 CenterY=30.9 CenterZ=0 NormalX=0 NormalY=0 NormalZ=1 AngleXU=0 Radius=0.1 StartAngle=-1.039e-13 EndAngle=1.5708
    g73: LineSegment StartX=71 StartY=30.9 StartZ=0 EndX=71 EndY=17.1 EndZ=0
    g74: ArcOfCircle CenterX=70.9 CenterY=17.1 CenterZ=0 NormalX=0 NormalY=0 NormalZ=1 AngleXU=0 Radius=0.1 StartAngle=4.71239 EndAngle=6.28319
    g75: LineSegment StartX=70.9 StartY=17 StartZ=0 EndX=57.1 EndY=17 EndZ=0
    g76: ArcOfCircle CenterX=57.1 CenterY=17.1 CenterZ=0 NormalX=0 NormalY=0 NormalZ=1 AngleXU=0 Radius=0.1 StartAngle=3.14159 EndAngle=4.71239
    g77: LineSegment StartX=57 StartY=17.1 StartZ=0 EndX=57 EndY=30.9 EndZ=0
    g78: GeomPoint [constr] X=57 Y=31 Z=0
    g79: GeomPoint [constr] X=71 Y=17 Z=0
    g80: ArcOfCircle CenterX=57.1 CenterY=5.9 CenterZ=0 NormalX=0 NormalY=0 NormalZ=1 AngleXU=0 Radius=0.1 StartAngle=1.5708 EndAngle=3.14159
    g81: LineSegment StartX=57.1 StartY=6 StartZ=0 EndX=70.9 EndY=6 EndZ=0
    g82: ArcOfCircle CenterX=70.9 CenterY=5.9 CenterZ=0 NormalX=0 NormalY=0 NormalZ=1 AngleXU=0 Radius=0.1 StartAngle=-9.5e-14 EndAngle=1.5708
    g83: LineSegment StartX=71 StartY=5.9 StartZ=0 EndX=71 EndY=-7.9 EndZ=0
    g84: ArcOfCircle CenterX=70.9 CenterY=-7.9 CenterZ=0 NormalX=0 NormalY=0 NormalZ=1 AngleXU=0 Radius=0.1 StartAngle=4.71239 EndAngle=6.28319
    g85: LineSegment StartX=70.9 StartY=-8 StartZ=0 EndX=57.1 EndY=-8 EndZ=0
    g86: ArcOfCircle CenterX=57.1 CenterY=-7.9 CenterZ=0 NormalX=0 NormalY=0 NormalZ=1 AngleXU=0 Radius=0.1 StartAngle=3.14159 EndAngle=4.71239
    g87: LineSegment StartX=57 StartY=-7.9 StartZ=0 EndX=57 EndY=5.9 EndZ=0
    g88: GeomPoint [constr] X=57 Y=6 Z=0
    g89: GeomPoint [constr] X=71 Y=-8 Z=0
    g90: ArcOfCircle CenterX=82.1 CenterY=23.9 CenterZ=0 NormalX=0 NormalY=0 NormalZ=1 AngleXU=0 Radius=0.1 StartAngle=1.5708 EndAngle=3.14159
    g91: LineSegment StartX=82.1 StartY=24 StartZ=0 EndX=95.9 EndY=24 EndZ=0
    g92: ArcOfCircle CenterX=95.9 CenterY=23.9 CenterZ=0 NormalX=0 NormalY=0 NormalZ=1 AngleXU=0 Radius=0.1 StartAngle=-1.039e-13 EndAngle=1.5708
    g93: LineSegment StartX=96 StartY=23.9 StartZ=0 EndX=96 EndY=10.1 EndZ=0
    g94: ArcOfCircle CenterX=95.9 CenterY=10.1 CenterZ=0 NormalX=0 NormalY=0 NormalZ=1 AngleXU=0 Radius=0.1 StartAngle=4.71239 EndAngle=6.28319
    g95: LineSegment StartX=95.9 StartY=10 StartZ=0 EndX=82.1 EndY=10 EndZ=0
    g96: ArcOfCircle CenterX=82.1 CenterY=10.1 CenterZ=0 NormalX=0 NormalY=0 NormalZ=1 AngleXU=0 Radius=0.1 StartAngle=3.14159 EndAngle=4.71239
    g97: LineSegment StartX=82 StartY=10.1 StartZ=0 EndX=82 EndY=23.9 EndZ=0
    g98: GeomPoint [constr] X=82 Y=24 Z=0
    g99: GeomPoint [constr] X=96 Y=10 Z=0
    g100: ArcOfCircle CenterX=82.1 CenterY=-1.1 CenterZ=0 NormalX=0 NormalY=0 NormalZ=1 AngleXU=0 Radius=0.1 StartAngle=1.5708 EndAngle=3.14159
    g101: LineSegment StartX=82.1 StartY=-1 StartZ=0 EndX=95.9 EndY=-1 EndZ=0
    g102: ArcOfCircle CenterX=95.9 CenterY=-1.1 CenterZ=0 NormalX=0 NormalY=0 NormalZ=1 AngleXU=0 Radius=0.1 StartAngle=-9.77e-14 EndAngle=1.5708
    g103: LineSegment StartX=96 StartY=-1.1 StartZ=0 EndX=96 EndY=-14.9 EndZ=0
    g104: ArcOfCircle CenterX=95.9 CenterY=-14.9 CenterZ=0 NormalX=0 NormalY=0 NormalZ=1 AngleXU=0 Radius=0.1 StartAngle=4.71239 EndAngle=6.28319
    g105: LineSegment StartX=95.9 StartY=-15 StartZ=0 EndX=82.1 EndY=-15 EndZ=0
    g106: ArcOfCircle CenterX=82.1 CenterY=-14.9 CenterZ=0 NormalX=0 NormalY=0 NormalZ=1 AngleXU=0 Radius=0.1 StartAngle=3.14159 EndAngle=4.71239
    g107: LineSegment StartX=82 StartY=-14.9 StartZ=0 EndX=82 EndY=-1.1 EndZ=0
    g108: GeomPoint [constr] X=82 Y=-1 Z=0
    g109: GeomPoint [constr] X=96 Y=-15 Z=0
    g110: ArcOfCircle CenterX=-6.9 CenterY=-41.6 CenterZ=0 NormalX=0 NormalY=0 NormalZ=1 AngleXU=0 Radius=0.1 StartAngle=1.5708 EndAngle=3.14159
    g111: LineSegment StartX=-6.9 StartY=-41.5 StartZ=0 EndX=6.9 EndY=-41.5 EndZ=0
    g112: ArcOfCircle CenterX=6.9 CenterY=-41.6 CenterZ=0 NormalX=0 NormalY=0 NormalZ=1 AngleXU=0 Radius=0.1 StartAngle=-9.86e-14 EndAngle=1.5708
    g113: LineSegment StartX=7 StartY=-41.6 StartZ=0 EndX=7 EndY=-55.4 EndZ=0
    g114: ArcOfCircle CenterX=6.9 CenterY=-55.4 CenterZ=0 NormalX=0 NormalY=0 NormalZ=1 AngleXU=0 Radius=0.1 StartAngle=4.71239 EndAngle=6.28319
    g115: LineSegment StartX=6.9 StartY=-55.5 StartZ=0 EndX=-6.9 EndY=-55.5 EndZ=0
    g116: ArcOfCircle CenterX=-6.9 CenterY=-55.4 CenterZ=0 NormalX=0 NormalY=0 NormalZ=1 AngleXU=0 Radius=0.1 StartAngle=3.14159 EndAngle=4.71239
    g117: LineSegment StartX=-7 StartY=-55.4 StartZ=0 EndX=-7 EndY=-41.6 EndZ=0
    g118: GeomPoint [constr] X=-7 Y=-41.5 Z=0
    g119: GeomPoint [constr] X=7 Y=-55.5 Z=0
    g120: ArcOfCircle CenterX=-19.65 CenterY=31.25 CenterZ=0 NormalX=0 NormalY=0 NormalZ=1 AngleXU=0 Radius=0.25 StartAngle=1.5708 EndAngle=3.14159
    g121: LineSegment StartX=-19.65 StartY=31.5 StartZ=0 EndX=-15.15 EndY=31.5 EndZ=0
    g122: ArcOfCircle CenterX=-15.15 CenterY=31.25 CenterZ=0 NormalX=0 NormalY=0 NormalZ=1 AngleXU=0 Radius=0.25 StartAngle=5.9e-15 EndAngle=1.5708
    g123: LineSegment StartX=-14.9 StartY=31.25 StartZ=0 EndX=-14.9 EndY=26.75 EndZ=0
    g124: ArcOfCircle CenterX=-15.15 CenterY=26.75 CenterZ=0 NormalX=0 NormalY=0 NormalZ=1 AngleXU=0 Radius=0.25 StartAngle=4.71239 EndAngle=6.28319
    g125: LineSegment StartX=-15.15 StartY=26.5 StartZ=0 EndX=-19.65 EndY=26.5 EndZ=0
    g126: ArcOfCircle CenterX=-19.65 CenterY=26.75 CenterZ=0 NormalX=0 NormalY=0 NormalZ=1 AngleXU=0 Radius=0.25 StartAngle=3.14159 EndAngle=4.71239
    g127: LineSegment StartX=-19.9 StartY=26.75 StartZ=0 EndX=-19.9 EndY=31.25 EndZ=0
    g128: GeomPoint [constr] X=-19.9 Y=31.5 Z=0
    g129: GeomPoint [constr] X=-14.9 Y=26.5 Z=0
    g130: ArcOfCircle CenterX=-8.05 CenterY=31.25 CenterZ=0 NormalX=0 NormalY=0 NormalZ=1 AngleXU=0 Radius=0.25 StartAngle=1.5708 EndAngle=3.14159
    g131: LineSegment StartX=-8.05 StartY=31.5 StartZ=0 EndX=-3.55 EndY=31.5 EndZ=0
    g132: ArcOfCircle CenterX=-3.55 CenterY=31.25 CenterZ=0 NormalX=0 NormalY=0 NormalZ=1 AngleXU=0 Radius=0.25 StartAngle=7e-16 EndAngle=1.5708
    g133: LineSegment StartX=-3.3 StartY=31.25 StartZ=0 EndX=-3.3 EndY=26.75 EndZ=0
    g134: ArcOfCircle CenterX=-3.55 CenterY=26.75 CenterZ=0 NormalX=0 NormalY=0 NormalZ=1 AngleXU=0 Radius=0.25 StartAngle=4.71239 EndAngle=6.28319
    g135: LineSegment StartX=-3.55 StartY=26.5 StartZ=0 EndX=-8.05 EndY=26.5 EndZ=0
    g136: ArcOfCircle CenterX=-8.05 CenterY=26.75 CenterZ=0 NormalX=0 NormalY=0 NormalZ=1 AngleXU=0 Radius=0.25 StartAngle=3.14159 EndAngle=4.71239
    g137: LineSegment StartX=-8.3 StartY=26.75 StartZ=0 EndX=-8.3 EndY=31.25 EndZ=0
    g138: GeomPoint [constr] X=-8.3 Y=31.5 Z=0
    g139: GeomPoint [constr] X=-3.3 Y=26.5 Z=0
    g140: ArcOfCircle CenterX=3.55 CenterY=31.25 CenterZ=0 NormalX=0 NormalY=0 NormalZ=1 AngleXU=0 Radius=0.25 StartAngle=1.5708 EndAngle=3.14159
    g141: LineSegment StartX=3.55 StartY=31.5 StartZ=0 EndX=8.05 EndY=31.5 EndZ=0
    g142: ArcOfCircle CenterX=8.05 CenterY=31.25 CenterZ=0 NormalX=0 NormalY=0 NormalZ=1 AngleXU=0 Radius=0.25 StartAngle=-6.2e-15 EndAngle=1.5708
    g143: LineSegment StartX=8.3 StartY=31.25 StartZ=0 EndX=8.3 EndY=26.75 EndZ=0
    g144: ArcOfCircle CenterX=8.05 CenterY=26.75 CenterZ=0 NormalX=0 NormalY=0 NormalZ=1 AngleXU=0 Radius=0.25 StartAngle=4.71239 EndAngle=6.28319
    g145: LineSegment StartX=8.05 StartY=26.5 StartZ=0 EndX=3.55 EndY=26.5 EndZ=0
    g146: ArcOfCircle CenterX=3.55 CenterY=26.75 CenterZ=0 NormalX=0 NormalY=0 NormalZ=1 AngleXU=0 Radius=0.25 StartAngle=3.14159 EndAngle=4.71239
    g147: LineSegment StartX=3.3 StartY=26.75 StartZ=0 EndX=3.3 EndY=31.25 EndZ=0
    g148: GeomPoint [constr] X=3.3 Y=31.5 Z=0
    g149: GeomPoint [constr] X=8.3 Y=26.5 Z=0
    g150: ArcOfCircle CenterX=15.15 CenterY=31.25 CenterZ=0 NormalX=0 NormalY=0 NormalZ=1 AngleXU=0 Radius=0.25 StartAngle=1.5708 EndAngle=3.14159
    g151: LineSegment StartX=15.15 StartY=31.5 StartZ=0 EndX=19.65 EndY=31.5 EndZ=0
    g152: ArcOfCircle CenterX=19.65 CenterY=31.25 CenterZ=0 NormalX=0 NormalY=0 NormalZ=1 AngleXU=0 Radius=0.25 StartAngle=6e-15 EndAngle=1.5708
    g153: LineSegment StartX=19.9 StartY=31.25 StartZ=0 EndX=19.9 EndY=26.75 EndZ=0
    g154: ArcOfCircle CenterX=19.65 CenterY=26.75 CenterZ=0 NormalX=0 NormalY=0 NormalZ=1 AngleXU=0 Radius=0.25 StartAngle=4.71239 EndAngle=6.28319
    g155: LineSegment StartX=19.65 StartY=26.5 StartZ=0 EndX=15.15 EndY=26.5 EndZ=0
    g156: ArcOfCircle CenterX=15.15 CenterY=26.75 CenterZ=0 NormalX=0 NormalY=0 NormalZ=1 AngleXU=0 Radius=0.25 StartAngle=3.14159 EndAngle=4.71239
    g157: LineSegment StartX=14.9 StartY=26.75 StartZ=0 EndX=14.9 EndY=31.25 EndZ=0
    g158: GeomPoint [constr] X=14.9 Y=31.5 Z=0
    g159: GeomPoint [constr] X=19.9 Y=26.5 Z=0
    g160: LineSegment StartX=-113.5 StartY=27.5 StartZ=0 EndX=-113.5 EndY=62 EndZ=0
    g161: LineSegment StartX=-29.5 StartY=62.5 StartZ=0 EndX=-113 EndY=62.5 EndZ=0
    g162: ArcOfCircle CenterX=-113 CenterY=62 CenterZ=0 NormalX=0 NormalY=0 NormalZ=1 AngleXU=0 Radius=0.5 StartAngle=1.5708 EndAngle=3.14159
    g163: GeomPoint [constr] X=-113.5 Y=62.5 Z=0
    g164: LineSegment StartX=-29 StartY=62 StartZ=0 EndX=-29 EndY=35 EndZ=0
    g165: LineSegment StartX=-28.5 StartY=34.5 StartZ=0 EndX=-16.6054 EndY=34.5 EndZ=0
    g166: ArcOfCircle CenterX=-29.5 CenterY=62 CenterZ=0 NormalX=0 NormalY=0 NormalZ=1 AngleXU=0 Radius=0.5 StartAngle=3.2e-15 EndAngle=1.5708
    g167: GeomPoint [constr] X=-29 Y=62.5 Z=0
    g168: ArcOfCircle CenterX=-28.5 CenterY=35 CenterZ=0 NormalX=0 NormalY=0 NormalZ=1 AngleXU=0 Radius=0.5 StartAngle=3.14159 EndAngle=4.71239
    g169: GeomPoint [constr] X=-29 Y=34.5 Z=0
    g170: ArcOfCircle CenterX=-11.7 CenterY=33.8 CenterZ=0 NormalX=0 NormalY=0 NormalZ=1 AngleXU=0 Radius=4.55 StartAngle=0.239919 EndAngle=2.90167
    g171: ArcOfCircle CenterX=-16.6054 CenterY=35 CenterZ=0 NormalX=0 NormalY=0 NormalZ=1 AngleXU=0 Radius=0.5 StartAngle=4.71239 EndAngle=6.04327
    g172: LineSegment StartX=-6.79465 StartY=34.5 StartZ=0 EndX=28.5 EndY=34.5 EndZ=0
    g173: LineSegment StartX=29 StartY=35 StartZ=0 EndX=29 EndY=62 EndZ=0
    g174: ArcOfCircle CenterX=-6.79465 CenterY=35 CenterZ=0 NormalX=0 NormalY=0 NormalZ=1 AngleXU=0 Radius=0.5 StartAngle=3.38151 EndAngle=4.71239
    g175: ArcOfCircle CenterX=28.5 CenterY=35 CenterZ=0 NormalX=0 NormalY=0 NormalZ=1 AngleXU=0 Radius=0.5 StartAngle=4.71239 EndAngle=6.28319
    g176: GeomPoint [constr] X=29 Y=34.5 Z=0
    g177: LineSegment StartX=29.5 StartY=62.5 StartZ=0 EndX=113 EndY=62.5 EndZ=0
    g178: ArcOfCircle CenterX=29.5 CenterY=62 CenterZ=0 NormalX=0 NormalY=0 NormalZ=1 AngleXU=0 Radius=0.5 StartAngle=1.5708 EndAngle=3.14159
    g179: GeomPoint [constr] X=29 Y=62.5 Z=0
    g180: LineSegment StartX=113.5 StartY=62 StartZ=0 EndX=113.5 EndY=27.866 EndZ=0
    g181: ArcOfCircle CenterX=113 CenterY=62 CenterZ=0 NormalX=0 NormalY=0 NormalZ=1 AngleXU=0 Radius=0.5 StartAngle=-5.3e-15 EndAngle=1.5708
    g182: GeomPoint [constr] X=113.5 Y=62.5 Z=0
    g183: ArcOfCircle CenterX=113.5 CenterY=27 CenterZ=0 NormalX=0 NormalY=0 NormalZ=1 AngleXU=0 Radius=0.5 StartAngle=2.0944 EndAngle=4.71239
    g184: ArcOfCircle CenterX=113 CenterY=27.866 CenterZ=0 NormalX=0 NormalY=0 NormalZ=1 AngleXU=0 Radius=0.5 StartAngle=5.23599 EndAngle=6.28319
    g185: LineSegment StartX=113.5 StartY=26.5 StartZ=0 EndX=114.5 EndY=26.5 EndZ=0
    g186: LineSegment StartX=115 StartY=26 StartZ=0 EndX=115 EndY=-3 EndZ=0
    g187: ArcOfCircle CenterX=114.5 CenterY=26 CenterZ=0 NormalX=0 NormalY=0 NormalZ=1 AngleXU=0 Radius=0.5 StartAngle=-9e-16 EndAngle=1.5708
    g188: GeomPoint [constr] X=115 Y=26.5 Z=0
    g189: LineSegment StartX=114.5 StartY=-3.5 StartZ=0 EndX=113.5 EndY=-3.5 EndZ=0
    g190: ArcOfCircle CenterX=114.5 CenterY=-3 CenterZ=0 NormalX=0 NormalY=0 NormalZ=1 AngleXU=0 Radius=0.5 StartAngle=4.71239 EndAngle=6.28319
    g191: GeomPoint [constr] X=115 Y=-3.5 Z=0
  constraints (419):
    c: Tangent(g0,g1) = 1.5708
    c: Tangent(g1,g2) = 1.5708
    c: Tangent(g2,g3) = 1.5708
    c: Tangent(g3,g4) = 1.5708
    c: Tangent(g4,g5) = 1.5708
    c: Tangent(g5,g6) = 1.5708
    c: Tangent(g6,g7) = 1.5708
    c: Tangent(g7,g0) = 1.5708
    c: Horizontal(g1)
    c: Horizontal(g5)
    c: Vertical(g3)
    c: Vertical(g7)
    c: Equal(g0,g2)
    c: Equal(g2,g4)
    c: Equal(g4,g6)
    c: PointOnObject(g8,g1)
    c: PointOnObject(g8,g7)
    c: PointOnObject(g9,g3)
    c: PointOnObject(g9,g5)
    c: Coincident(g8,g-61)
    c: Coincident(g9,g-63)
    c: Tangent(g10,g11) = 1.5708
    c: Tangent(g11,g12) = 1.5708
    c: Tangent(g12,g13) = 1.5708
    c: Tangent(g13,g14) = 1.5708
    c: Tangent(g14,g15) = 1.5708
    c: Tangent(g15,g16) = 1.5708
    c: Tangent(g16,g17) = 1.5708
    c: Tangent(g17,g10) = 1.5708
    c: Horizontal(g11)
    c: Horizontal(g15)
    c: Vertical(g13)
    c: Vertical(g17)
    c: Equal(g10,g12)
    c: Equal(g12,g14)
    c: Equal(g14,g16)
    c: PointOnObject(g18,g11)
    c: PointOnObject(g18,g17)
    c: PointOnObject(g19,g13)
    c: PointOnObject(g19,g15)
    c: Coincident(g18,g-65)
    c: Coincident(g19,g-67)
    c: Tangent(g20,g21) = 1.5708
    c: Tangent(g21,g22) = 1.5708
    c: Tangent(g22,g23) = 1.5708
    c: Tangent(g23,g24) = 1.5708
    c: Tangent(g24,g25) = 1.5708
    c: Tangent(g25,g26) = 1.5708
    c: Tangent(g26,g27) = 1.5708
    c: Tangent(g27,g20) = 1.5708
    c: Horizontal(g21)
    c: Horizontal(g25)
    c: Vertical(g23)
    c: Vertical(g27)
    c: Equal(g20,g22)
    c: Equal(g22,g24)
    c: Equal(g24,g26)
    c: PointOnObject(g28,g21)
    c: PointOnObject(g28,g27)
    c: PointOnObject(g29,g23)
    c: PointOnObject(g29,g25)
    c: Coincident(g28,g-69)
    c: Coincident(g29,g-71)
    c: Tangent(g30,g31) = 1.5708
    c: Tangent(g31,g32) = 1.5708
    c: Tangent(g32,g33) = 1.5708
    c: Tangent(g33,g34) = 1.5708
    c: Tangent(g34,g35) = 1.5708
    c: Tangent(g35,g36) = 1.5708
    c: Tangent(g36,g37) = 1.5708
    c: Tangent(g37,g30) = 1.5708
    c: Horizontal(g31)
    c: Horizontal(g35)
    c: Vertical(g33)
    c: Vertical(g37)
    c: Equal(g30,g32)
    c: Equal(g32,g34)
    c: Equal(g34,g36)
    c: PointOnObject(g38,g31)
    c: PointOnObject(g38,g37)
    c: PointOnObject(g39,g33)
    c: PointOnObject(g39,g35)
    c: Coincident(g38,g-77)
    c: Coincident(g39,g-79)
    c: Tangent(g40,g41) = 1.5708
    c: Tangent(g41,g42) = 1.5708
    c: Tangent(g42,g43) = 1.5708
    c: Tangent(g43,g44) = 1.5708
    c: Tangent(g44,g45) = 1.5708
    c: Tangent(g45,g46) = 1.5708
    c: Tangent(g46,g47) = 1.5708
    c: Tangent(g47,g40) = 1.5708
    c: Horizontal(g41)
    c: Horizontal(g45)
    c: Vertical(g43)
    c: Vertical(g47)
    c: Equal(g40,g42)
    c: Equal(g42,g44)
    c: Equal(g44,g46)
    c: PointOnObject(g48,g41)
    c: PointOnObject(g48,g47)
    c: PointOnObject(g49,g43)
    c: PointOnObject(g49,g45)
    c: Coincident(g48,g-81)
    c: Coincident(g49,g-83)
    c: Tangent(g50,g51) = 1.5708
    c: Tangent(g51,g52) = 1.5708
    c: Tangent(g52,g53) = 1.5708
    c: Tangent(g53,g54) = 1.5708
    c: Tangent(g54,g55) = 1.5708
    c: Tangent(g55,g56) = 1.5708
    c: Tangent(g56,g57) = 1.5708
    c: Tangent(g57,g50) = 1.5708
    c: Horizontal(g51)
    c: Horizontal(g55)
    c: Vertical(g53)
    c: Vertical(g57)
    c: Equal(g50,g52)
    c: Equal(g52,g54)
    c: Equal(g54,g56)
    c: PointOnObject(g58,g51)
    c: PointOnObject(g58,g57)
    c: PointOnObject(g59,g53)
    c: PointOnObject(g59,g55)
    c: Coincident(g58,g-85)
    c: Coincident(g59,g-87)
    c: Tangent(g60,g61) = 1.5708
    c: Tangent(g61,g62) = 1.5708
    c: Tangent(g62,g63) = 1.5708
    c: Tangent(g63,g64) = 1.5708
    c: Tangent(g64,g65) = 1.5708
    c: Tangent(g65,g66) = 1.5708
    c: Tangent(g66,g67) = 1.5708
    c: Tangent(g67,g60) = 1.5708
    c: Horizontal(g61)
    c: Horizontal(g65)
    c: Vertical(g63)
    c: Vertical(g67)
    c: Equal(g60,g62)
    c: Equal(g62,g64)
    c: Equal(g64,g66)
    c: PointOnObject(g68,g61)
    c: PointOnObject(g68,g67)
    c: PointOnObject(g69,g63)
    c: PointOnObject(g69,g65)
    c: Coincident(g68,g-89)
    c: Coincident(g69,g-91)
    c: Tangent(g70,g71) = 1.5708
    c: Tangent(g71,g72) = 1.5708
    c: Tangent(g72,g73) = 1.5708
    c: Tangent(g73,g74) = 1.5708
    c: Tangent(g74,g75) = 1.5708
    c: Tangent(g75,g76) = 1.5708
    c: Tangent(g76,g77) = 1.5708
    c: Tangent(g77,g70) = 1.5708
    c: Horizontal(g71)
    c: Horizontal(g75)
    c: Vertical(g73)
    c: Vertical(g77)
    c: Equal(g70,g72)
    c: Equal(g72,g74)
    c: Equal(g74,g76)
    c: PointOnObject(g78,g71)
    c: PointOnObject(g78,g77)
    c: PointOnObject(g79,g73)
    c: PointOnObject(g79,g75)
    c: Coincident(g78,g-93)
    c: Coincident(g79,g-95)
    c: Tangent(g80,g81) = 1.5708
    c: Tangent(g81,g82) = 1.5708
    c: Tangent(g82,g83) = 1.5708
    c: Tangent(g83,g84) = 1.5708
    c: Tangent(g84,g85) = 1.5708
    c: Tangent(g85,g86) = 1.5708
    c: Tangent(g86,g87) = 1.5708
    c: Tangent(g87,g80) = 1.5708
    c: Horizontal(g81)
    c: Horizontal(g85)
    c: Vertical(g83)
    c: Vertical(g87)
    c: Equal(g80,g82)
    c: Equal(g82,g84)
    c: Equal(g84,g86)
    c: PointOnObject(g88,g81)
    c: PointOnObject(g88,g87)
    c: PointOnObject(g89,g83)
    c: PointOnObject(g89,g85)
    c: Coincident(g88,g-97)
    c: Coincident(g89,g-99)
    c: Tangent(g90,g91) = 1.5708
    c: Tangent(g91,g92) = 1.5708
    c: Tangent(g92,g93) = 1.5708
    c: Tangent(g93,g94) = 1.5708
    c: Tangent(g94,g95) = 1.5708
    c: Tangent(g95,g96) = 1.5708
    c: Tangent(g96,g97) = 1.5708
    c: Tangent(g97,g90) = 1.5708
    c: Horizontal(g91)
    c: Horizontal(g95)
    c: Vertical(g93)
    c: Vertical(g97)
    c: Equal(g90,g92)
    c: Equal(g92,g94)
    c: Equal(g94,g96)
    c: PointOnObject(g98,g91)
    c: PointOnObject(g98,g97)
    c: PointOnObject(g99,g93)
    c: PointOnObject(g99,g95)
    c: Coincident(g98,g-101)
    c: Coincident(g99,g-103)
    c: Tangent(g100,g101) = 1.5708
    c: Tangent(g101,g102) = 1.5708
    c: Tangent(g102,g103) = 1.5708
    c: Tangent(g103,g104) = 1.5708
    c: Tangent(g104,g105) = 1.5708
    c: Tangent(g105,g106) = 1.5708
    c: Tangent(g106,g107) = 1.5708
    c: Tangent(g107,g100) = 1.5708
    c: Horizontal(g101)
    c: Horizontal(g105)
    c: Vertical(g103)
    c: Vertical(g107)
    c: Equal(g100,g102)
    c: Equal(g102,g104)
    c: Equal(g104,g106)
    c: PointOnObject(g108,g101)
    c: PointOnObject(g108,g107)
    c: PointOnObject(g109,g103)
    c: PointOnObject(g109,g105)
    c: Coincident(g108,g-105)
    c: Coincident(g109,g-107)
    c: Tangent(g110,g111) = 1.5708
    c: Tangent(g111,g112) = 1.5708
    c: Tangent(g112,g113) = 1.5708
    c: Tangent(g113,g114) = 1.5708
    c: Tangent(g114,g115) = 1.5708
    c: Tangent(g115,g116) = 1.5708
    c: Tangent(g116,g117) = 1.5708
    c: Tangent(g117,g110) = 1.5708
    c: Horizontal(g111)
    c: Horizontal(g115)
    c: Vertical(g113)
    c: Vertical(g117)
    c: Equal(g110,g112)
    c: Equal(g112,g114)
    c: Equal(g114,g116)
    c: PointOnObject(g118,g111)
    c: PointOnObject(g118,g117)
    c: PointOnObject(g119,g113)
    c: PointOnObject(g119,g115)
    c: Coincident(g118,g-73)
    c: Coincident(g119,g-75)
    c: Equal(g6,g10)
    c: Equal(g16,g20)
    c: Equal(g26,g30)
    c: Equal(g36,g40)
    c: Equal(g46,g50)
    c: Equal(g56,g60)
    c: Equal(g66,g70)
    c: Equal(g76,g80)
    c: Equal(g86,g90)
    c: Equal(g96,g100)
    c: Equal(g106,g110)
    c: Radius(g0) = 0.1
    c: Tangent(g120,g121) = 1.5708
    c: Tangent(g121,g122) = 1.5708
    c: Tangent(g122,g123) = 1.5708
    c: Tangent(g123,g124) = 1.5708
    c: Tangent(g124,g125) = 1.5708
    c: Tangent(g125,g126) = 1.5708
    c: Tangent(g126,g127) = 1.5708
    c: Tangent(g127,g120) = 1.5708
    c: Horizontal(g121)
    c: Horizontal(g125)
    c: Vertical(g123)
    c: Vertical(g127)
    c: PointOnObject(g128,g121)
    c: PointOnObject(g128,g127)
    c: PointOnObject(g129,g123)
    c: PointOnObject(g129,g125)
    c: Coincident(g128,g-109)
    c: Coincident(g129,g-111)
    c: Tangent(g130,g131) = 1.5708
    c: Tangent(g131,g132) = 1.5708
    c: Tangent(g132,g133) = 1.5708
    c: Tangent(g133,g134) = 1.5708
    c: Tangent(g134,g135) = 1.5708
    c: Tangent(g135,g136) = 1.5708
    c: Tangent(g136,g137) = 1.5708
    c: Tangent(g137,g130) = 1.5708
    c: Horizontal(g131)
    c: Horizontal(g135)
    c: Vertical(g133)
    c: Vertical(g137)
    c: PointOnObject(g138,g131)
    c: PointOnObject(g138,g137)
    c: PointOnObject(g139,g133)
    c: PointOnObject(g139,g135)
    c: Coincident(g138,g-113)
    c: Coincident(g139,g-115)
    c: Tangent(g140,g141) = 1.5708
    c: Tangent(g141,g142) = 1.5708
    c: Tangent(g142,g143) = 1.5708
    c: Tangent(g143,g144) = 1.5708
    c: Tangent(g144,g145) = 1.5708
    c: Tangent(g145,g146) = 1.5708
    c: Tangent(g146,g147) = 1.5708
    c: Tangent(g147,g140) = 1.5708
    c: Horizontal(g141)
    c: Horizontal(g145)
    c: Vertical(g143)
    c: Vertical(g147)
    c: PointOnObject(g148,g141)
    c: PointOnObject(g148,g147)
    c: PointOnObject(g149,g143)
    c: PointOnObject(g149,g145)
    c: Coincident(g148,g-117)
    c: Coincident(g149,g-119)
    c: Tangent(g150,g151) = 1.5708
    c: Tangent(g151,g152) = 1.5708
    c: Tangent(g152,g153) = 1.5708
    c: Tangent(g153,g154) = 1.5708
    c: Tangent(g154,g155) = 1.5708
    c: Tangent(g155,g156) = 1.5708
    c: Tangent(g156,g157) = 1.5708
    c: Tangent(g157,g150) = 1.5708
    c: Horizontal(g151)
    c: Horizontal(g155)
    c: Vertical(g153)
    c: Vertical(g157)
    c: PointOnObject(g158,g151)
    c: PointOnObject(g158,g157)
    c: PointOnObject(g159,g153)
    c: PointOnObject(g159,g155)
    c: Coincident(g158,g-121)
    c: Coincident(g159,g-123)
    c: Diameter(g120) = 0.5
    c: Equal(g120,g126)
    c: Equal(g126,g124)
    c: Equal(g124,g122)
    c: Equal(g122,g130)
    c: Equal(g130,g132)
    c: Equal(g132,g136)
    c: Equal(g136,g134)
    c: Equal(g134,g140)
    c: Equal(g140,g142)
    c: Equal(g142,g146)
    c: Equal(g146,g144)
    c: Equal(g144,g150)
    c: Equal(g150,g152)
    c: Equal(g152,g156)
    c: Equal(g156,g154)
    c: Coincident(g160,g-10)
    c: Coincident(g167,g-12)
    c: Coincident(g163,g-11)
    c: PointOnObject(g163,g160)
    c: PointOnObject(g163,g161)
    c: Tangent(g160,g162) = 1.5708
    c: Tangent(g161,g162) = -1.5708
    c: Diameter(g162) = 1
    c: Coincident(g169,g-13)
    c: PointOnObject(g167,g161)
    c: PointOnObject(g167,g164)
    c: Tangent(g161,g166) = -1.5708
    c: Tangent(g164,g166) = 1.5708
    c: PointOnObject(g169,g164)
    c: PointOnObject(g169,g165)
    c: Tangent(g164,g168) = -1.5708
    c: Tangent(g165,g168) = -1.5708
    c: Equal(g162,g166)
    c: Equal(g166,g168)
    c: Coincident(g170,g-58)
    c: Tangent(g165,g171) = -1.5708
    c: Tangent(g170,g171) = 1.5708
    c: Equal(g171,g162)
    c: PointOnObject(g165,g-13)
    c: Coincident(g176,g-16)
    c: Coincident(g179,g-17)
    c: Tangent(g172,g174) = -1.5708
    c: Tangent(g170,g174) = 1.5708
    c: PointOnObject(g172,g-15)
    c: PointOnObject(g170,g-14)
    c: Equal(g174,g162)
    c: PointOnObject(g176,g172)
    c: PointOnObject(g176,g173)
    c: Tangent(g172,g175) = -1.5708
    c: Tangent(g173,g175) = -1.5708
    c: Equal(g175,g162)
    c: Coincident(g182,g-18)
    c: PointOnObject(g179,g173)
    c: PointOnObject(g179,g177)
    c: Tangent(g173,g178) = 1.5708
    c: Tangent(g177,g178) = 1.5708
    c: Equal(g178,g162)
    c: PointOnObject(g182,g177)
    c: PointOnObject(g182,g180)
    c: Tangent(g177,g181) = 1.5708
    c: Tangent(g180,g181) = 1.5708
    c: Equal(g181,g162)
    c: Coincident(g183,g-19)
    c: Coincident(g183,g-20)
    c: Tangent(g180,g184) = 1.5708
    c: Tangent(g183,g184) = 1.5708
    c: PointOnObject(g180,g-18)
    c: Equal(g162,g184)
    c: Coincident(g183,g185)
    c: Coincident(g188,g-21)
    c: Coincident(g191,g-22)
    c: PointOnObject(g188,g185)
    c: PointOnObject(g188,g186)
    c: Tangent(g185,g187) = 1.5708
    c: Tangent(g186,g187) = 1.5708
    c: Equal(g162,g187)
    c: Coincident(g189,g-23)
    c: PointOnObject(g191,g186)
    c: PointOnObject(g191,g189)
    c: Tangent(g186,g190) = 1.5708
    c: Tangent(g189,g190) = 1.5708
    c: Equal(g162,g190)
FEATURE [PartDesign::Pad] Pad
  AddSubType = 0
  AlongSketchNormal = false
  CheckUpToFaceLimits = true
  ClaimChildren = false
  Direction = (0,0,1)
  Fit = 0
  FitJoin = 0
  InnerFit = 0
  InnerFitJoin = 0
  InnerTaperAngle = 0
  InnerTaperAngleRev = 0
  Length = 1.5
  Length2 = 100
  Linearize = true
  Midplane = true
  NewSolid = false
  Profile = -> Sketch020
  Suppress = false
  TreeRank = 277
  Type = 0
  _ProfileBasedVersion = 1
FEATURE [PartDesign::Body] Body  label="SwitchPlate"
  AutoGroupSolids = false
  ClaimAllChildren = false
  ExportMode = 0
  Group = -> [Binder002,Binder003,Binder004,Binder001,Binder005,Sketch,Sketch020,Pad]
  Origin = -> Origin
  Tip = -> Pad
  TreeRank = 20
  _ExportChildren = -> [Binder002,Binder003,Binder004,Binder001,Binder005,Sketch,Pad]
  _GroupVersion = 1
FEATURE [Part::SubShapeBinder] Import004  label="Import004(SketchPCB)"
  BindCopyOnChange = 0
  BindMode = 0
  ClaimChildren = false
  Context = -> Body014 [Import004.]
  FillStyle = 0
  Fuse = false
  MakeFace = false
  OffsetFill = false
  OffsetIntersection = false
  OffsetJoinType = 0
  OffsetOpenResult = false
  PartialLoad = false
  Relative = true
  Support = -> [Sketch009]
  TreeRank = 306
  _Version = 8
FEATURE [Part::SubShapeBinder] Import005  label="Import005(SketchFrame)"
  BindCopyOnChange = 0
  BindMode = 0
  ClaimChildren = false
  Context = -> Body014 [Import005.]
  FillStyle = 0
  Fuse = false
  MakeFace = false
  OffsetFill = false
  OffsetIntersection = false
  OffsetJoinType = 0
  OffsetOpenResult = false
  PartialLoad = false
  Relative = true
  Support = -> [Sketch006]
  TreeRank = 307
  _Version = 8
FEATURE [Part::SubShapeBinder] Import006  label="Import006(SketchSwitches)"
  BindCopyOnChange = 0
  BindMode = 0
  ClaimChildren = false
  Context = -> Body014 [Import006.]
  FillStyle = 0
  Fuse = false
  MakeFace = false
  OffsetFill = false
  OffsetIntersection = false
  OffsetJoinType = 0
  OffsetOpenResult = false
  PartialLoad = false
  Relative = true
  Support = -> [Sketch011]
  TreeRank = 308
  _Version = 8
FEATURE [Part::SubShapeBinder] Import007  label="Import007(SketchSwitchPlate)"
  BindCopyOnChange = 0
  BindMode = 0
  ClaimChildren = false
  Context = -> Body014 [Import007.]
  FillStyle = 0
  Fuse = false
  MakeFace = false
  OffsetFill = false
  OffsetIntersection = false
  OffsetJoinType = 0
  OffsetOpenResult = false
  PartialLoad = false
  Relative = true
  Support = -> [Sketch012]
  TreeRank = 309
  _Version = 8
FEATURE [Part::SubShapeBinder] Import008  label="Import008(SketchLED)"
  BindCopyOnChange = 0
  BindMode = 0
  ClaimChildren = false
  Context = -> Body014 [Import008.]
  FillStyle = 0
  Fuse = false
  MakeFace = false
  OffsetFill = false
  OffsetIntersection = false
  OffsetJoinType = 0
  OffsetOpenResult = false
  PartialLoad = false
  Relative = true
  Support = -> [Sketch014]
  TreeRank = 310
  _Version = 8
FEATURE [Sketcher::SketchObject] Sketch022
  ArcFitTolerance = 0
  AttachmentSupport = -> [XY_Plane014]
  ExternalBSplineMaxDegree = 0
  ExternalBSplineTolerance = 0
  ExternalGeometry = -> [Import004,Import005,Import006,Import007,Import008]
  FullyConstrained = true
  MapMode = 5
  Support = -> [XY_Plane014]
  TreeRank = 305
  sketch-geometry (51):
    g0: ArcOfCircle [constr] CenterX=-11.7 CenterY=33.8 CenterZ=0 NormalX=0 NormalY=0 NormalZ=1 AngleXU=0 Radius=3.98759 StartAngle=0.176459 EndAngle=2.96513
    g1: LineSegment [constr] StartX=-15.6257 StartY=34.5 StartZ=0 EndX=-29 EndY=34.5 EndZ=0
    g2: LineSegment [constr] StartX=-7.77433 StartY=34.5 StartZ=0 EndX=29 EndY=34.5 EndZ=0
    g3: LineSegment [constr] StartX=-29 StartY=34.5 StartZ=0 EndX=-29 EndY=62.5 EndZ=0
    g4: LineSegment [constr] StartX=-13.0276 StartY=33 StartZ=0 EndX=-15.6257 EndY=34.5 EndZ=0
    g5: LineSegment [constr] StartX=-15.6257 StartY=34.5 StartZ=0 EndX=-15.6257 EndY=31.5 EndZ=0
    g6: LineSegment [constr] StartX=-15.6257 StartY=31.5 StartZ=0 EndX=-13.0276 EndY=33 EndZ=0
    g7: LineSegment [constr] StartX=-29 StartY=62.5 StartZ=0 EndX=-115 EndY=62.5 EndZ=0
    g8: LineSegment [constr] StartX=-115 StartY=62.5 StartZ=0 EndX=-115 EndY=34.5 EndZ=0
    g9: LineSegment StartX=-115 StartY=34.5 StartZ=0 EndX=-113 EndY=34.5 EndZ=0
    g10: LineSegment [constr] StartX=-113 StartY=34.5 StartZ=0 EndX=-113 EndY=14.5 EndZ=0
    g11: LineSegment StartX=-10 StartY=-62.5 StartZ=0 EndX=11 EndY=-62.5 EndZ=0
    g12: LineSegment StartX=11 StartY=-62.5 StartZ=0 EndX=11 EndY=-60.5 EndZ=0
    g13: LineSegment [constr] StartX=11 StartY=-60.5 StartZ=0 EndX=31 EndY=-60.5 EndZ=0
    g14: LineSegment [constr] StartX=31 StartY=-62.5 StartZ=0 EndX=115 EndY=-62.5 EndZ=0
    g15: LineSegment [constr] StartX=115 StartY=-62.5 StartZ=0 EndX=115 EndY=14.5 EndZ=0
    g16: LineSegment [constr] StartX=113 StartY=14.5 StartZ=0 EndX=113 EndY=34.5 EndZ=0
    g17: LineSegment StartX=113 StartY=34.5 StartZ=0 EndX=115 EndY=34.5 EndZ=0
    g18: LineSegment [constr] StartX=115 StartY=34.5 StartZ=0 EndX=115 EndY=62.5 EndZ=0
    g19: LineSegment [constr] StartX=115 StartY=62.5 StartZ=0 EndX=29 EndY=62.5 EndZ=0
    g20: LineSegment [constr] StartX=29 StartY=62.5 StartZ=0 EndX=29 EndY=34.5 EndZ=0
    g21: GeomPoint [constr] X=11 Y=-48.5 Z=0
    g22: GeomPoint [constr] X=14.9 Y=31.5 Z=0
    g23: GeomPoint [constr] X=19.9 Y=26.5 Z=0
    g24: ArcOfCircle CenterX=-113 CenterY=32.5 CenterZ=0 NormalX=0 NormalY=0 NormalZ=1 AngleXU=0 Radius=2 StartAngle=4.71239 EndAngle=7.85398
    g25: ArcOfCircle CenterX=13 CenterY=-60.5 CenterZ=0 NormalX=0 NormalY=0 NormalZ=1 AngleXU=0 Radius=2 StartAngle=0 EndAngle=3.14159
    g26: LineSegment StartX=15 StartY=-60.5 StartZ=0 EndX=27 EndY=-60.5 EndZ=0
    g27: ArcOfCircle CenterX=113 CenterY=32.5 CenterZ=0 NormalX=0 NormalY=0 NormalZ=1 AngleXU=0 Radius=2 StartAngle=1.5708 EndAngle=4.71239
    g28: LineSegment StartX=113 StartY=30.5 StartZ=0 EndX=113 EndY=18.5 EndZ=0
    g29: LineSegment StartX=-115 StartY=-12.5 StartZ=0 EndX=4 EndY=-12.5 EndZ=0
    g30: LineSegment StartX=-113 StartY=30.5 StartZ=0 EndX=-113 EndY=18.5 EndZ=0
    g31: ArcOfCircle CenterX=-113 CenterY=16.5 CenterZ=0 NormalX=0 NormalY=0 NormalZ=1 AngleXU=0 Radius=2 StartAngle=4.71239 EndAngle=7.85398
    g32: LineSegment StartX=-113 StartY=14.5 StartZ=0 EndX=-115 EndY=14.5 EndZ=0
    g33: LineSegment StartX=-115 StartY=14.5 StartZ=0 EndX=-115 EndY=-12.5 EndZ=0
    g34: Circle CenterX=-106 CenterY=29.5 CenterZ=0 NormalX=0 NormalY=0 NormalZ=1 AngleXU=0 Radius=1.55
    g35: ArcOfCircle CenterX=29 CenterY=-60.5 CenterZ=0 NormalX=0 NormalY=0 NormalZ=1 AngleXU=0 Radius=2 StartAngle=-9e-16 EndAngle=3.14159
    g36: LineSegment StartX=31 StartY=-60.5 StartZ=0 EndX=31 EndY=-62.5 EndZ=0
    g37: LineSegment StartX=115 StartY=14.5 StartZ=0 EndX=113 EndY=14.5 EndZ=0
    g38: ArcOfCircle CenterX=113 CenterY=16.5 CenterZ=0 NormalX=0 NormalY=0 NormalZ=1 AngleXU=0 Radius=2 StartAngle=1.5708 EndAngle=4.71239
    g39: Circle CenterX=16 CenterY=-53.5 CenterZ=0 NormalX=0 NormalY=0 NormalZ=1 AngleXU=0 Radius=1.55
    g40: Circle CenterX=106 CenterY=19.5 CenterZ=0 NormalX=0 NormalY=0 NormalZ=1 AngleXU=0 Radius=1.55
    g41: LineSegment StartX=-115 StartY=38.35 StartZ=0 EndX=115 EndY=38.35 EndZ=0
    g42: LineSegment [constr] StartX=-11.7 StartY=35.35 StartZ=0 EndX=-11.7 EndY=38.35 EndZ=0
    g43: LineSegment StartX=-115 StartY=34.5 StartZ=0 EndX=-115 EndY=38.35 EndZ=0
    g44: LineSegment StartX=115 StartY=38.35 StartZ=0 EndX=115 EndY=34.5 EndZ=0
    g45: LineSegment [constr] StartX=94 StartY=-62.5 StartZ=0 EndX=94 EndY=-41.5 EndZ=0
    g46: LineSegment [constr] StartX=94 StartY=-41.5 StartZ=0 EndX=115 EndY=-41.5 EndZ=0
    g47: LineSegment StartX=34 StartY=-62.5 StartZ=0 EndX=34 EndY=-18 EndZ=0
    g48: LineSegment StartX=34 StartY=-18 StartZ=0 EndX=115 EndY=-18 EndZ=0
    g49: LineSegment StartX=31 StartY=-62.5 StartZ=0 EndX=34 EndY=-62.5 EndZ=0
    g50: LineSegment StartX=115 StartY=-18 StartZ=0 EndX=115 EndY=14.5 EndZ=0
  constraints (142):
    c: Coincident(g0,g-75)
    c: Coincident(g1,g0)
    c: PointOnObject(g1,g-72)
    c: Horizontal(g1)
    c: Coincident(g2,g0)
    c: PointOnObject(g2,g-74)
    c: Horizontal(g2)
    c: Horizontal(g0,g0)
    c: Coincident(g3,g1)
    c: Coincident(g3,g-72)
    c: Coincident(g4,g5)
    c: Coincident(g5,g6)
    c: Coincident(g6,g4)
    c: Equal(g4,g5)
    c: Equal(g4,g6)
    c: Coincident(g0,g4)
    c: PointOnObject(g4,g-75)
    c: PointOnObject(g5,g-78)
    c: Vertical(g5)
    c: DistanceY(g5,g5) = 3
    c: Coincident(g7,g3)
    c: Coincident(g7,g-21)
    c: Coincident(g7,g8)
    c: PointOnObject(g8,g-20)
    c: Perpendicular(g8,g9) = 1.5708
    c: Coincident(g9,g10)
    c: Vertical(g10)
    c: Coincident(g-98,g11)
    c: PointOnObject(g11,g-22)
    c: Coincident(g11,g12)
    c: Vertical(g12)
    c: Coincident(g12,g13)
    c: Horizontal(g13)
    c: PointOnObject(g14,g-22)
    c: Coincident(g14,g-23)
    c: Coincident(g14,g15)
    c: PointOnObject(g15,g-23)
    c: Vertical(g16)
    c: Coincident(g16,g17)
    c: PointOnObject(g17,g-23)
    c: Horizontal(g17)
    c: Coincident(g17,g18)
    c: Coincident(g18,g-23)
    c: Coincident(g18,g19)
    c: Coincident(g19,g-74)
    c: Coincident(g19,g20)
    c: Coincident(g20,g2)
    c: DistanceX(g9,g9) = 2
    c: DistanceY(g10,g10) = 20
    c: Equal(g9,g17)
    c: Equal(g17,g12)
    c: Horizontal(g8,g17)
    c: Equal(g10,g16)
    c: Equal(g16,g13)
    c: PointOnObject(g21,g-99)
    c: Horizontal(g-99,g21)
    c: Vertical(g11,g21)
    c: Coincident(g22,g-90)
    c: Coincident(g23,g-92)
    c: PointOnObject(g24,g10)
    c: Coincident(g24,g9)
    c: PointOnObject(g24,g10)
    c: Radius(g24) = 2
    c: PointOnObject(g25,g13)
    c: Coincident(g25,g12)
    c: PointOnObject(g25,g13)
    c: Coincident(g26,g25)
    c: PointOnObject(g27,g16)
    c: Coincident(g27,g17)
    c: PointOnObject(g27,g16)
    c: Coincident(g28,g27)
    c: Coincident(g29,g-94)
    c: PointOnObject(g29,g-20)
    c: Horizontal(g29)
    c: PointOnObject(g30,g10)
    c: Coincident(g30,g24)
    c: PointOnObject(g31,g10)
    c: Coincident(g31,g10)
    c: Coincident(g30,g31)
    c: Coincident(g32,g31)
    c: PointOnObject(g32,g-20)
    c: Horizontal(g32)
    c: Equal(g31,g24)
    c: Coincident(g33,g32)
    c: Coincident(g33,g29)
    c: Diameter(g34) = 3.1
    c: Distance(g34,g-20) = 9
    c: Distance(g34,g9) = 5
    c: Horizontal(g9,g1)
    c: PointOnObject(g26,g13)
    c: Vertical(g14,g13)
    c: PointOnObject(g35,g13)
    c: Coincident(g35,g13)
    c: Coincident(g26,g35)
    c: Equal(g25,g35)
    c: Coincident(g36,g35)
    c: Coincident(g36,g14)
    c: Equal(g25,g24)
    c: PointOnObject(g28,g16)
    c: Horizontal(g15,g16)
    c: Coincident(g37,g15)
    c: Coincident(g37,g16)
    c: PointOnObject(g38,g16)
    c: Coincident(g38,g28)
    c: Coincident(g38,g37)
    c: Equal(g27,g38)
    c: Equal(g27,g24)
    c: Equal(g34,g39)
    c: Equal(g39,g40)
    c: Distance(g39,g12) = 5
    c: Distance(g39,g-22) = 9
    c: Distance(g40,g-23) = 9
    c: Distance(g40,g37) = 5
    c: PointOnObject(g41,g8)
    c: PointOnObject(g41,g18)
    c: Horizontal(g41)
    c: Vertical(g42)
    c: PointOnObject(g42,g41)
    c: Perpendicular(g42,g-75) = 1.5708
    c: DistanceY(g42,g42) = 3
    c: Coincident(g43,g41)
    c: Coincident(g43,g9)
    c: Coincident(g44,g41)
    c: Coincident(g44,g17)
    c: PointOnObject(g45,g14)
    c: Vertical(g45)
    c: Coincident(g45,g46)
    c: PointOnObject(g46,g15)
    c: Horizontal(g46)
    c: DistanceY(g45,g45) = 21
    c: DistanceX(g46,g46) = 21
    c: Vertical(g47)
    c: Coincident(g47,g48)
    c: Horizontal(g48)
    c: Coincident(g49,g36)
    c: Coincident(g49,g47)
    c: Coincident(g50,g48)
    c: Coincident(g50,g37)
    c: Vertical(g50)
    c: DistanceX(g49,g49) = 3
    c: DistanceY(g48,g-71) = 3
    c: PointOnObject(g47,g14)
FEATURE [PartDesign::Pad] Pad018
  AddSubType = 0
  AlongSketchNormal = false
  CheckUpToFaceLimits = true
  ClaimChildren = false
  Direction = (0,0,1)
  Fit = 0
  FitJoin = 0
  InnerFit = 0
  InnerFitJoin = 0
  InnerTaperAngle = 0
  InnerTaperAngleRev = 0
  Length = 1.5
  Length2 = 100
  Linearize = true
  Midplane = true
  NewSolid = false
  Profile = -> Sketch022
  Refine = true
  Suppress = false
  TreeRank = 311
  Type = 0
  _ProfileBasedVersion = 1
FEATURE [PartDesign::Body] Body014  label="SwitchPlate_PrintedStandoffs"
  AutoGroupSolids = false
  ClaimAllChildren = false
  ExportMode = 0
  Group = -> [Sketch022,Import004,Import005,Import006,Import007,Import008,Pad018]
  Origin = -> Origin014
  Tip = -> Pad018
  TreeRank = 33
  _ExportChildren = -> [Import004,Import005,Import006,Import007,Import008,Pad018]
  _GroupVersion = 1
FEATURE [Part::SubShapeBinder] Import  label="Import(SketchSwitches)"
  BindCopyOnChange = 0
  BindMode = 0
  ClaimChildren = false
  Context = -> <external abc-flat-profiles.FCStd>#Link001 [Import.]
  FillStyle = 0
  Fuse = false
  MakeFace = false
  OffsetFill = false
  OffsetIntersection = false
  OffsetJoinType = 0
  OffsetOpenResult = false
  PartialLoad = false
  Relative = false
  Support = -> [Sketch011]
  TreeRank = 312
  _Version = 8
FEATURE [Sketcher::SketchObject] Sketch001
  ArcFitTolerance = 0
  AttachmentSupport = -> [XY_Plane001]
  ExternalBSplineMaxDegree = 0
  ExternalBSplineTolerance = 0
  ExternalGeometry = -> [Binder006,Binder007,Binder008,Import]
  FullyConstrained = true
  MapMode = 5
  Support = -> [XY_Plane001]
  TreeRank = 152
  sketch-geometry (16):
    g0: LineSegment [constr] StartX=-135 StartY=82.5 StartZ=0 EndX=-115 EndY=62.5 EndZ=0
    g1: LineSegment [constr] StartX=-135 StartY=-82.5 StartZ=0 EndX=-115 EndY=-62.5 EndZ=0
    g2: LineSegment [constr] StartX=135 StartY=-82.5 StartZ=0 EndX=115 EndY=-62.5 EndZ=0
    g3: LineSegment [constr] StartX=135 StartY=82.5 StartZ=0 EndX=115 EndY=62.5 EndZ=0
    g4: Circle CenterX=-105 CenterY=72.5 CenterZ=0 NormalX=0 NormalY=0 NormalZ=1 AngleXU=0 Radius=1.55
    g5: Circle CenterX=-125 CenterY=-72.5 CenterZ=0 NormalX=0 NormalY=0 NormalZ=1 AngleXU=0 Radius=1.55
    g6: Circle CenterX=105 CenterY=72.5 CenterZ=0 NormalX=0 NormalY=0 NormalZ=1 AngleXU=0 Radius=1.55
    g7: Circle CenterX=125 CenterY=-72.5 CenterZ=0 NormalX=0 NormalY=0 NormalZ=1 AngleXU=0 Radius=1.55
    g8: Circle CenterX=-17.4 CenterY=29 CenterZ=0 NormalX=0 NormalY=0 NormalZ=1 AngleXU=0 Radius=1.6
    g9: Circle CenterX=-5.8 CenterY=29 CenterZ=0 NormalX=0 NormalY=0 NormalZ=1 AngleXU=0 Radius=1.6
    g10: Circle CenterX=5.8 CenterY=29 CenterZ=0 NormalX=0 NormalY=0 NormalZ=1 AngleXU=0 Radius=1.6
    g11: Circle CenterX=17.4 CenterY=29 CenterZ=0 NormalX=0 NormalY=0 NormalZ=1 AngleXU=0 Radius=1.6
    g12: Circle CenterX=-125 CenterY=0 CenterZ=0 NormalX=0 NormalY=0 NormalZ=1 AngleXU=0 Radius=1.55
    g13: Circle CenterX=125 CenterY=0 CenterZ=0 NormalX=0 NormalY=0 NormalZ=1 AngleXU=0 Radius=1.55
    g14: GeomPoint [constr] X=-125 Y=72.5 Z=0
    g15: GeomPoint [constr] X=125 Y=72.5 Z=0
  constraints (33):
    c: Coincident(g0,g-4)
    c: Coincident(g0,g-9)
    c: Coincident(g1,g-5)
    c: Coincident(g1,g-8)
    c: Coincident(g2,g-6)
    c: Coincident(g2,g-10)
    c: Coincident(g3,g-6)
    c: Coincident(g3,g-10)
    c: Equal(g4,g5)
    c: Equal(g5,g6)
    c: Equal(g6,g7)
    c: Diameter(g4) = 3.1
    c: Symmetric(g1,g1,g5)
    c: Symmetric(g2,g2,g7)
    c: Equal(g8,g9)
    c: Equal(g9,g10)
    c: Equal(g10,g11)
    c: Diameter(g8) = 3.2
    c: Symmetric(g-25,g-26,g8)
    c: Symmetric(g-28,g-30,g9)
    c: Symmetric(g-32,g-34,g10)
    c: Symmetric(g-36,g-38,g11)
    c: PointOnObject(g12,g-1)
    c: PointOnObject(g13,g-1)
    c: Equal(g12,g13)
    c: Equal(g13,g4)
    c: Symmetric(g0,g0,g14)
    c: Horizontal(g4,g14)
    c: DistanceX(g14,g4) = 20
    c: Symmetric(g3,g3,g15)
    c: Symmetric(g4,g6,g-2)
    c: Vertical(g12,g5)
    c: Vertical(g13,g7)
FEATURE [PartDesign::Pad] Pad009
  AddSubType = 0
  AlongSketchNormal = false
  CheckUpToFaceLimits = true
  ClaimChildren = false
  Direction = (0,0,1)
  Fit = 0
  FitJoin = 0
  InnerFit = 0
  InnerFitJoin = 0
  InnerTaperAngle = 0
  InnerTaperAngleRev = 0
  Length = 1.5
  Length2 = 100
  Linearize = true
  Midplane = true
  NewSolid = false
  Profile = -> Sketch001
  Suppress = false
  TreeRank = 159
  Type = 0
  _ProfileBasedVersion = 1
FEATURE [PartDesign::Fillet] Fillet012
  AddSubType = 0
  Base = -> Pad009 [Edge8,Edge5,Edge2,Edge1]
  BaseFeature = -> Pad009
  NewSolid = false
  Radius = 1
  SupportTransform = false
  Suppress = false
  TreeRank = 160
FEATURE [PartDesign::Body] Body001  label="TopPanel"
  AutoGroupSolids = false
  ClaimAllChildren = false
  ExportMode = 0
  Group = -> [Sketch001,Binder006,Binder007,Binder008,Pad009,Fillet012,Import]
  Origin = -> Origin001
  Tip = -> Fillet012
  TreeRank = 35
  _ExportChildren = -> [Binder006,Binder007,Binder008,Pad009,Fillet012,Import]
  _GroupVersion = 1
FEATURE [Part::SubShapeBinder] Import009  label="Import009(SketchFrame)"
  BindCopyOnChange = 0
  BindMode = 0
  ClaimChildren = false
  Context = -> Body015 [Import009.]
  FillStyle = 0
  Fuse = false
  MakeFace = false
  OffsetFill = false
  OffsetIntersection = false
  OffsetJoinType = 0
  OffsetOpenResult = false
  PartialLoad = false
  Relative = true
  Support = -> [Sketch006]
  TreeRank = 325
  _Version = 8
FEATURE [Part::SubShapeBinder] Import010  label="Import010(SketchSwitches)"
  BindCopyOnChange = 0
  BindMode = 0
  ClaimChildren = false
  Context = -> Body015 [Import010.]
  FillStyle = 0
  Fuse = false
  MakeFace = false
  OffsetFill = false
  OffsetIntersection = false
  OffsetJoinType = 0
  OffsetOpenResult = false
  PartialLoad = false
  Relative = true
  Support = -> [Sketch011]
  TreeRank = 326
  _Version = 8
FEATURE [Part::SubShapeBinder] Import011  label="Import011(SketchLED)"
  BindCopyOnChange = 0
  BindMode = 0
  ClaimChildren = false
  Context = -> Body015 [Import011.]
  FillStyle = 0
  Fuse = false
  MakeFace = false
  OffsetFill = false
  OffsetIntersection = false
  OffsetJoinType = 0
  OffsetOpenResult = false
  PartialLoad = false
  Relative = true
  Support = -> [Sketch014]
  TreeRank = 327
  _Version = 8
FEATURE [Part::SubShapeBinder] Import012  label="Import012(SketchSwitchPlate)"
  BindCopyOnChange = 0
  BindMode = 0
  ClaimChildren = false
  Context = -> Body015 [Import012.]
  FillStyle = 0
  Fuse = false
  MakeFace = false
  OffsetFill = false
  OffsetIntersection = false
  OffsetJoinType = 0
  OffsetOpenResult = false
  PartialLoad = false
  Relative = true
  Support = -> [Sketch012]
  TreeRank = 328
  _Version = 8
FEATURE [Sketcher::SketchObject] Sketch023
  ArcFitTolerance = 1e-06
  AttachmentSupport = -> [XY_Plane015]
  ExternalBSplineMaxDegree = 0
  ExternalBSplineTolerance = 0
  ExternalGeometry = -> [Import009,Import010,Import011,Import012]
  FullyConstrained = true
  MapMode = 5
  Support = -> [XY_Plane015]
  TreeRank = 329
  sketch-geometry (9):
    g0: LineSegment StartX=115 StartY=-25 StartZ=0 EndX=24 EndY=-25 EndZ=0
    g1: LineSegment StartX=24 StartY=-25 StartZ=0 EndX=24 EndY=-62.5 EndZ=0
    g2: LineSegment StartX=-10 StartY=-41.5 StartZ=0 EndX=-10 EndY=-62.5 EndZ=0
    g3: LineSegment StartX=-115 StartY=38.35 StartZ=0 EndX=-115 EndY=-12.5 EndZ=0
    g4: LineSegment StartX=-115 StartY=-12.5 StartZ=0 EndX=-113.5 EndY=-12.5 EndZ=0
    g5: LineSegment StartX=115 StartY=38.35 StartZ=0 EndX=115 EndY=-25 EndZ=0
    g6: LineSegment StartX=-10 StartY=-62.5 StartZ=0 EndX=24 EndY=-62.5 EndZ=0
    g7: LineSegment StartX=-115 StartY=38.35 StartZ=0 EndX=115 EndY=38.35 EndZ=0
    g8: GeomPoint [constr] X=-11.7 Y=35.35 Z=0
  constraints (25):
    c: PointOnObject(g5,g-4)
    c: PointOnObject(g0,g-4)
    c: Horizontal(g0)
    c: Coincident(g1,g0)
    c: PointOnObject(g1,g-6)
    c: Vertical(g1)
    c: Coincident(g2,g-17)
    c: PointOnObject(g2,g-6)
    c: Vertical(g2)
    c: DistanceY(g0,g-10) = 3
    c: DistanceX(g-10,g0) = 3
    c: PointOnObject(g3,g-82)
    c: Coincident(g3,g4)
    c: Coincident(g4,g-13)
    c: Horizontal(g4)
    c: Coincident(g5,g0)
    c: Coincident(g6,g2)
    c: Coincident(g6,g1)
    c: PointOnObject(g3,g-82)
    c: Coincident(g7,g3)
    c: Coincident(g7,g5)
    c: Horizontal(g7)
    c: PointOnObject(g8,g-11)
    c: Vertical(g-11,g8)
    c: Distance(g8,g7) = 3
FEATURE [PartDesign::Pad] Pad019
  AddSubType = 0
  AlongSketchNormal = false
  CheckUpToFaceLimits = true
  ClaimChildren = false
  Direction = (0,0,1)
  Fit = 0
  FitJoin = 0
  InnerFit = 0
  InnerFitJoin = 0
  InnerTaperAngle = 0
  InnerTaperAngleRev = 0
  Length = 1.5
  Length2 = 100
  Linearize = true
  Midplane = true
  NewSolid = false
  Profile = -> Sketch023
  Refine = true
  Suppress = false
  TreeRank = 330
  Type = 0
  _ProfileBasedVersion = 1
FEATURE [PartDesign::Fillet] Fillet
  AddSubType = 0
  Base = -> Pad019 [Edge219,Edge220,Edge222,Edge224,Edge211,Edge212,Edge214,Edge216,Edge203,Edge204,Edge206,Edge208,Edge195,Edge196,Edge198,Edge200]
  BaseFeature = -> Pad019
  NewSolid = false
  Radius = 0.5
  Refine = true
  SupportTransform = false
  Suppress = false
  TreeRank = 331
FEATURE [PartDesign::Fillet] Fillet024
  AddSubType = 0
  Base = -> Fillet [Edge221,Edge220,Edge225,Edge223,Edge212,Edge217,Edge213,Edge215,Edge204,Edge209,Edge207,Edge205,Edge197,Edge196,Edge201,Edge199,Edge189,Edge188,Edge193,Edge191,Edge180,Edge185,Edge183,Edge181,Edge173,Edge172,Edge177,Edge175,Edge164,Edge169,Edge167,Edge165,Edge157,Edge156,Edge161,Edge159,Edge149,Edge148,Edge153,Edge151,+8 more]
  BaseFeature = -> Fillet
  NewSolid = false
  Radius = 0.1
  Refine = true
  SupportTransform = false
  Suppress = false
  TreeRank = 332
FEATURE [PartDesign::Body] Body015  label="SwitchPlate_Bent"
  AutoGroupSolids = false
  ClaimAllChildren = false
  ExportMode = 0
  Group = -> [Sketch023,Import009,Import010,Import011,Import012,Pad019,Fillet,Fillet024]
  Origin = -> Origin015
  Tip = -> Fillet024
  TreeRank = 34
  _ExportChildren = -> [Import009,Import010,Import011,Import012,Pad019,Fillet,Fillet024]
  _GroupVersion = 1
FEATURE [PartDesign::FeatureBase] BaseFeature
  BaseFeature = -> Body015
  NewSolid = false
  Suppress = false
  TreeRank = 343
FEATURE [Sketcher::SketchObject] Sketch024
  ArcFitTolerance = 1e-06
  AttachmentSupport = -> [BaseFeature]
  ExternalBSplineMaxDegree = 0
  ExternalBSplineTolerance = 0
  ExternalGeometry = -> [BaseFeature]
  FullyConstrained = true
  MapMode = 5
  Placement = pos=(0,0,-0.75) rot=(1,0,0;3.14159rad)
  Support = -> [BaseFeature]
  TreeRank = 344
  sketch-geometry (16):
    g0: LineSegment StartX=-115 StartY=-38.35 StartZ=0 EndX=-113.5 EndY=-38.35 EndZ=0
    g1: LineSegment StartX=-113.5 StartY=-38.35 StartZ=0 EndX=-113.5 EndY=-28.35 EndZ=0
    g2: LineSegment StartX=-113.5 StartY=-28.35 StartZ=0 EndX=-115 EndY=-28.35 EndZ=0
    g3: LineSegment StartX=-115 StartY=-28.35 StartZ=0 EndX=-115 EndY=-38.35 EndZ=0
    g4: LineSegment StartX=-115 StartY=12.5 StartZ=0 EndX=-113.5 EndY=12.5 EndZ=0
    g5: LineSegment StartX=-113.5 StartY=12.5 StartZ=0 EndX=-113.5 EndY=2.5 EndZ=0
    g6: LineSegment StartX=-113.5 StartY=2.5 StartZ=0 EndX=-115 EndY=2.5 EndZ=0
    g7: LineSegment StartX=-115 StartY=2.5 StartZ=0 EndX=-115 EndY=12.5 EndZ=0
    g8: LineSegment StartX=115 StartY=12.5 StartZ=0 EndX=113.5 EndY=12.5 EndZ=0
    g9: LineSegment StartX=113.5 StartY=12.5 StartZ=0 EndX=113.5 EndY=2.5 EndZ=0
    g10: LineSegment StartX=113.5 StartY=2.5 StartZ=0 EndX=115 EndY=2.5 EndZ=0
    g11: LineSegment StartX=115 StartY=2.5 StartZ=0 EndX=115 EndY=12.5 EndZ=0
    g12: LineSegment StartX=115 StartY=-28.35 StartZ=0 EndX=113.5 EndY=-28.35 EndZ=0
    g13: LineSegment StartX=113.5 StartY=-28.35 StartZ=0 EndX=113.5 EndY=-38.35 EndZ=0
    g14: LineSegment StartX=113.5 StartY=-38.35 StartZ=0 EndX=115 EndY=-38.35 EndZ=0
    g15: LineSegment StartX=115 StartY=-38.35 StartZ=0 EndX=115 EndY=-28.35 EndZ=0
  constraints (45):
    c: Coincident(g0,g1)
    c: Coincident(g1,g2)
    c: Coincident(g2,g3)
    c: Coincident(g3,g0)
    c: Horizontal(g0)
    c: Horizontal(g2)
    c: Vertical(g1)
    c: Vertical(g3)
    c: Coincident(g0,g-3)
    c: Coincident(g4,g5)
    c: Coincident(g5,g6)
    c: Coincident(g6,g7)
    c: Coincident(g7,g4)
    c: Horizontal(g4)
    c: Horizontal(g6)
    c: Vertical(g5)
    c: Vertical(g7)
    c: Coincident(g4,g-3)
    c: Coincident(g8,g9)
    c: Coincident(g9,g10)
    c: Coincident(g10,g11)
    c: Horizontal(g8)
    c: Horizontal(g10)
    c: Vertical(g9)
    c: Vertical(g11)
    c: Coincident(g12,g13)
    c: Coincident(g13,g14)
    c: Coincident(g14,g15)
    c: Coincident(g15,g12)
    c: Horizontal(g12)
    c: Horizontal(g14)
    c: Vertical(g13)
    c: Vertical(g15)
    c: Equal(g6,g0)
    c: Equal(g0,g14)
    c: Equal(g14,g10)
    c: Equal(g3,g7)
    c: Equal(g7,g15)
    c: Equal(g15,g11)
    c: DistanceX(g0,g0) = 1.5
    c: DistanceY(g3,g3) = 10
    c: Coincident(g14,g-4)
    c: Coincident(g11,g8)
    c: Horizontal(g6,g9)
    c: PointOnObject(g10,g-4)
FEATURE [PartDesign::Pad] Pad020
  AddSubType = 0
  AlongSketchNormal = false
  BaseFeature = -> BaseFeature
  CheckUpToFaceLimits = true
  ClaimChildren = false
  Direction = (0,0,-1)
  Fit = 0
  FitJoin = 0
  InnerFit = 0
  InnerFitJoin = 0
  InnerTaperAngle = 0
  InnerTaperAngleRev = 0
  Length = 15
  Length2 = 100
  Linearize = true
  NewSolid = false
  Profile = -> Sketch024
  Refine = true
  Suppress = false
  TreeRank = 345
  Type = 0
  _ProfileBasedVersion = 1
FEATURE [Sketcher::SketchObject] Sketch025
  ArcFitTolerance = 1e-06
  AttachmentSupport = -> [YZ_Plane016]
  ExternalBSplineMaxDegree = 0
  ExternalBSplineTolerance = 0
  ExternalGeometry = -> [Pad020]
  FullyConstrained = true
  MapMode = 5
  Placement = pos=(0,0,0) rot=(0.57735,0.57735,0.57735;2.0944rad)
  Support = -> [YZ_Plane016]
  TreeRank = 346
  sketch-geometry (4):
    g0: LineSegment [constr] StartX=-7.5 StartY=-15.75 StartZ=0 EndX=-7.5 EndY=-5.75 EndZ=0
    g1: LineSegment [constr] StartX=33.35 StartY=-15.75 StartZ=0 EndX=33.35 EndY=-5.75 EndZ=0
    g2: Circle CenterX=-7.5 CenterY=-5.75 CenterZ=0 NormalX=0 NormalY=0 NormalZ=1 AngleXU=0 Radius=1.55
    g3: Circle CenterX=33.35 CenterY=-5.75 CenterZ=0 NormalX=0 NormalY=0 NormalZ=1 AngleXU=0 Radius=1.55
  constraints (10):
    c: Vertical(g0)
    c: Vertical(g1)
    c: DistanceY(g0,g0) = 10
    c: DistanceY(g1,g1) = 10
    c: Symmetric(g-3,g-3,g0)
    c: Symmetric(g-4,g-4,g1)
    c: Coincident(g2,g0)
    c: Coincident(g3,g1)
    c: Equal(g2,g3)
    c: Diameter(g2) = 3.1
FEATURE [PartDesign::Pocket] Pocket
  AddSubType = 1
  BaseFeature = -> Pad020
  CheckUpToFaceLimits = true
  ClaimChildren = false
  Fit = 0
  FitJoin = 0
  InnerFit = 0
  InnerFitJoin = 0
  InnerTaperAngle = 0
  InnerTaperAngleRev = 0
  Length = 5
  Length2 = 100
  Linearize = true
  Midplane = true
  NewSolid = false
  Profile = -> Sketch025
  Refine = true
  Suppress = false
  TreeRank = 347
  Type = 1
  _ProfileBasedVersion = 1
  _Version = 1
FEATURE [Sketcher::SketchObject] Sketch026
  ArcFitTolerance = 1e-06
  AttachmentSupport = -> [XY_Plane016]
  ExternalBSplineMaxDegree = 0
  ExternalBSplineTolerance = 0
  ExternalGeometry = -> [Pocket]
  FullyConstrained = true
  MapMode = 5
  Placement = pos=(0,0,0) rot=(0,1,0;3.14159rad)
  Support = -> [XY_Plane016]
  TreeRank = 348
  sketch-geometry (15):
    g0: ArcOfCircle CenterX=-113.5 CenterY=26.85 CenterZ=0 NormalX=0 NormalY=0 NormalZ=1 AngleXU=0 Radius=1.5 StartAngle=4.71239 EndAngle=7.85398
    g1: LineSegment StartX=-113.5 StartY=25.35 StartZ=0 EndX=-115 EndY=25.35 EndZ=0
    g2: LineSegment StartX=-115 StartY=28.35 StartZ=0 EndX=-115 EndY=25.35 EndZ=0
    g3: LineSegment StartX=-115 StartY=-2.5 StartZ=0 EndX=-115 EndY=0.5 EndZ=0
    g4: LineSegment StartX=-115 StartY=0.5 StartZ=0 EndX=-113.5 EndY=0.5 EndZ=0
    g5: ArcOfCircle CenterX=-113.5 CenterY=-1 CenterZ=0 NormalX=0 NormalY=0 NormalZ=1 AngleXU=0 Radius=1.5 StartAngle=4.71239 EndAngle=7.85398
    g6: LineSegment StartX=-115 StartY=-12.5 StartZ=0 EndX=-115 EndY=-15.5 EndZ=0
    g7: LineSegment StartX=-115 StartY=-15.5 StartZ=0 EndX=-113.5 EndY=-15.5 EndZ=0
    g8: ArcOfCircle CenterX=-113.5 CenterY=-14 CenterZ=0 NormalX=0 NormalY=0 NormalZ=1 AngleXU=0 Radius=1.5 StartAngle=4.71239 EndAngle=7.85398
    g9: LineSegment StartX=115 StartY=28.35 StartZ=0 EndX=115 EndY=25.35 EndZ=0
    g10: LineSegment StartX=115 StartY=25.35 StartZ=0 EndX=113.5 EndY=25.35 EndZ=0
    g11: ArcOfCircle CenterX=113.5 CenterY=26.85 CenterZ=0 NormalX=0 NormalY=0 NormalZ=1 AngleXU=0 Radius=1.5 StartAngle=1.5708 EndAngle=4.71239
    g12: LineSegment StartX=115 StartY=-2.5 StartZ=0 EndX=115 EndY=0.5 EndZ=0
    g13: LineSegment StartX=115 StartY=0.5 StartZ=0 EndX=113.5 EndY=0.5 EndZ=0
    g14: ArcOfCircle CenterX=113.5 CenterY=-1 CenterZ=0 NormalX=0 NormalY=0 NormalZ=1 AngleXU=0 Radius=1.5 StartAngle=1.5708 EndAngle=4.71239
  constraints (41):
    c: Coincident(g0,g-3)
    c: Coincident(g1,g0)
    c: Horizontal(g1)
    c: Coincident(g2,g-3)
    c: Coincident(g2,g1)
    c: Vertical(g2)
    c: Vertical(g0,g0)
    c: Vertical(g0,g0)
    c: Diameter(g0) = 3
    c: Coincident(g-6,g3)
    c: Vertical(g3)
    c: Coincident(g3,g4)
    c: Horizontal(g4)
    c: Tangent(g4,g5) = 1.5708
    c: Coincident(g5,g-6)
    c: Vertical(g5,g5)
    c: Equal(g5,g0)
    c: Coincident(g-7,g6)
    c: Vertical(g6)
    c: Coincident(g6,g7)
    c: Horizontal(g7)
    c: Tangent(g7,g8) = -1.5708
    c: Coincident(g8,g-7)
    c: Coincident(g-4,g9)
    c: Vertical(g9)
    c: Coincident(g9,g10)
    c: Horizontal(g10)
    c: Tangent(g10,g11) = 1.5708
    c: Coincident(g11,g-4)
    c: Coincident(g-5,g12)
    c: Vertical(g12)
    c: Coincident(g12,g13)
    c: Horizontal(g13)
    c: Tangent(g13,g14) = -1.5708
    c: Coincident(g14,g-5)
    c: Vertical(g8,g8)
    c: Equal(g5,g8)
    c: Equal(g11,g0)
    c: Vertical(g11,g11)
    c: Equal(g11,g14)
    c: Vertical(g14,g14)
FEATURE [PartDesign::Pocket] Pocket001
  AddSubType = 1
  BaseFeature = -> Pocket
  CheckUpToFaceLimits = true
  ClaimChildren = false
  Fit = 0
  FitJoin = 0
  InnerFit = 0
  InnerFitJoin = 0
  InnerTaperAngle = 0
  InnerTaperAngleRev = 0
  Length = 5
  Length2 = 100
  Linearize = true
  Midplane = true
  NewSolid = false
  Profile = -> Sketch026
  Refine = true
  Suppress = false
  TreeRank = 349
  Type = 1
  _ProfileBasedVersion = 1
  _Version = 1
FEATURE [PartDesign::FeaturePython] SolidBend  # WARN: FeaturePython — macro-defined, semantics opaque (R4)
  BaseFeature = -> Pocket001
  NewSolid = false
  Suppress = false
  TreeRank = 350
  baseObject = -> Pocket001 [Edge8,Edge2,Edge20,Edge26]
  radius = 1
  thickness = 1.5
FEATURE [PartDesign::Body] Body016  label="SwitchPlate_Bent_2x"
  AutoGroupSolids = false
  BaseFeature = -> Body015
  ClaimAllChildren = false
  ExportMode = 0
  Group = -> [BaseFeature,Sketch024,Pad020,Sketch025,Pocket,Sketch026,Pocket001,SolidBend]
  Origin = -> Origin016
  Tip = -> SolidBend
  TreeRank = 342
  _ExportChildren = -> [BaseFeature,Pad020,Pocket,Pocket001,SolidBend]
  _GroupVersion = 1
FEATURE [PartDesign::SubShapeBinder] BaseFeature001  label="BaseFeature001(SwitchPlate_Bent)"
  BindCopyOnChange = 0
  BindMode = 0
  ClaimChildren = false
  Context = -> LinkGroup [Body017.BaseFeature001.]
  FillStyle = 0
  Fuse = true
  MakeFace = true
  OffsetFill = false
  OffsetIntersection = false
  OffsetJoinType = 0
  OffsetOpenResult = false
  PartialLoad = false
  Relative = true
  Support = -> [Body015]
  TreeRank = 361
  _Version = 8
FEATURE [PartDesign::Body] Body017  label="SwitchPlate_Bent_S"
  AutoGroupSolids = false
  BaseFeature = -> BaseFeature001
  ClaimAllChildren = false
  ExportMode = 0
  Group = -> [BaseFeature001]
  Origin = -> Origin017
  Tip = -> BaseFeature001
  TreeRank = 360
  _ExportChildren = -> [BaseFeature001]
  _GroupVersion = 1
FEATURE [Sketcher::SketchObject] Sketch027
  ArcFitTolerance = 1e-06
  AttachmentSupport = -> [XY_Plane018]
  ExternalBSplineMaxDegree = 0
  ExternalBSplineTolerance = 0
  FullyConstrained = true
  MapMode = 5
  Support = -> [XY_Plane018]
  TreeRank = 372
  sketch-geometry (13):
    g0: GeomPoint [constr] X=0 Y=0 Z=0
    g1: Circle CenterX=-10 CenterY=0 CenterZ=0 NormalX=0 NormalY=0 NormalZ=1 AngleXU=0 Radius=1.55
    g2: Circle CenterX=10 CenterY=0 CenterZ=0 NormalX=0 NormalY=0 NormalZ=1 AngleXU=0 Radius=1.55
    g3: ArcOfCircle CenterX=-19 CenterY=4 CenterZ=0 NormalX=0 NormalY=0 NormalZ=1 AngleXU=0 Radius=1 StartAngle=1.5708 EndAngle=3.14159
    g4: LineSegment StartX=-19 StartY=5 StartZ=0 EndX=19 EndY=5 EndZ=0
    g5: ArcOfCircle CenterX=19 CenterY=4 CenterZ=0 NormalX=0 NormalY=0 NormalZ=1 AngleXU=0 Radius=1 StartAngle=0 EndAngle=1.5708
    g6: LineSegment StartX=20 StartY=4 StartZ=0 EndX=20 EndY=-4 EndZ=0
    g7: ArcOfCircle CenterX=19 CenterY=-4 CenterZ=0 NormalX=0 NormalY=0 NormalZ=1 AngleXU=0 Radius=1 StartAngle=4.71239 EndAngle=6.28319
    g8: LineSegment StartX=19 StartY=-5 StartZ=0 EndX=-19 EndY=-5 EndZ=0
    g9: ArcOfCircle CenterX=-19 CenterY=-4 CenterZ=0 NormalX=0 NormalY=0 NormalZ=1 AngleXU=0 Radius=1 StartAngle=3.14159 EndAngle=4.71239
    g10: LineSegment StartX=-20 StartY=-4 StartZ=0 EndX=-20 EndY=4 EndZ=0
    g11: GeomPoint [constr] X=-20 Y=5 Z=0
    g12: GeomPoint [constr] X=20 Y=-5 Z=0
  constraints (29):
    c: Coincident(g0,g-1)
    c: PointOnObject(g1,g-1)
    c: Equal(g2,g1)
    c: Diameter(g1) = 3.1
    c: Symmetric(g1,g2,g-2)
    c: Tangent(g3,g4) = 1.5708
    c: Tangent(g4,g5) = 1.5708
    c: Tangent(g5,g6) = 1.5708
    c: Tangent(g6,g7) = 1.5708
    c: Tangent(g7,g8) = 1.5708
    c: Tangent(g8,g9) = 1.5708
    c: Tangent(g9,g10) = 1.5708
    c: Tangent(g10,g3) = 1.5708
    c: Horizontal(g4)
    c: Horizontal(g8)
    c: Vertical(g6)
    c: Vertical(g10)
    c: Equal(g3,g5)
    c: Equal(g5,g7)
    c: Equal(g7,g9)
    c: PointOnObject(g11,g4)
    c: PointOnObject(g11,g10)
    c: PointOnObject(g12,g6)
    c: PointOnObject(g12,g8)
    c: DistanceX(g3,g5) = 40
    c: DistanceY(g8,g3) = 10
    c: Radius(g3) = 1
    c: Symmetric(g11,g12,g0)
    c: DistanceX(g3,g1) = 10
FEATURE [PartDesign::Pad] Pad021
  AddSubType = 0
  AlongSketchNormal = false
  CheckUpToFaceLimits = true
  ClaimChildren = false
  Direction = (0,0,1)
  Fit = 0
  FitJoin = 0
  InnerFit = 0
  InnerFitJoin = 0
  InnerTaperAngle = 0
  InnerTaperAngleRev = 0
  Length = 1.5
  Length2 = 100
  Linearize = true
  Midplane = true
  NewSolid = false
  Profile = -> Sketch027
  Refine = true
  Suppress = false
  TreeRank = 373
  Type = 0
  _ProfileBasedVersion = 1
FEATURE [PartDesign::Body] Body018  label="Bracket_FrameTop"
  AutoGroupSolids = false
  ClaimAllChildren = false
  ExportMode = 0
  Group = -> [Sketch027,Pad021]
  Origin = -> Origin018
  Tip = -> Pad021
  TreeRank = 371
  _ExportChildren = -> [Pad021]
  _GroupVersion = 1
FEATURE [Sketcher::SketchObject] Sketch028
  ArcFitTolerance = 1e-06
  AttachmentSupport = -> [XZ_Plane019]
  ExternalBSplineMaxDegree = 0
  ExternalBSplineTolerance = 0
  FullyConstrained = true
  MapMode = 5
  Placement = pos=(0,0,0) rot=(1,0,0;1.5708rad)
  Support = -> [XZ_Plane019]
  TreeRank = 384
  expr: Constraints[25] = 8 + 3.1 / 2
  expr: Constraints[27] = 3.1 / 2 + 3
  sketch-geometry (10):
    g0: LineSegment StartX=1.5 StartY=0 StartZ=0 EndX=0 EndY=0 EndZ=0
    g1: LineSegment StartX=0 StartY=0 StartZ=0 EndX=0 EndY=15 EndZ=0
    g2: LineSegment StartX=0 StartY=15 StartZ=0 EndX=14.1 EndY=15 EndZ=0
    g3: LineSegment StartX=14.1 StartY=15 StartZ=0 EndX=14.1 EndY=13.5 EndZ=0
    g4: LineSegment StartX=1.5 StartY=0 StartZ=0 EndX=1.5 EndY=13.5 EndZ=0
    g5: LineSegment StartX=1.5 StartY=13.5 StartZ=0 EndX=14.1 EndY=13.5 EndZ=0
    g6: LineSegment [constr] StartX=12.55 StartY=15 StartZ=0 EndX=12.55 EndY=18 EndZ=0
    g7: LineSegment [constr] StartX=12.55 StartY=18 StartZ=0 EndX=6.55 EndY=18 EndZ=0
    g8: LineSegment [constr] StartX=6.55 StartY=18 StartZ=0 EndX=6.55 EndY=15 EndZ=0
    g9: GeomPoint [constr] X=9.55 Y=18 Z=0
  constraints (28):
    c: Coincident(g0,g1)
    c: Horizontal(g0)
    c: Vertical(g1)
    c: Coincident(g0,g-1)
    c: DistanceX(g0,g0) = 1.5
    c: Coincident(g2,g3)
    c: Horizontal(g2)
    c: Vertical(g3)
    c: Equal(g3,g0)
    c: Coincident(g4,g0)
    c: Vertical(g4)
    c: Coincident(g5,g4)
    c: Coincident(g5,g3)
    c: Horizontal(g5)
    c: DistanceY(g4,g4) = 13.5
    c: Coincident(g6,g7)
    c: Coincident(g7,g8)
    c: Horizontal(g7)
    c: Vertical(g6)
    c: Vertical(g8)
    c: DistanceX(g7,g7) = 6
    c: DistanceY(g6,g6) = 3
    c: Symmetric(g7,g7,g9)
    c: PointOnObject(g8,g2)
    c: PointOnObject(g6,g2)
    c: DistanceX(g1,g9) = 9.55
    c: Coincident(g2,g1)
    c: DistanceX(g9,g2) = 4.55
FEATURE [PartDesign::Pad] Pad022
  AddSubType = 0
  AlongSketchNormal = false
  CheckUpToFaceLimits = true
  ClaimChildren = false
  Direction = (0,-1,-2e-16)
  Fit = 0
  FitJoin = 0
  InnerFit = 0
  InnerFitJoin = 0
  InnerTaperAngle = 0
  InnerTaperAngleRev = 0
  Length = 10
  Length2 = 100
  Linearize = true
  Midplane = true
  NewSolid = false
  Placement = pos=(0,0,0) rot=(1,0,0;1.5708rad)
  Profile = -> Sketch028
  Refine = true
  Suppress = false
  TreeRank = 385
  Type = 0
  _ProfileBasedVersion = 1
FEATURE [Sketcher::SketchObject] Sketch029
  ArcFitTolerance = 1e-06
  AttachmentSupport = -> [XY_Plane019]
  ExternalBSplineMaxDegree = 0
  ExternalBSplineTolerance = 0
  FullyConstrained = true
  MapMode = 5
  Support = -> [XY_Plane019]
  TreeRank = 386
  expr: Constraints[2] = 8 + 3.1 / 2
  sketch-geometry (5):
    g0: Circle [constr] CenterX=9.55 CenterY=0 CenterZ=0 NormalX=0 NormalY=0 NormalZ=1 AngleXU=0 Radius=1.55
    g1: ArcOfCircle CenterX=9.55 CenterY=0 CenterZ=0 NormalX=0 NormalY=0 NormalZ=1 AngleXU=0 Radius=1.55 StartAngle=4.71239 EndAngle=7.85398
    g2: LineSegment StartX=9.55 StartY=-1.55 StartZ=0 EndX=0 EndY=-1.55 EndZ=0
    g3: LineSegment StartX=9.55 StartY=1.55 StartZ=0 EndX=0 EndY=1.55 EndZ=0
    g4: LineSegment StartX=0 StartY=1.55 StartZ=0 EndX=0 EndY=-1.55 EndZ=0
  constraints (15):
    c: PointOnObject(g0,g-1)
    c: Diameter(g0) = 3.1
    c: DistanceX(g-1,g0) = 9.55
    c: Coincident(g1,g0)
    c: PointOnObject(g1,g0)
    c: Vertical(g1,g0)
    c: Vertical(g0,g1)
    c: Coincident(g2,g1)
    c: PointOnObject(g2,g-2)
    c: Horizontal(g2)
    c: Coincident(g3,g1)
    c: PointOnObject(g3,g-2)
    c: Horizontal(g3)
    c: Coincident(g4,g3)
    c: Coincident(g4,g2)
FEATURE [PartDesign::Pocket] Pocket002
  AddSubType = 1
  BaseFeature = -> Pad022
  CheckUpToFaceLimits = true
  ClaimChildren = false
  Fit = 0
  FitJoin = 0
  InnerFit = 0
  InnerFitJoin = 0
  InnerTaperAngle = 0
  InnerTaperAngleRev = 0
  Length = 5
  Length2 = 100
  Linearize = true
  NewSolid = false
  Placement = pos=(0,0,0) rot=(1,0,0;1.5708rad)
  Profile = -> Sketch029
  Refine = true
  Reversed = true
  Suppress = false
  TreeRank = 387
  Type = 1
  _ProfileBasedVersion = 1
  _Version = 1
FEATURE [PartDesign::SubShapeBinder] BaseFeature002  label="BaseFeature002(SwitchPlate_Bent)"
  BindCopyOnChange = 0
  BindMode = 0
  ClaimChildren = false
  Context = -> Body020 [BaseFeature002.]
  FillStyle = 0
  Fuse = true
  MakeFace = true
  OffsetFill = false
  OffsetIntersection = false
  OffsetJoinType = 0
  OffsetOpenResult = false
  PartialLoad = false
  Relative = true
  Support = -> [Body015]
  TreeRank = 400
  _Version = 8
FEATURE [Part::SubShapeBinder] Import013  label="Import013(SketchSwitches)"
  BindCopyOnChange = 0
  BindMode = 0
  ClaimChildren = false
  Context = -> Body020 [Import013.]
  FillStyle = 0
  Fuse = false
  MakeFace = false
  OffsetFill = false
  OffsetIntersection = false
  OffsetJoinType = 0
  OffsetOpenResult = false
  PartialLoad = false
  Relative = true
  Support = -> [Sketch011]
  TreeRank = 402
  _Version = 8
FEATURE [Sketcher::SketchObject] Sketch030
  ArcFitTolerance = 1e-06
  AttachmentSupport = -> [XY_Plane020]
  ExternalBSplineMaxDegree = 0
  ExternalBSplineTolerance = 0
  ExternalGeometry = -> [BaseFeature002,Import013]
  FullyConstrained = true
  MapMode = 5
  Support = -> [XY_Plane020]
  TreeRank = 401
  sketch-geometry (6):
    g0: Circle CenterX=19 CenterY=-52.95 CenterZ=0 NormalX=0 NormalY=0 NormalZ=1 AngleXU=0 Radius=1.55
    g1: Circle CenterX=-105.45 CenterY=28.35 CenterZ=0 NormalX=0 NormalY=0 NormalZ=1 AngleXU=0 Radius=1.55
    g2: Circle CenterX=105.45 CenterY=28.35 CenterZ=0 NormalX=0 NormalY=0 NormalZ=1 AngleXU=0 Radius=1.55
    g3: LineSegment [constr] StartX=-105.45 StartY=28.35 StartZ=0 EndX=-115 EndY=28.35 EndZ=0
    g4: Circle CenterX=-105.45 CenterY=-2.5 CenterZ=0 NormalX=0 NormalY=0 NormalZ=1 AngleXU=0 Radius=1.55
    g5: Circle CenterX=105.45 CenterY=-2.5 CenterZ=0 NormalX=0 NormalY=0 NormalZ=1 AngleXU=0 Radius=1.55
  constraints (18):
    c: Equal(g0,g2)
    c: Equal(g2,g1)
    c: Diameter(g1) = 3.1
    c: Horizontal(g1,g2)
    c: DistanceX(g-3,g1) = 9.55
    c: DistanceX(g2,g-4) = 9.55
    c: DistanceY(g-5,g0) = 9.55
    c: DistanceX(g0,g-5) = 5
    c: Coincident(g3,g1)
    c: Horizontal(g3)
    c: PointOnObject(g3,g-3)
    c: DistanceY(g1,g-3) = 10
    c: Equal(g4,g1)
    c: Vertical(g1,g4)
    c: DistanceY(g-3,g4) = 10
    c: Equal(g5,g2)
    c: Vertical(g2,g5)
    c: Horizontal(g5,g4)
FEATURE [PartDesign::Pocket] Pocket003
  AddSubType = 1
  BaseFeature = -> BaseFeature002
  CheckUpToFaceLimits = true
  ClaimChildren = false
  Fit = 0
  FitJoin = 0
  InnerFit = 0
  InnerFitJoin = 0
  InnerTaperAngle = 0
  InnerTaperAngleRev = 0
  Length = 5
  Length2 = 100
  Linearize = true
  Midplane = true
  NewSolid = false
  Profile = -> Sketch030
  Refine = true
  Suppress = false
  TreeRank = 403
  Type = 1
  _ProfileBasedVersion = 1
  _Version = 1
FEATURE [PartDesign::Fillet] Fillet026
  AddSubType = 0
  Base = -> Pocket003 [Edge152,Edge156,Edge160,Edge164,Edge158,Edge154,Edge150,Edge147,Edge148]
  BaseFeature = -> Pocket003
  NewSolid = false
  Radius = 1
  Refine = true
  SupportTransform = false
  Suppress = false
  TreeRank = 404
FEATURE [PartDesign::Body] Body020  label="SwitchPlate_BentBrackets"
  AutoGroupSolids = false
  BaseFeature = -> BaseFeature002
  ClaimAllChildren = false
  ExportMode = 0
  Group = -> [BaseFeature002,Sketch030,Import013,Pocket003,Fillet026]
  Origin = -> Origin020
  Tip = -> Fillet026
  TreeRank = 399
  _ExportChildren = -> [BaseFeature002,Import013,Pocket003,Fillet026]
  _GroupVersion = 1
FEATURE [Sketcher::SketchObject] Sketch031
  ArcFitTolerance = 1e-06
  AttachmentSupport = -> [YZ_Plane019]
  ExternalBSplineMaxDegree = 0
  ExternalBSplineTolerance = 0
  ExternalGeometry = -> [Pocket002]
  FullyConstrained = true
  MapMode = 5
  Placement = pos=(0,0,0) rot=(0.57735,0.57735,0.57735;2.0944rad)
  Support = -> [YZ_Plane019]
  TreeRank = 405
  sketch-geometry (4):
    g0: ArcOfCircle CenterX=0 CenterY=7 CenterZ=0 NormalX=0 NormalY=0 NormalZ=1 AngleXU=0 Radius=1.55 StartAngle=3.14159 EndAngle=6.28319
    g1: LineSegment StartX=-1.55 StartY=7.00001 StartZ=0 EndX=-1.55 EndY=0 EndZ=0
    g2: LineSegment StartX=-1.55 StartY=0 StartZ=0 EndX=1.55 EndY=-7e-16 EndZ=0
    g3: LineSegment StartX=1.55 StartY=-7e-16 StartZ=0 EndX=1.55 EndY=7 EndZ=0
  constraints (11):
    c: PointOnObject(g0,g-2)
    c: PointOnObject(g0,g-3)
    c: PointOnObject(g0,g-4)
    c: Coincident(g0,g1)
    c: Coincident(g1,g2)
    c: Coincident(g2,g-4)
    c: Coincident(g2,g3)
    c: Coincident(g3,g0)
    c: Coincident(g-3,g1)
    c: Horizontal(g0,g0)
    c: Distance(g0,g-5) = 8
FEATURE [PartDesign::FeaturePython] SolidBend001  # WARN: FeaturePython — macro-defined, semantics opaque (R4)
  BaseFeature = -> Pocket002
  NewSolid = false
  Suppress = false
  TreeRank = 406
  baseObject = -> Pocket002 [Edge25,Edge16]
  radius = 1.5
  thickness = 1.5
FEATURE [PartDesign::Pad] Pad023
  AddSubType = 0
  AlongSketchNormal = false
  BaseFeature = -> SolidBend001
  CheckUpToFaceLimits = true
  ClaimChildren = false
  Direction = (1,-3e-16,3e-16)
  Fit = 0
  FitJoin = 0
  InnerFit = 0
  InnerFitJoin = 0
  InnerTaperAngle = 0
  InnerTaperAngleRev = 0
  Length = 1.5
  Length2 = 100
  Linearize = true
  NewSolid = false
  Profile = -> Sketch031
  Refine = true
  Suppress = false
  TreeRank = 407
  Type = 0
  _ProfileBasedVersion = 1
FEATURE [PartDesign::Fillet] Fillet027
  AddSubType = 0
  Base = -> Pad023 [Edge4,Edge39,Edge37,Edge23]
  BaseFeature = -> Pad023
  NewSolid = false
  Radius = 1
  Refine = true
  SupportTransform = false
  Suppress = false
  TreeRank = 408
FEATURE [PartDesign::Body] Body019  label="Bracket_Bent"
  AutoGroupSolids = false
  ClaimAllChildren = false
  ExportMode = 0
  Group = -> [Sketch028,Pad022,Sketch029,Pocket002,Sketch031,SolidBend001,Pad023,Fillet027]
  Origin = -> Origin019
  Tip = -> Fillet027
  TreeRank = 383
  _ExportChildren = -> [Pad022,Pocket002,SolidBend001,Pad023,Fillet027]
  _GroupVersion = 1
FEATURE [App::LinkGroup] LinkGroup  label="Deprecated"
  ElementList = -> [Body,Body005,Body008,Body010,Body006,Body009,Body011,Body020,Body019,Body018,Body017,Body016,Body015]
  LinkMode = 0
  TreeRank = 314
  _LinkVersion = 1
FEATURE [App::LinkGroup] LinkGroup001  label="Alternates"
  ElementList = -> [Body012]
  LinkMode = 0
  TreeRank = 409
  _LinkVersion = 1
FEATURE [Part::SubShapeBinder] Import014  label="Import014(SketchFrame)"
  BindCopyOnChange = 0
  BindMode = 0
  ClaimChildren = false
  Context = -> Body021 [Import014.]
  FillStyle = 0
  Fuse = false
  MakeFace = false
  OffsetFill = false
  OffsetIntersection = false
  OffsetJoinType = 0
  OffsetOpenResult = false
  PartialLoad = false
  Relative = true
  Support = -> [Sketch006]
  TreeRank = 420
  _Version = 8
FEATURE [Part::SubShapeBinder] Import015  label="Import015(SketchSwitches)"
  BindCopyOnChange = 0
  BindMode = 0
  ClaimChildren = false
  Context = -> Body021 [Import015.]
  FillStyle = 0
  Fuse = false
  MakeFace = false
  OffsetFill = false
  OffsetIntersection = false
  OffsetJoinType = 0
  OffsetOpenResult = false
  PartialLoad = false
  Relative = true
  Support = -> [Sketch011]
  TreeRank = 421
  _Version = 8
FEATURE [Part::SubShapeBinder] Import016  label="Import016(SketchLED)"
  BindCopyOnChange = 0
  BindMode = 0
  ClaimChildren = false
  Context = -> Body021 [Import016.]
  FillStyle = 0
  Fuse = false
  MakeFace = false
  OffsetFill = false
  OffsetIntersection = false
  OffsetJoinType = 0
  OffsetOpenResult = false
  PartialLoad = false
  Relative = true
  Support = -> [Sketch014]
  TreeRank = 422
  _Version = 8
FEATURE [Sketcher::SketchObject] Sketch032
  ArcFitTolerance = 1e-06
  AttachmentSupport = -> [XY_Plane021]
  ExternalBSplineMaxDegree = 0
  ExternalBSplineTolerance = 0
  ExternalGeometry = -> [Import014,Import015,Import016]
  FullyConstrained = true
  MapMode = 5
  Support = -> [XY_Plane021]
  TreeRank = 419
  sketch-geometry (71):
    g0: LineSegment [constr] StartX=-115 StartY=62.5 StartZ=0 EndX=-94 EndY=62.5 EndZ=0
    g1: LineSegment [constr] StartX=-94 StartY=62.5 StartZ=0 EndX=-94 EndY=41.5 EndZ=0
    g2: LineSegment [constr] StartX=-94 StartY=41.5 StartZ=0 EndX=-115 EndY=41.5 EndZ=0
    g3: LineSegment [constr] StartX=-115 StartY=41.5 StartZ=0 EndX=-115 EndY=62.5 EndZ=0
    g4: LineSegment [constr] StartX=-115 StartY=-62.5 StartZ=0 EndX=-94 EndY=-62.5 EndZ=0
    g5: LineSegment [constr] StartX=-94 StartY=-62.5 StartZ=0 EndX=-94 EndY=-41.5 EndZ=0
    g6: LineSegment [constr] StartX=-94 StartY=-41.5 StartZ=0 EndX=-115 EndY=-41.5 EndZ=0
    g7: LineSegment [constr] StartX=-115 StartY=-41.5 StartZ=0 EndX=-115 EndY=-62.5 EndZ=0
    g8: LineSegment [constr] StartX=115 StartY=62.5 StartZ=0 EndX=94 EndY=62.5 EndZ=0
    g9: LineSegment [constr] StartX=94 StartY=62.5 StartZ=0 EndX=94 EndY=41.5 EndZ=0
    g10: LineSegment [constr] StartX=94 StartY=41.5 StartZ=0 EndX=115 EndY=41.5 EndZ=0
    g11: LineSegment [constr] StartX=115 StartY=41.5 StartZ=0 EndX=115 EndY=62.5 EndZ=0
    g12: LineSegment [constr] StartX=115 StartY=-62.5 StartZ=0 EndX=94 EndY=-62.5 EndZ=0
    g13: LineSegment [constr] StartX=94 StartY=-62.5 StartZ=0 EndX=94 EndY=-41.5 EndZ=0
    g14: LineSegment [constr] StartX=94 StartY=-41.5 StartZ=0 EndX=115 EndY=-41.5 EndZ=0
    g15: LineSegment [constr] StartX=115 StartY=-41.5 StartZ=0 EndX=115 EndY=-62.5 EndZ=0
    g16: ArcOfCircle CenterX=1e-16 CenterY=-48.5 CenterZ=0 NormalX=0 NormalY=0 NormalZ=1 AngleXU=0 Radius=13 StartAngle=0 EndAngle=3.14159
    g17: LineSegment StartX=-13 StartY=-60.5 StartZ=0 EndX=-13 EndY=-48.5 EndZ=0
    g18: LineSegment StartX=13 StartY=-48.5 StartZ=0 EndX=13 EndY=-60.5 EndZ=0
    g19: GeomPoint [constr] X=-11.7 Y=35.35 Z=0
    g20: ArcOfCircle [constr] CenterX=-89.5 CenterY=57 CenterZ=0 NormalX=0 NormalY=0 NormalZ=1 AngleXU=0 Radius=7 StartAngle=1.5708 EndAngle=4.71239
    g21: ArcOfCircle [constr] CenterX=-47.5 CenterY=57 CenterZ=0 NormalX=0 NormalY=0 NormalZ=1 AngleXU=0 Radius=7 StartAngle=4.71239 EndAngle=7.85398
    g22: LineSegment [constr] StartX=-89.5 StartY=50 StartZ=0 EndX=-47.5 EndY=50 EndZ=0
    g23: LineSegment [constr] StartX=-47.5 StartY=64 StartZ=0 EndX=-89.5 EndY=64 EndZ=0
    g24: ArcOfCircle [constr] CenterX=47.5 CenterY=57 CenterZ=0 NormalX=0 NormalY=0 NormalZ=1 AngleXU=0 Radius=7 StartAngle=1.5708 EndAngle=4.71239
    g25: ArcOfCircle [constr] CenterX=89.5 CenterY=57 CenterZ=0 NormalX=0 NormalY=0 NormalZ=1 AngleXU=0 Radius=7 StartAngle=4.71239 EndAngle=7.85398
    g26: LineSegment [constr] StartX=47.5 StartY=50 StartZ=0 EndX=89.5 EndY=50 EndZ=0
    g27: LineSegment [constr] StartX=89.5 StartY=64 StartZ=0 EndX=47.5 EndY=64 EndZ=0
    g28: LineSegment StartX=-94 StartY=41.5 StartZ=0 EndX=-94 EndY=50 EndZ=0
    g29: LineSegment StartX=-94 StartY=50 StartZ=0 EndX=94 EndY=50 EndZ=0
    g30: LineSegment StartX=94 StartY=50 StartZ=0 EndX=94 EndY=41.5 EndZ=0
    g31: LineSegment StartX=-13 StartY=-60.5 StartZ=0 EndX=-94 EndY=-60.5 EndZ=0
    g32: LineSegment StartX=-94 StartY=-60.5 StartZ=0 EndX=-94 EndY=-41.5 EndZ=0
    g33: LineSegment StartX=-94 StartY=-41.5 StartZ=0 EndX=-113 EndY=-41.5 EndZ=0
    g34: LineSegment StartX=-113 StartY=-41.5 StartZ=0 EndX=-113 EndY=41.5 EndZ=0
    g35: LineSegment StartX=-113 StartY=41.5 StartZ=0 EndX=-94 EndY=41.5 EndZ=0
    g36: LineSegment StartX=13 StartY=-60.5 StartZ=0 EndX=94 EndY=-60.5 EndZ=0
    g37: LineSegment StartX=94 StartY=41.5 StartZ=0 EndX=113 EndY=41.5 EndZ=0
    g38: LineSegment StartX=113 StartY=41.5 StartZ=0 EndX=113 EndY=-41.5 EndZ=0
    g39: LineSegment StartX=113 StartY=-41.5 StartZ=0 EndX=94 EndY=-41.5 EndZ=0
    g40: LineSegment StartX=94 StartY=-41.5 StartZ=0 EndX=94 EndY=-60.5 EndZ=0
    g41: Circle CenterX=-15 CenterY=-2.5 CenterZ=0 NormalX=0 NormalY=0 NormalZ=1 AngleXU=0 Radius=13
    g42: ArcOfCircle CenterX=-65 CenterY=11.5 CenterZ=0 NormalX=0 NormalY=0 NormalZ=1 AngleXU=0 Radius=13 StartAngle=1.5708 EndAngle=4.71239
    g43: ArcOfCircle CenterX=-40 CenterY=11.5 CenterZ=0 NormalX=0 NormalY=0 NormalZ=1 AngleXU=0 Radius=13 StartAngle=4.71239 EndAngle=7.85398
    g44: LineSegment StartX=-65 StartY=-1.5 StartZ=0 EndX=-40 EndY=-1.5 EndZ=0
    g45: LineSegment StartX=-40 StartY=24.5 StartZ=0 EndX=-65 EndY=24.5 EndZ=0
    g46: ArcOfCircle CenterX=14 CenterY=-15 CenterZ=0 NormalX=0 NormalY=0 NormalZ=1 AngleXU=0 Radius=13 StartAngle=3.14159 EndAngle=5.22288
    g47: ArcOfCircle CenterX=89 CenterY=-8 CenterZ=0 NormalX=0 NormalY=0 NormalZ=1 AngleXU=0 Radius=13 StartAngle=4.42677 EndAngle=6.28319
    g48: ArcOfCircle CenterX=89 CenterY=17 CenterZ=0 NormalX=0 NormalY=0 NormalZ=1 AngleXU=0 Radius=13 StartAngle=4e-16 EndAngle=1.29779
    g49: ArcOfCircle CenterX=64 CenterY=24 CenterZ=0 NormalX=0 NormalY=0 NormalZ=1 AngleXU=0 Radius=13 StartAngle=1.29779 EndAngle=1.5708
    g50: ArcOfCircle CenterX=39 CenterY=24 CenterZ=0 NormalX=0 NormalY=0 NormalZ=1 AngleXU=0 Radius=13 StartAngle=1.5708 EndAngle=2.08128
    g51: ArcOfCircle [constr] CenterX=14 CenterY=10 CenterZ=0 NormalX=0 NormalY=0 NormalZ=1 AngleXU=0 Radius=13 StartAngle=2.08128 EndAngle=3.14159
    g52: LineSegment StartX=20.3518 StartY=-26.3426 StartZ=0 EndX=45.3518 EndY=-12.3426 EndZ=0
    g53: LineSegment StartX=85.3373 StartY=-20.4733 StartZ=0 EndX=57.6482 EndY=-12.3426 EndZ=0
    g54: LineSegment StartX=1 StartY=-15 StartZ=0 EndX=1 EndY=10 EndZ=0
    g55: LineSegment [constr] StartX=7.64816 StartY=21.3426 StartZ=0 EndX=32.6482 EndY=35.3426 EndZ=0
    g56: LineSegment StartX=39 StartY=37 StartZ=0 EndX=64 EndY=37 EndZ=0
    g57: LineSegment StartX=67.5052 StartY=36.5185 StartZ=0 EndX=92.5052 EndY=29.5185 EndZ=0
    g58: LineSegment StartX=102 StartY=17 StartZ=0 EndX=102 EndY=-8 EndZ=0
    g59: LineSegment [constr] StartX=89 StartY=17 StartZ=0 EndX=89 EndY=-8 EndZ=0
    g60: LineSegment StartX=45.3518 StartY=-12.3426 StartZ=0 EndX=57.6482 EndY=-12.3426 EndZ=0
    g61: LineSegment [constr] StartX=39 StartY=-1 StartZ=0 EndX=64 EndY=-1 EndZ=0
    g62: LineSegment [constr] StartX=14 StartY=-15 StartZ=0 EndX=39 EndY=-1 EndZ=0
    g63: ArcOfCircle CenterX=-19.9 CenterY=29 CenterZ=0 NormalX=0 NormalY=0 NormalZ=1 AngleXU=0 Radius=8.35 StartAngle=1.5708 EndAngle=4.71239
    g64: ArcOfCircle [constr] CenterX=19.9 CenterY=29 CenterZ=0 NormalX=0 NormalY=0 NormalZ=1 AngleXU=0 Radius=8.35 StartAngle=4.71239 EndAngle=7.85398
    g65: LineSegment [constr] StartX=-19.9 StartY=20.65 StartZ=0 EndX=19.9 EndY=20.65 EndZ=0
    g66: LineSegment StartX=19.9 StartY=37.35 StartZ=0 EndX=-19.9 EndY=37.35 EndZ=0
    g67: ArcOfCircle CenterX=19.9 CenterY=29 CenterZ=0 NormalX=0 NormalY=0 NormalZ=1 AngleXU=0 Radius=8.35 StartAngle=0.427176 EndAngle=1.5708
    g68: LineSegment StartX=27.4997 StartY=32.4594 StartZ=0 EndX=32.6482 EndY=35.3426 EndZ=0
    g69: LineSegment StartX=-19.9 StartY=20.65 StartZ=0 EndX=6.54497 EndY=20.65 EndZ=0
    g70: ArcOfCircle CenterX=14 CenterY=10 CenterZ=0 NormalX=0 NormalY=0 NormalZ=1 AngleXU=0 Radius=13 StartAngle=2.18152 EndAngle=3.14159
  constraints (171):
    c: Coincident(g0,g1)
    c: Coincident(g1,g2)
    c: Coincident(g2,g3)
    c: Coincident(g3,g0)
    c: Horizontal(g0)
    c: Horizontal(g2)
    c: Vertical(g1)
    c: Vertical(g3)
    c: Coincident(g0,g-6)
    c: Coincident(g4,g5)
    c: Coincident(g5,g6)
    c: Coincident(g6,g7)
    c: Coincident(g7,g4)
    c: Horizontal(g4)
    c: Horizontal(g6)
    c: Vertical(g5)
    c: Vertical(g7)
    c: Coincident(g4,g-4)
    c: Coincident(g8,g9)
    c: Coincident(g9,g10)
    c: Coincident(g10,g11)
    c: Coincident(g11,g8)
    c: Horizontal(g8)
    c: Horizontal(g10)
    c: Vertical(g9)
    c: Vertical(g11)
    c: Coincident(g8,g-6)
    c: Coincident(g12,g13)
    c: Coincident(g13,g14)
    c: Coincident(g14,g15)
    c: Coincident(g15,g12)
    c: Horizontal(g12)
    c: Horizontal(g14)
    c: Vertical(g13)
    c: Vertical(g15)
    c: Coincident(g12,g-5)
    c: Equal(g6,g5)
    c: Equal(g5,g2)
    c: Equal(g2,g1)
    c: Equal(g1,g9)
    c: Equal(g9,g10)
    c: Equal(g10,g14)
    c: Equal(g14,g13)
    c: DistanceX(g2,g2) = 21
    c: Coincident(g16,g-16)
    c: Radius(g16) = 13
    c: Coincident(g17,g16)
    c: Vertical(g17)
    c: Coincident(g16,g18)
    c: Vertical(g18)
    c: Horizontal(g16,g16)
    c: Horizontal(g16,g16)
    c: PointOnObject(g19,g-33)
    c: Vertical(g-33,g19)
    c: Tangent(g20,g22) = -1.5708
    c: Tangent(g22,g21) = -1.5708
    c: Tangent(g21,g23) = -1.5708
    c: Tangent(g23,g20) = -1.5708
    c: Equal(g20,g21)
    c: Coincident(g20,g-7)
    c: Coincident(g21,g-9)
    c: Tangent(g24,g26) = -1.5708
    c: Tangent(g26,g25) = -1.5708
    c: Tangent(g25,g27) = -1.5708
    c: Tangent(g27,g24) = -1.5708
    c: Equal(g24,g25)
    c: Coincident(g24,g-10)
    c: Coincident(g25,g-12)
    c: Equal(g24,g20)
    c: Radius(g20) = 7
    c: Coincident(g2,g28)
    c: PointOnObject(g28,g1)
    c: Coincident(g28,g29)
    c: Horizontal(g29)
    c: Tangent(g29,g21)
    c: PointOnObject(g29,g9)
    c: Coincident(g30,g29)
    c: Coincident(g30,g10)
    c: Coincident(g17,g31)
    c: PointOnObject(g31,g5)
    c: Horizontal(g31)
    c: Coincident(g31,g32)
    c: Coincident(g32,g5)
    c: Coincident(g32,g33)
    c: PointOnObject(g33,g6)
    c: Coincident(g33,g34)
    c: PointOnObject(g34,g2)
    c: Vertical(g34)
    c: Coincident(g34,g35)
    c: Coincident(g35,g28)
    c: DistanceX(g2,g34) = 2
    c: DistanceY(g4,g31) = 2
    c: Coincident(g36,g18)
    c: PointOnObject(g36,g13)
    c: Horizontal(g36)
    c: Horizontal(g17,g18)
    c: Coincident(g30,g37)
    c: PointOnObject(g37,g10)
    c: Coincident(g37,g38)
    c: PointOnObject(g38,g14)
    c: Vertical(g38)
    c: Coincident(g38,g39)
    c: Coincident(g39,g13)
    c: Coincident(g39,g40)
    c: Coincident(g40,g36)
    c: DistanceX(g38,g14) = 2
    c: Coincident(g41,g-15)
    c: Tangent(g42,g44) = -1.5708
    c: Tangent(g44,g43) = -1.5708
    c: Tangent(g43,g45) = -1.5708
    c: Tangent(g45,g42) = -1.5708
    c: Equal(g42,g43)
    c: Coincident(g42,g-13)
    c: Coincident(g43,g-14)
    c: Radius(g42) = 13
    c: Equal(g41,g43)
    c: Coincident(g46,g-17)
    c: Coincident(g47,g-24)
    c: Coincident(g48,g-23)
    c: Coincident(g49,g-21)
    c: Coincident(g50,g-19)
    c: Coincident(g51,g-18)
    c: Equal(g43,g46)
    c: Equal(g46,g51)
    c: Equal(g51,g50)
    c: Equal(g50,g49)
    c: Equal(g49,g48)
    c: Equal(g48,g47)
    c: Tangent(g52,g46) = -1.5708
    c: Distance(g52,g-20) = 13
    c: Tangent(g53,g47) = 1.5708
    c: Tangent(g54,g46) = 1.5708
    c: Tangent(g54,g51) = 1.5708
    c: Tangent(g51,g55) = 1.5708
    c: Tangent(g55,g50) = 1.5708
    c: Tangent(g56,g50) = 1.5708
    c: Tangent(g56,g49) = 1.5708
    c: Tangent(g57,g49) = 1.5708
    c: Tangent(g57,g48) = 1.5708
    c: Coincident(g58,g47)
    c: Tangent(g58,g48) = 1.5708
    c: Coincident(g59,g48)
    c: Coincident(g59,g47)
    c: Parallel(g59,g58)
    c: Distance(g53,g-22) = 13
    c: Coincident(g60,g52)
    c: Coincident(g60,g53)
    c: Coincident(g61,g-20)
    c: Coincident(g61,g-22)
    c: Parallel(g60,g61)
    c: Coincident(g62,g46)
    c: Coincident(g62,g-20)
    c: Parallel(g62,g52)
    c: Tangent(g63,g65) = -1.5708
    c: Tangent(g65,g64) = -1.5708
    c: Tangent(g64,g66) = -1.5708
    c: Tangent(g66,g63) = -1.5708
    c: Equal(g63,g64)
    c: Symmetric(g-35,g-35,g63)
    c: Symmetric(g-36,g-36,g64)
    c: DistanceY(g19,g63) = 2
    c: Coincident(g67,g64)
    c: Coincident(g67,g66)
    c: PointOnObject(g67,g55)
    c: Coincident(g68,g67)
    c: Coincident(g68,g50)
    c: Coincident(g69,g63)
    c: PointOnObject(g69,g65)
    c: Coincident(g70,g-18)
    c: Coincident(g70,g69)
    c: Coincident(g70,g54)
FEATURE [PartDesign::Pad] Pad024
  AddSubType = 0
  AlongSketchNormal = false
  CheckUpToFaceLimits = true
  ClaimChildren = false
  Direction = (0,0,1)
  Fit = 0
  FitJoin = 0
  InnerFit = 0
  InnerFitJoin = 0
  InnerTaperAngle = 0
  InnerTaperAngleRev = 0
  Length = 2
  Length2 = 100
  Linearize = true
  Midplane = true
  NewSolid = false
  Profile = -> Sketch032
  Refine = true
  Suppress = false
  TreeRank = 423
  Type = 0
  _ProfileBasedVersion = 1
FEATURE [PartDesign::Fillet] Fillet028
  AddSubType = 0
  Base = -> Pad024 [Edge11,Edge8,Edge2,Edge44,Edge41,Edge38,Edge35,Edge32,Edge29,Edge26,Edge23,Edge20,Edge17,Edge14,Edge59,Edge49,Edge74,Edge71]
  BaseFeature = -> Pad024
  NewSolid = false
  Radius = 4
  Refine = true
  SupportTransform = false
  Suppress = false
  TreeRank = 424
FEATURE [PartDesign::Body] Body021  label="ControlPanelFoam"
  AutoGroupSolids = false
  ClaimAllChildren = false
  ExportMode = 0
  Group = -> [Sketch032,Import014,Import015,Import016,Pad024,Fillet028]
  Origin = -> Origin021
  SingleSolid = true
  Tip = -> Fillet028
  TreeRank = 313
  _ExportChildren = -> [Import014,Import015,Import016,Pad024,Fillet028]
  _GroupVersion = 1
